FCSTD DOCUMENT  (FreeCAD 1.0R39109 (Git))
Label: internalDesign_base_Rittik
License: All rights reserved
LicenseURL: http://en.wikipedia.org/wiki/All_rights_reserved
objects: Part::Feature×500, App::Part×91, Part::Box×68, Part::Cylinder×66, Part::MultiFuse×50, Part::Cut×48, Sketcher::SketchObject×33, Part::Extrusion×32, Part::Fillet×30, Part::Compound×8, Part::Sphere×4, Part::FeaturePython×2, Part::Torus×1
note: 875 computed .brp shape members not serialized (recipe doc carries the construction recipe); baked Part::Feature solids carry a one-line shape summary decoded from their .brp

FEATURE [Part::Feature] Part__Feature016  label="Z_-16147B_ZH-16147B-01"
  shape: bbox 438.9 x 219.4 x 405.1 mm, 3210 faces (baked)
FEATURE [Part::Feature] Part__Feature017  label="INSERTS-4"
  Placement = pos=(-180.975,-168.256,-155.575) rot=(0,0,1;0rad)
  shape: bbox 7.519 x 8.463 x 7.519 mm, 71 faces (baked)
FEATURE [Part::Feature] Part__Feature018  label="INSERTS-005"
  Placement = pos=(-170.872,-174.835,-145.472) rot=(0,0,1;3.14159rad)
  shape: bbox 7.519 x 8.463 x 7.519 mm, 71 faces (baked)
FEATURE [Part::Feature] Part__Feature019  label="INSERTS-006"
  Placement = pos=(-205.994,-3.7592,-180.594) rot=(0,0,1;3.14159rad)
  shape: bbox 7.519 x 8.463 x 7.519 mm, 71 faces (baked)
FEATURE [Part::Feature] Part__Feature020  label="INSERTS-007"
  Placement = pos=(-180.975,-168.083,155.575) rot=(1,0,0;3.14159rad)
  shape: bbox 7.519 x 8.463 x 7.519 mm, 71 faces (baked)
FEATURE [Part::Feature] Part__Feature021  label="INSERTS-008"
  Placement = pos=(-170.872,-175.008,145.472) rot=(0,1,0;3.14159rad)
  shape: bbox 7.519 x 8.463 x 7.519 mm, 71 faces (baked)
FEATURE [Part::Feature] Part__Feature022  label="INSERTS-009"
  Placement = pos=(-205.994,-3.93217,180.594) rot=(0,1,0;3.14159rad)
  shape: bbox 7.519 x 8.463 x 7.519 mm, 71 faces (baked)
FEATURE [Part::Feature] Part__Feature023  label="INSERTS-010"
  Placement = pos=(180.975,-168.083,-155.575) rot=(0,0,1;3.14159rad)
  shape: bbox 7.519 x 8.463 x 7.519 mm, 71 faces (baked)
FEATURE [Part::Feature] Part__Feature024  label="INSERTS-011"
  Placement = pos=(170.872,-175.008,-145.472) rot=(0,0,1;0rad)
  shape: bbox 7.519 x 8.463 x 7.519 mm, 71 faces (baked)
FEATURE [Part::Feature] Part__Feature025  label="INSERTS-012"
  Placement = pos=(205.994,-3.93217,-180.594) rot=(0,0,1;0rad)
  shape: bbox 7.519 x 8.463 x 7.519 mm, 71 faces (baked)
FEATURE [Part::Feature] Part__Feature026  label="INSERTS-013"
  Placement = pos=(180.975,-168.256,155.575) rot=(0,1,0;3.14159rad)
  shape: bbox 7.519 x 8.463 x 7.519 mm, 71 faces (baked)
FEATURE [Part::Feature] Part__Feature027  label="INSERTS-014"
  Placement = pos=(170.872,-174.835,145.472) rot=(1,0,0;3.14159rad)
  shape: bbox 7.519 x 8.463 x 7.519 mm, 71 faces (baked)
FEATURE [Part::Feature] Part__Feature028  label="INSERTS-015"
  Placement = pos=(205.994,-3.7592,180.594) rot=(1,0,0;3.14159rad)
  shape: bbox 7.519 x 8.463 x 7.519 mm, 71 faces (baked)
FEATURE [Part::Feature] Part__Feature029  label="LABEL-104"
  Placement = pos=(-1.221e-12,-20.3197,-180.67) rot=(1,0,0;1.56207rad)
  shape: bbox 63.5 x 38.1 x 0.3833 mm, 10 faces (baked)
FEATURE [Part::Feature] Part__Feature030  label="Z_-16141C_ZH-16141C-01"
  shape: bbox 448.9 x 49.63 x 409 mm, 1738 faces (baked)
FEATURE [Part::Feature] Part__Feature031  label="ZH-1614G"
  Placement = pos=(0,0.635,6.9e-15) rot=(0,0,1;0rad)
  shape: bbox 434.5 x 6.35 x 383.7 mm, 136 faces (baked)
FEATURE [Part::Feature] Part__Feature032  label="ZH-01F_ZH-01F-01"
  Placement = pos=(-158.172,-191.294,-145.472) rot=(0,0,1;0rad)
  shape: bbox 75.05 x 15.88 x 54.71 mm, 393 faces (baked)
FEATURE [Part::Feature] Part__Feature033  label="pan cross head_ai_SCREWS-046"
  Placement = pos=(-170.872,-191.294,-145.472) rot=(-0.002139,-0.002139,0.999995;1.5708rad)
  shape: bbox 10.25 x 22.43 x 10.25 mm, 92 faces (baked)
FEATURE [Part::Feature] Part__Feature034  label="pan cross head_ai_SCREWS-047"
  Placement = pos=(-170.872,-191.294,145.472) rot=(0.002139,0.002139,0.999995;1.5708rad)
  shape: bbox 10.25 x 22.43 x 10.25 mm, 92 faces (baked)
FEATURE [Part::Feature] Part__Feature035  label="ZH-01F_ZH-01F-002"
  Placement = pos=(-158.172,-191.294,145.472) rot=(0,0,1;0rad)
  shape: bbox 75.05 x 15.88 x 54.71 mm, 393 faces (baked)
FEATURE [Part::Feature] Part__Feature036  label="pan cross head_ai_SCREWS-048"
  Placement = pos=(170.872,-191.294,-145.472) rot=(0.707106,0.707106,-0.001512;3.14462rad)
  shape: bbox 10.25 x 22.43 x 10.25 mm, 92 faces (baked)
FEATURE [Part::Feature] Part__Feature037  label="pan cross head_ai_SCREWS-049"
  Placement = pos=(170.872,-191.294,145.472) rot=(0.707106,0.707106,0.001512;3.13857rad)
  shape: bbox 10.25 x 22.43 x 10.25 mm, 92 faces (baked)
FEATURE [Part::Feature] Part__Feature038  label="ZH-01F_ZH-01F-003"
  Placement = pos=(158.172,-191.294,-145.472) rot=(0,1,0;3.14159rad)
  shape: bbox 75.05 x 15.88 x 54.71 mm, 393 faces (baked)
FEATURE [Part::Feature] Part__Feature039  label="ZH-01F_ZH-01F-004"
  Placement = pos=(158.172,-191.294,145.472) rot=(0,1,0;3.14159rad)
  shape: bbox 75.05 x 15.88 x 54.71 mm, 393 faces (baked)
FEATURE [Part::Feature] Part__Feature040  label="SCREWS-047_default"
  Placement = pos=(-205.994,12.0142,-180.594) rot=(-1,0,0;1.5708rad)
  shape: bbox 9.234 x 22.51 x 9.177 mm, 32 faces (baked)
FEATURE [Part::Feature] Part__Feature041  label="SCREWS-047_default001"
  Placement = pos=(205.994,12.0142,-180.594) rot=(-1,0,0;1.5708rad)
  shape: bbox 9.234 x 22.51 x 9.177 mm, 32 faces (baked)
FEATURE [Part::Feature] Part__Feature042  label="SCREWS-047_default002"
  Placement = pos=(-205.994,12.0142,180.594) rot=(-1,0,0;1.5708rad)
  shape: bbox 9.234 x 22.51 x 9.177 mm, 32 faces (baked)
FEATURE [Part::Feature] Part__Feature043  label="SCREWS-047_default003"
  Placement = pos=(205.994,12.0142,180.594) rot=(-1,0,0;1.5708rad)
  shape: bbox 9.234 x 22.51 x 9.177 mm, 32 faces (baked)
FEATURE [App::Part] Z__16141CG_ZH_16141CG_01  label="Z_-16141CG_ZH-16141CG-01"
  Group = -> [Part__Feature030,Part__Feature031]
  Origin = -> Origin005
FEATURE [App::Part] Z__16147BI_ZH_16147BI_01  label="Z_-16147BI_ZH-16147BI-01"
  Group = -> [Part__Feature016,Part__Feature017,Part__Feature018,Part__Feature019,Part__Feature020,Part__Feature021,Part__Feature022,Part__Feature023,Part__Feature024,Part__Feature025,Part__Feature026,Part__Feature027,Part__Feature028,Part__Feature029]
  Origin = -> Origin004
FEATURE [App::Part] ZH_161407_33  label="ZH-161407-33"
  Group = -> [Z__16147BI_ZH_16147BI_01,Z__16141CG_ZH_16141CG_01,Part__Feature032,Part__Feature033,Part__Feature034,Part__Feature035,Part__Feature036,Part__Feature037,Part__Feature038,Part__Feature039,Part__Feature040,Part__Feature041,Part__Feature042,Part__Feature043]
  Origin = -> Origin006
  Placement = pos=(0,0,0) rot=(0.707107,0,0.707107;3.14159rad)
FEATURE [Sketcher::SketchObject] Sketch
  ArcFitTolerance = 0
  FullyConstrained = true
  MakeInternals = false
  Placement = pos=(0,164,0) rot=(1,0,0;1.5708rad)
  sketch-geometry (76):
    g0: ArcOfCircle CenterX=-140.58 CenterY=-165.98 CenterZ=0 NormalX=0 NormalY=0 NormalZ=1 AngleXU=0 Radius=30 StartAngle=3.14159 EndAngle=4.71239
    g1: ArcOfCircle CenterX=-140.58 CenterY=165.98 CenterZ=0 NormalX=0 NormalY=0 NormalZ=1 AngleXU=0 Radius=30 StartAngle=1.5708 EndAngle=3.14159
    g2: ArcOfCircle CenterX=140.58 CenterY=165.98 CenterZ=0 NormalX=0 NormalY=0 NormalZ=1 AngleXU=0 Radius=30 StartAngle=0 EndAngle=1.5708
    g3: ArcOfCircle CenterX=140.58 CenterY=-165.98 CenterZ=0 NormalX=0 NormalY=0 NormalZ=1 AngleXU=0 Radius=30 StartAngle=4.71239 EndAngle=6.28319
    g4: LineSegment StartX=-140.58 StartY=195.98 StartZ=0 EndX=140.58 EndY=195.98 EndZ=0
    g5: LineSegment StartX=-170.58 StartY=165.98 StartZ=0 EndX=-170.58 EndY=-165.98 EndZ=0
    g6: LineSegment StartX=-140.58 StartY=-195.98 StartZ=0 EndX=140.58 EndY=-195.98 EndZ=0
    g7: LineSegment StartX=170.58 StartY=-165.98 StartZ=0 EndX=170.58 EndY=165.98 EndZ=0
    g8: Circle CenterX=-155.58 CenterY=180.98 CenterZ=0 NormalX=0 NormalY=0 NormalZ=1 AngleXU=0 Radius=2.5
    g9: Circle CenterX=-155.58 CenterY=-180.98 CenterZ=0 NormalX=0 NormalY=0 NormalZ=1 AngleXU=0 Radius=2.5
    g10: Circle CenterX=155.58 CenterY=180.98 CenterZ=0 NormalX=0 NormalY=0 NormalZ=1 AngleXU=0 Radius=2.5
    g11: Circle CenterX=155.58 CenterY=-180.98 CenterZ=0 NormalX=0 NormalY=0 NormalZ=1 AngleXU=0 Radius=2.5
    g12: Circle CenterX=-148.48 CenterY=165.98 CenterZ=0 NormalX=0 NormalY=0 NormalZ=1 AngleXU=0 Radius=1.975
    g13: Circle CenterX=-148.48 CenterY=113.98 CenterZ=0 NormalX=0 NormalY=0 NormalZ=1 AngleXU=0 Radius=1.975
    g14: Circle CenterX=-129.58 CenterY=95.63 CenterZ=0 NormalX=0 NormalY=0 NormalZ=1 AngleXU=0 Radius=1.975
    g15: Circle CenterX=-129.58 CenterY=171.78 CenterZ=0 NormalX=0 NormalY=0 NormalZ=1 AngleXU=0 Radius=1.975
    g16: Circle CenterX=68.03 CenterY=171.78 CenterZ=0 NormalX=0 NormalY=0 NormalZ=1 AngleXU=0 Radius=1.975
    g17: Circle CenterX=68.03 CenterY=95.63 CenterZ=0 NormalX=0 NormalY=0 NormalZ=1 AngleXU=0 Radius=1.975
    g18: Circle CenterX=88.08 CenterY=189.98 CenterZ=0 NormalX=0 NormalY=0 NormalZ=1 AngleXU=0 Radius=1.975
    g19: Circle CenterX=88.08 CenterY=164.98 CenterZ=0 NormalX=0 NormalY=0 NormalZ=1 AngleXU=0 Radius=1.975
    g20: Circle CenterX=126.08 CenterY=189.98 CenterZ=0 NormalX=0 NormalY=0 NormalZ=1 AngleXU=0 Radius=1.975
    g21: Circle CenterX=126.08 CenterY=164.98 CenterZ=0 NormalX=0 NormalY=0 NormalZ=1 AngleXU=0 Radius=1.975
    g22: Circle CenterX=139.33 CenterY=105.98 CenterZ=0 NormalX=0 NormalY=0 NormalZ=1 AngleXU=0 Radius=1.975
    g23: Circle CenterX=139.33 CenterY=68.98 CenterZ=0 NormalX=0 NormalY=0 NormalZ=1 AngleXU=0 Radius=1.975
    g24: Circle CenterX=139.33 CenterY=24.98 CenterZ=0 NormalX=0 NormalY=0 NormalZ=1 AngleXU=0 Radius=1.975
    g25: Circle CenterX=139.33 CenterY=-12.02 CenterZ=0 NormalX=0 NormalY=0 NormalZ=1 AngleXU=0 Radius=1.975
    g26: Circle CenterX=98.53 CenterY=52.98 CenterZ=0 NormalX=0 NormalY=0 NormalZ=1 AngleXU=0 Radius=1.975
    g27: Circle CenterX=98.53 CenterY=-30.02 CenterZ=0 NormalX=0 NormalY=0 NormalZ=1 AngleXU=0 Radius=1.975
    g28: Circle CenterX=43.03 CenterY=-29.98 CenterZ=0 NormalX=0 NormalY=0 NormalZ=1 AngleXU=0 Radius=1.975
    g29: Circle CenterX=28.03 CenterY=-29.98 CenterZ=0 NormalX=0 NormalY=0 NormalZ=1 AngleXU=0 Radius=1.975
    g30: Circle CenterX=13.03 CenterY=-29.98 CenterZ=0 NormalX=0 NormalY=0 NormalZ=1 AngleXU=0 Radius=1.975
    g31: Circle CenterX=-1.97 CenterY=-29.98 CenterZ=0 NormalX=0 NormalY=0 NormalZ=1 AngleXU=0 Radius=1.975
    g32: Circle CenterX=-16.97 CenterY=-29.98 CenterZ=0 NormalX=0 NormalY=0 NormalZ=1 AngleXU=0 Radius=1.975
    g33: Circle CenterX=43.03 CenterY=69.98 CenterZ=0 NormalX=0 NormalY=0 NormalZ=1 AngleXU=0 Radius=1.975
    g34: Circle CenterX=28.03 CenterY=69.98 CenterZ=0 NormalX=0 NormalY=0 NormalZ=1 AngleXU=0 Radius=1.975
    g35: Circle CenterX=13.03 CenterY=69.98 CenterZ=0 NormalX=0 NormalY=0 NormalZ=1 AngleXU=0 Radius=1.975
    g36: Circle CenterX=-1.97 CenterY=69.98 CenterZ=0 NormalX=0 NormalY=0 NormalZ=1 AngleXU=0 Radius=1.975
    g37: Circle CenterX=-16.97 CenterY=69.98 CenterZ=0 NormalX=0 NormalY=0 NormalZ=1 AngleXU=0 Radius=1.975
    g38: Circle CenterX=-61.98 CenterY=69.98 CenterZ=0 NormalX=0 NormalY=0 NormalZ=1 AngleXU=0 Radius=1.975
    g39: Circle CenterX=-76.98 CenterY=69.98 CenterZ=0 NormalX=0 NormalY=0 NormalZ=1 AngleXU=0 Radius=1.975
    g40: Circle CenterX=-91.98 CenterY=69.98 CenterZ=0 NormalX=0 NormalY=0 NormalZ=1 AngleXU=0 Radius=1.975
    g41: Circle CenterX=-106.98 CenterY=69.98 CenterZ=0 NormalX=0 NormalY=0 NormalZ=1 AngleXU=0 Radius=1.975
    g42: Circle CenterX=-121.98 CenterY=69.98 CenterZ=0 NormalX=0 NormalY=0 NormalZ=1 AngleXU=0 Radius=1.975
    g43: Circle CenterX=-61.98 CenterY=-29.98 CenterZ=0 NormalX=0 NormalY=0 NormalZ=1 AngleXU=0 Radius=1.975
    g44: Circle CenterX=-76.98 CenterY=-29.98 CenterZ=0 NormalX=0 NormalY=0 NormalZ=1 AngleXU=0 Radius=1.975
    g45: Circle CenterX=-91.98 CenterY=-29.98 CenterZ=0 NormalX=0 NormalY=0 NormalZ=1 AngleXU=0 Radius=1.975
    g46: Circle CenterX=-106.98 CenterY=-29.98 CenterZ=0 NormalX=0 NormalY=0 NormalZ=1 AngleXU=0 Radius=1.975
    g47: Circle CenterX=-121.98 CenterY=-29.98 CenterZ=0 NormalX=0 NormalY=0 NormalZ=1 AngleXU=0 Radius=1.975
    g48: Circle CenterX=-150.98 CenterY=-46.48 CenterZ=0 NormalX=0 NormalY=0 NormalZ=1 AngleXU=0 Radius=1.975
    g49: Circle CenterX=-164.98 CenterY=-46.48 CenterZ=0 NormalX=0 NormalY=0 NormalZ=1 AngleXU=0 Radius=1.975
    g50: Circle CenterX=-150.98 CenterY=90.48 CenterZ=0 NormalX=0 NormalY=0 NormalZ=1 AngleXU=0 Radius=1.975
    g51: Circle CenterX=-164.98 CenterY=90.48 CenterZ=0 NormalX=0 NormalY=0 NormalZ=1 AngleXU=0 Radius=1.975
    g52: Circle CenterX=147.48 CenterY=-166.23 CenterZ=0 NormalX=0 NormalY=0 NormalZ=1 AngleXU=0 Radius=1.975
    g53: Circle CenterX=160.48 CenterY=-166.23 CenterZ=0 NormalX=0 NormalY=0 NormalZ=1 AngleXU=0 Radius=1.975
    g54: Circle CenterX=145 CenterY=-91.48 CenterZ=0 NormalX=0 NormalY=0 NormalZ=1 AngleXU=0 Radius=1.975
    g55: Circle CenterX=132 CenterY=-91.48 CenterZ=0 NormalX=0 NormalY=0 NormalZ=1 AngleXU=0 Radius=1.975
    g56: Circle CenterX=131.92 CenterY=-104.23 CenterZ=0 NormalX=0 NormalY=0 NormalZ=1 AngleXU=0 Radius=1.975
    g57: Circle CenterX=87.92 CenterY=-104.23 CenterZ=0 NormalX=0 NormalY=0 NormalZ=1 AngleXU=0 Radius=1.975
    g58: Circle CenterX=131.92 CenterY=-119.23 CenterZ=0 NormalX=0 NormalY=0 NormalZ=1 AngleXU=0 Radius=1.975
    g59: Circle CenterX=87.92 CenterY=-119.23 CenterZ=0 NormalX=0 NormalY=0 NormalZ=1 AngleXU=0 Radius=1.975
    g60: Circle CenterX=131.92 CenterY=-134.23 CenterZ=0 NormalX=0 NormalY=0 NormalZ=1 AngleXU=0 Radius=1.975
    g61: Circle CenterX=87.92 CenterY=-134.23 CenterZ=0 NormalX=0 NormalY=0 NormalZ=1 AngleXU=0 Radius=1.975
    g62: Circle CenterX=58.97 CenterY=-164.03 CenterZ=0 NormalX=0 NormalY=0 NormalZ=1 AngleXU=0 Radius=1.975
    g63: Circle CenterX=21.97 CenterY=-164.03 CenterZ=0 NormalX=0 NormalY=0 NormalZ=1 AngleXU=0 Radius=1.975
    g64: Circle CenterX=-22.03 CenterY=-164.03 CenterZ=0 NormalX=0 NormalY=0 NormalZ=1 AngleXU=0 Radius=1.975
    g65: Circle CenterX=-59.03 CenterY=-164.03 CenterZ=0 NormalX=0 NormalY=0 NormalZ=1 AngleXU=0 Radius=1.975
    g66: Circle CenterX=-164.28 CenterY=-151.48 CenterZ=0 NormalX=0 NormalY=0 NormalZ=1 AngleXU=0 Radius=1.975
    g67: Circle CenterX=-79.28 CenterY=-151.48 CenterZ=0 NormalX=0 NormalY=0 NormalZ=1 AngleXU=0 Radius=1.975
    g68: Circle CenterX=5.72 CenterY=-151.48 CenterZ=0 NormalX=0 NormalY=0 NormalZ=1 AngleXU=0 Radius=1.975
    g69: Circle CenterX=75.72 CenterY=-58.98 CenterZ=0 NormalX=0 NormalY=0 NormalZ=1 AngleXU=0 Radius=1.975
    g70: Circle CenterX=-9.28 CenterY=-58.98 CenterZ=0 NormalX=0 NormalY=0 NormalZ=1 AngleXU=0 Radius=1.975
    g71: Circle CenterX=-94.28 CenterY=-58.98 CenterZ=0 NormalX=0 NormalY=0 NormalZ=1 AngleXU=0 Radius=1.975
    g72: Circle CenterX=11.33 CenterY=189.98 CenterZ=0 NormalX=0 NormalY=0 NormalZ=1 AngleXU=0 Radius=1.975
    g73: Circle CenterX=-11.17 CenterY=189.98 CenterZ=0 NormalX=0 NormalY=0 NormalZ=1 AngleXU=0 Radius=1.975
    g74: Circle CenterX=87.92 CenterY=-149.23 CenterZ=0 NormalX=0 NormalY=0 NormalZ=1 AngleXU=0 Radius=1.975
    g75: Circle CenterX=131.92 CenterY=-149.23 CenterZ=0 NormalX=0 NormalY=0 NormalZ=1 AngleXU=0 Radius=1.975
  constraints (172):
    c: Coincident(g4,g1)
    c: Coincident(g4,g2)
    c: Horizontal(g4)
    c: Coincident(g5,g1)
    c: Coincident(g5,g0)
    c: Vertical(g5)
    c: Coincident(g6,g0)
    c: Coincident(g6,g3)
    c: Horizontal(g6)
    c: Coincident(g7,g3)
    c: Coincident(g7,g2)
    c: Vertical(g7)
    c: Horizontal(g2,g2)
    c: Vertical(g2,g2)
    c: Vertical(g1,g1)
    c: Vertical(g0,g0)
    c: Vertical(g3,g3)
    c: Horizontal(g3,g3)
    c: DistanceX(g2,g2) = 30
    c: Horizontal(g3,g0)
    c: Vertical(g0,g1)
    c: DistanceX(g1,g8) = 15
    c: DistanceY(g8,g1) = 15
    c: DistanceX(g8) = -155.58
    c: DistanceX(g9) = -155.58
    c: DistanceY(g9) = -180.98
    c: DistanceY(g8) = 180.98
    c: DistanceY(g0,g9) = 15
    c: Horizontal(g1,g1)
    c: DistanceX(g1,g1) = 30
    c: Horizontal(g10,g8)
    c: DistanceX(g10,g2) = 15
    c: DistanceX(g10) = 155.58
    c: Horizontal(g11,g9)
    c: Vertical(g11,g10)
    c: DistanceY(g9,g0) = 15
    c: Equal(g8,g10)
    c: Equal(g8,g11)
    c: Equal(g8,g9)
    c: Diameter(g8) = 5
    c: Equal(g12, g13-g73) x61
    c: Diameter(g12) = 3.95
    c: Distance(g20,g4) = 6
    c: Distance(g20,g7) = 44.5
    c: Horizontal(g20,g18)
    c: Vertical(g20,g21)
    c: Distance(g21,g4) = 31
    c: Horizontal(g21,g19)
    c: Vertical(g19,g18)
    c: Distance(g18,g7) = 82.5
    c: Distance(g72,g4) = 6
    c: Distance(g72,g7) = 159.25
    c: Horizontal(g72,g73)
    c: Distance(g73,g7) = 181.75
    c: Distance(g12,g5) = 22.1
    c: Distance(g12,g4) = 30
    c: Vertical(g12,g13)
    c: Distance(g13,g4) = 82
    c: Distance(g17,g4) = 100.35
    c: Distance(g17,g7) = 102.55
    c: Vertical(g17,g16)
    c: Distance(g16,g4) = 24.2
    c: Horizontal(g16,g15)
    c: Distance(g15,g5) = 41
    c: Vertical(g15,g14)
    c: Distance(g14,g4) = 100.35
    c: Distance(g22,g7) = 31.25
    c: Distance(g22,g4) = 90
    c: Vertical(g22,g23)
    c: Vertical(g23,g24)
    c: Vertical(g24,g25)
    c: Distance(g23,g4) = 127
    c: Distance(g24,g4) = 171
    c: Distance(g25,g4) = 208
    c: Distance(g26,g7) = 72.05
    c: Distance(g26,g4) = 143
    c: Vertical(g26,g27)
    c: Distance(g27,g4) = 226
    c: Distance(g33,g4) = 126
    c: Distance(g33,g7) = 127.55
    c: Horizontal(g33,g34)
    c: Horizontal(g33,g35)
    c: Horizontal(g33,g36)
    c: Horizontal(g33,g37)
    c: Horizontal(g33,g38)
    c: Horizontal(g33,g39)
    c: Horizontal(g33,g40)
    c: Horizontal(g33,g41)
    c: Horizontal(g33,g42)
    c: Distance(g34,g7) = 142.55
    c: Distance(g35,g7) = 157.55
    c: Distance(g36,g7) = 172.55
    c: Distance(g37,g7) = 187.55
    c: Distance(g47,g6) = 166
    c: Distance(g47,g5) = 48.6
    c: Vertical(g47,g42)
    c: Horizontal(g47,g46)
    c: Vertical(g46,g41)
    c: Distance(g46,g5) = 63.6
    c: Horizontal(g46,g45)
    c: Horizontal(g45,g44)
    c: Horizontal(g44,g43)
    c: Distance(g45,g5) = 78.6
    c: Distance(g44,g5) = 93.6
    c: Distance(g43,g5) = 108.6
    c: Vertical(g45,g40)
    c: Vertical(g44,g39)
    c: Vertical(g43,g38)
    c: Vertical(g37,g32)
    c: Horizontal(g43,g32)
    c: Horizontal(g32,g31)
    c: Horizontal(g31,g30)
    c: Horizontal(g30,g29)
    c: Horizontal(g29,g28)
    c: Vertical(g31,g36)
    c: Vertical(g30,g35)
    c: Vertical(g29,g34)
    c: Vertical(g28,g33)
    c: Distance(g51,g4) = 105.5
    c: Distance(g51,g5) = 5.6
    c: Horizontal(g51,g50)
    c: Distance(g50,g5) = 19.6
    c: Vertical(g51,g49)
    c: Distance(g49,g6) = 149.5
    c: Horizontal(g49,g48)
    c: Vertical(g48,g50)
    c: Distance(g66,g5) = 6.3
    c: Distance(g66,g6) = 44.5
    c: Horizontal(g66,g67)
    c: Horizontal(g67,g68)
    c: Distance(g67,g5) = 91.3
    c: Distance(g68,g5) = 176.3
    c: Distance(g71,g5) = 76.3
    c: Distance(g71,g6) = 137
    c: Horizontal(g71,g70)
    c: Horizontal(g70,g69)
    c: Distance(g70,g5) = 161.3
    c: Distance(g69,g5) = 246.3
    c: Distance(g57,g6) = 91.75
    c: Distance(g57,g5) = 258.5
    c: Horizontal(g57,g56)
    c: Vertical(g57,g59)
    c: Vertical(g59,g61)
    c: Distance(g56,g5) = 302.5
    c: Vertical(g56,g58)
    c: Vertical(g58,g60)
    c: Distance(g59,g6) = 76.75
    c: Horizontal(g59,g58)
    c: Horizontal(g61,g60)
    c: Distance(g61,g6) = 61.75
    c: Equal(g75,g74)
    c: Diameter(g75) = 3.95
    c: Vertical(g61,g74)
    c: Horizontal(g74,g75)
    c: Vertical(g60,g75)
    c: Distance(g74,g6) = 46.75
    c: Distance(g65,g6) = 31.95
    c: Distance(g65,g5) = 111.55
    c: Horizontal(g65,g64)
    c: Horizontal(g64,g63)
    c: Horizontal(g63,g62)
    c: Distance(g64,g5) = 148.55
    c: Distance(g63,g5) = 192.55
    c: Distance(g62,g5) = 229.55
    c: Distance(g52,g7) = 23.1
    c: Distance(g52,g6) = 29.75
    c: Horizontal(g52,g53)
    c: Distance(g53,g7) = 10.1
    c: Distance(g55,g7) = 38.58
    c: Distance(g55,g6) = 104.5
    c: Horizontal(g55,g54)
    c: Distance(g54,g7) = 25.58
FEATURE [Part::Extrusion] Extrude  label="base"
  Base = -> Sketch
  Dir = (0,-1,2e-16)
  DirMode = 2
  FaceMakerClass = Part::FaceMakerBullseye
  FaceMakerMode = 3
  LengthFwd = 6
  LengthRev = 0
  Solid = true
  Symmetric = false
FEATURE [Part::Box] Box  label="Base_Board"
  AttacherType = Attacher::AttachEngine3D
  Height = 2
  Length = 208
  Width = 89.3
FEATURE [Part::Box] Box001  label="Ozone_monitor"
  AttacherType = Attacher::AttachEngine3D
  Height = 70
  Length = 189.5
  Placement = pos=(9.5,62.5,2) rot=(0,0,1;0rad)
  Width = 26.75
FEATURE [Part::Cylinder] Cylinder
  Angle = 360
  AttacherType = Attacher::AttachEngine3D
  FirstAngle = 0
  Height = 10
  Placement = pos=(5.4,6.4,0) rot=(0,0,1;0rad)
  Radius = 1.75
  SecondAngle = 0
FEATURE [Part::Cylinder] Cylinder001
  Angle = 360
  AttacherType = Attacher::AttachEngine3D
  FirstAngle = 0
  Height = 10
  Placement = pos=(5.4,82.6,0) rot=(0,0,1;0rad)
  Radius = 1.75
  SecondAngle = 0
FEATURE [Part::Cylinder] Cylinder002
  Angle = 360
  AttacherType = Attacher::AttachEngine3D
  FirstAngle = 0
  Height = 10
  Placement = pos=(203,82.6,0) rot=(0,0,1;0rad)
  Radius = 1.75
  SecondAngle = 0
FEATURE [Part::Cylinder] Cylinder003
  Angle = 360
  AttacherType = Attacher::AttachEngine3D
  FirstAngle = 0
  Height = 10
  Placement = pos=(203,6.4,0) rot=(0,0,1;0rad)
  Radius = 1.75
  SecondAngle = 0
FEATURE [Part::Fillet] Fillet  label="Base"
  Base = -> Box
  EdgeLinks = -> Box [Edge1,Edge3,Edge5,Edge7]
  Edges = 4 edges r=2.5: [Edge1,Edge3,Edge5,Edge7]
FEATURE [Part::MultiFuse] Fusion  label="Base_hole"
  Placement = pos=(0,0,-4) rot=(0,0,1;0rad)
  Shapes = -> [Cylinder,Cylinder001,Cylinder002,Cylinder003]
FEATURE [Part::MultiFuse] Fusion001  label="Ozone"
  Shapes = -> [Fillet,Box001]
FEATURE [Part::Cut] Cut  label="Ozone Module"
  Base = -> Fusion001
  Placement = pos=(-135,157,89.2) rot=(1,0,0;1.5708rad)
  Tool = -> Fusion
FEATURE [Part::Feature] Part__Feature165  label="CUI_VGS-35C-052"
  shape: bbox 82 x 30 x 99 mm, 244 faces (baked)
FEATURE [Part::Feature] Part__Feature166  label="CUI_VGS-35C-053"
  shape: bbox 49.5 x 17 x 16 mm, 923 faces (baked)
FEATURE [Part::Feature] Part__Feature167  label="CUI_VGS-35C-054"
  shape: bbox 4.624 x 1.433 x 4.618 mm, 8 faces (baked)
FEATURE [Part::Feature] Part__Feature168  label="CUI_VGS-35C-055"
  shape: bbox 5.413 x 8.147 x 5.413 mm, 53 faces (baked)
FEATURE [Part::Feature] Part__Feature169  label="CUI_VGS-35C-056"
  shape: bbox 5.8 x 4.834 x 5.8 mm, 40 faces (baked)
FEATURE [Part::Feature] Part__Feature170  label="CUI_VGS-35C-057"
  shape: bbox 3 x 7.6 x 3.04 mm, 12 faces (baked)
FEATURE [Part::Feature] Part__Feature171  label="CUI_VGS-35C-058"
  shape: bbox 81 x 29 x 76 mm, 406 faces (baked)
FEATURE [Part::Feature] Part__Feature172  label="CUI_VGS-35C-059"
  shape: bbox 7 x 0.55 x 7 mm, 6 faces (baked)
FEATURE [Part::Feature] Part__Feature173  label="CUI_VGS-35C-060"
  shape: bbox 6.811 x 11.02 x 8.111 mm, 138 faces (baked)
FEATURE [Part::Feature] Part__Feature174  label="CUI_VGS-35C-061"
  shape: bbox 78.62 x 1.622 x 92.02 mm, 385 faces (baked)
FEATURE [App::Part] CUI_VGS_35C_016  label="CUI_VGS-35C-022:12V-01"
  Group = -> [Part__Feature165,Part__Feature166,Part__Feature167,Part__Feature168,Part__Feature169,Part__Feature170,Part__Feature171,Part__Feature172,Part__Feature173,Part__Feature174]
  Origin = -> Origin017
  Placement = pos=(-130,141,-106.5) rot=(1,0,0;3.14159rad)
FEATURE [Part::Feature] Part__Feature175  label="CUI_VGS-35C-062"
  shape: bbox 82 x 30 x 99 mm, 244 faces (baked)
FEATURE [Part::Feature] Part__Feature176  label="CUI_VGS-35C-063"
  shape: bbox 49.5 x 17 x 16 mm, 923 faces (baked)
FEATURE [Part::Feature] Part__Feature177  label="CUI_VGS-35C-064"
  shape: bbox 4.624 x 1.433 x 4.618 mm, 8 faces (baked)
FEATURE [Part::Feature] Part__Feature178  label="CUI_VGS-35C-065"
  shape: bbox 5.413 x 8.147 x 5.413 mm, 53 faces (baked)
FEATURE [Part::Feature] Part__Feature179  label="CUI_VGS-35C-066"
  shape: bbox 5.8 x 4.834 x 5.8 mm, 40 faces (baked)
FEATURE [Part::Feature] Part__Feature180  label="CUI_VGS-35C-067"
  shape: bbox 3 x 7.6 x 3.04 mm, 12 faces (baked)
FEATURE [Part::Feature] Part__Feature181  label="CUI_VGS-35C-068"
  shape: bbox 81 x 29 x 76 mm, 406 faces (baked)
FEATURE [Part::Feature] Part__Feature182  label="CUI_VGS-35C-069"
  shape: bbox 7 x 0.55 x 7 mm, 6 faces (baked)
FEATURE [Part::Feature] Part__Feature183  label="CUI_VGS-35C-070"
  shape: bbox 6.811 x 11.02 x 8.111 mm, 138 faces (baked)
FEATURE [Part::Feature] Part__Feature184  label="CUI_VGS-35C-071"
  shape: bbox 78.62 x 1.622 x 92.02 mm, 385 faces (baked)
FEATURE [App::Part] CUI_VGS_35C_017  label="CUI_VGS-35C-022:12V-02"
  Group = -> [Part__Feature175,Part__Feature176,Part__Feature177,Part__Feature178,Part__Feature179,Part__Feature180,Part__Feature181,Part__Feature182,Part__Feature183,Part__Feature184]
  Origin = -> Origin018
  Placement = pos=(-45,141,-106.5) rot=(1,0,0;3.14159rad)
FEATURE [Part::Feature] Part__Feature185  label="CUI_VGS-35C-072"
  shape: bbox 82 x 30 x 99 mm, 244 faces (baked)
FEATURE [Part::Feature] Part__Feature186  label="CUI_VGS-35C-073"
  shape: bbox 49.5 x 17 x 16 mm, 923 faces (baked)
FEATURE [Part::Feature] Part__Feature187  label="CUI_VGS-35C-074"
  shape: bbox 4.624 x 1.433 x 4.618 mm, 8 faces (baked)
FEATURE [Part::Feature] Part__Feature188  label="CUI_VGS-35C-075"
  shape: bbox 5.413 x 8.147 x 5.413 mm, 53 faces (baked)
FEATURE [Part::Feature] Part__Feature189  label="CUI_VGS-35C-076"
  shape: bbox 5.8 x 4.834 x 5.8 mm, 40 faces (baked)
FEATURE [Part::Feature] Part__Feature190  label="CUI_VGS-35C-077"
  shape: bbox 3 x 7.6 x 3.04 mm, 12 faces (baked)
FEATURE [Part::Feature] Part__Feature191  label="CUI_VGS-35C-078"
  shape: bbox 81 x 29 x 76 mm, 406 faces (baked)
FEATURE [Part::Feature] Part__Feature192  label="CUI_VGS-35C-079"
  shape: bbox 7 x 0.55 x 7 mm, 6 faces (baked)
FEATURE [Part::Feature] Part__Feature193  label="CUI_VGS-35C-080"
  shape: bbox 6.811 x 11.02 x 8.111 mm, 138 faces (baked)
FEATURE [Part::Feature] Part__Feature194  label="CUI_VGS-35C-081"
  shape: bbox 78.62 x 1.622 x 92.02 mm, 385 faces (baked)
FEATURE [App::Part] CUI_VGS_35C_018  label="CUI_VGS-35C-022:12V-03"
  Group = -> [Part__Feature185,Part__Feature186,Part__Feature187,Part__Feature188,Part__Feature189,Part__Feature190,Part__Feature191,Part__Feature192,Part__Feature193,Part__Feature194]
  Origin = -> Origin019
  Placement = pos=(40,141,-106.5) rot=(1,0,0;3.14159rad)
FEATURE [Part::Box] Box003  label="Cube003"
  AttacherType = Attacher::AttachEngine3D
  Height = 57
  Length = 14.7
  Placement = pos=(-29,-7,-28) rot=(0,0,1;0rad)
  Width = 38
FEATURE [Part::Box] Box004  label="Cube004"
  AttacherType = Attacher::AttachEngine3D
  Height = 57
  Length = 14.7
  Placement = pos=(14.3,-7,-31) rot=(0,0,1;0rad)
  Width = 38
FEATURE [Part::Box] Box005  label="Cube009"
  AttacherType = Attacher::AttachEngine3D
  Height = 25
  Length = 31
  Placement = pos=(37.5,83.5,6) rot=(0,0,1;0rad)
  Width = 27
FEATURE [Part::Box] Box006  label="lan_cube"
  AttacherType = Attacher::AttachEngine3D
  Height = 13.25
  Length = 16.5
  Placement = pos=(11.25,101,14.8) rot=(0,0,1;0rad)
  Width = 10
FEATURE [Part::Box] Box007  label="Cube010"
  AttacherType = Attacher::AttachEngine3D
  Height = 10
  Length = 21
  Placement = pos=(5.5,15,0) rot=(0,0,1;0rad)
  Width = 13.5
FEATURE [Part::Box] Box013  label="Cube"
  AttacherType = Attacher::AttachEngine3D
  Height = 37
  Length = 78.5
  Width = 108.5
FEATURE [Part::Box] Box014  label="Cube001"
  AttacherType = Attacher::AttachEngine3D
  Height = 27.5
  Length = 27
  Placement = pos=(26.5,0,4.75) rot=(0,0,1;0rad)
  Width = 20
FEATURE [Part::Box] Box015  label="Cube002"
  AttacherType = Attacher::AttachEngine3D
  Height = 57
  Length = 62
  Placement = pos=(-29,-44,-31) rot=(0,0,1;0rad)
  Width = 38
FEATURE [Part::Box] Box016  label="Cube011"
  AttacherType = Attacher::AttachEngine3D
  Height = 10
  Length = 20.8
  Placement = pos=(5.6,15.1,0) rot=(0,0,1;0rad)
  Width = 13.3
FEATURE [Part::Box] Box017  label="Cube012"
  AttacherType = Attacher::AttachEngine3D
  Height = 5
  Length = 21
  Placement = pos=(5.5,13.5,0) rot=(0,0,1;0rad)
  Width = 13.5
FEATURE [Part::Box] Box018  label="Cube013"
  AttacherType = Attacher::AttachEngine3D
  Height = 5
  Length = 20.8
  Placement = pos=(5.5,13.5,0) rot=(0,0,1;0rad)
  Width = 13.3
FEATURE [Part::Box] Box019  label="Cube014"
  AttacherType = Attacher::AttachEngine3D
  Height = 29.5
  Length = 120
  Width = 120
FEATURE [Part::Box] Box020  label="Cube015"
  AttacherType = Attacher::AttachEngine3D
  Height = 3.17
  Length = 9
  Placement = pos=(21.5,-6,5.92) rot=(0,0,1;0rad)
  Width = 10
FEATURE [Part::Box] Box021  label="Cube016"
  AttacherType = Attacher::AttachEngine3D
  Height = 13.25
  Length = 16.5
  Placement = pos=(40.25,0,6) rot=(0,0,1;0rad)
  Width = 10
FEATURE [Part::Box] Box022  label="Cube017"
  AttacherType = Attacher::AttachEngine3D
  Height = 6.5
  Length = 14.5
  Width = 10
FEATURE [Part::Box] Box023  label="Cube018"
  AttacherType = Attacher::AttachEngine3D
  Height = 1.75
  Length = 10
  Placement = pos=(110,76.5,5.5) rot=(0,0,1;0rad)
  Width = 17
FEATURE [Part::Box] Box024  label="Bottom_left"
  AttacherType = Attacher::AttachEngine3D
  Height = 27
  Length = 10
  Placement = pos=(-65,148,-38.5) rot=(0,0,1;0rad)
  Width = 10
FEATURE [Part::Box] Box025  label="Bottom_right"
  AttacherType = Attacher::AttachEngine3D
  Height = 27
  Length = 10
  Placement = pos=(55,148,-38.5) rot=(0,0,1;0rad)
  Width = 10
FEATURE [Part::Box] Box026  label="Top_left"
  AttacherType = Attacher::AttachEngine3D
  Height = 36.5
  Length = 10
  Placement = pos=(-45.68,71,-48) rot=(0,0,1;0rad)
  Width = 7
FEATURE [Part::Box] Box027  label="Top_right"
  AttacherType = Attacher::AttachEngine3D
  Height = 36.5
  Length = 10
  Placement = pos=(35.68,71,-48) rot=(0,0,1;0rad)
  Width = 7
FEATURE [Part::Box] Box028  label="Top_middle"
  AttacherType = Attacher::AttachEngine3D
  Height = 36.5
  Length = 16
  Placement = pos=(-8,71,-48) rot=(0,0,1;0rad)
  Width = 7
FEATURE [Part::Box] Box029  label="Bottom_left001"
  AttacherType = Attacher::AttachEngine3D
  Height = 27
  Length = 10
  Placement = pos=(-70.5,140,-38.5) rot=(0,0,1;0rad)
  Width = 18
FEATURE [Part::Box] Box030  label="Bottom_right001"
  AttacherType = Attacher::AttachEngine3D
  Height = 27
  Length = 10
  Placement = pos=(60.5,140,-38.5) rot=(0,0,1;0rad)
  Width = 18
FEATURE [Part::Box] Box031  label="Top_left001"
  AttacherType = Attacher::AttachEngine3D
  Height = 36.5
  Length = 15
  Placement = pos=(-50,28,-48) rot=(0,0,1;0rad)
  Width = 7
FEATURE [Part::Box] Box032  label="Top_right001"
  AttacherType = Attacher::AttachEngine3D
  Height = 36.5
  Length = 15
  Placement = pos=(35,28,-48) rot=(0,0,1;0rad)
  Width = 7
FEATURE [Part::Box] Box033  label="Top_middle001"
  AttacherType = Attacher::AttachEngine3D
  Height = 36.5
  Length = 16
  Placement = pos=(-8,28,-48) rot=(0,0,1;0rad)
  Width = 7
FEATURE [Part::Cut] Cut001  label="Power_out_cut"
  Base = -> Box013
  Tool = -> Box014
FEATURE [Part::Cylinder] Cylinder004
  Angle = 360
  AttacherType = Attacher::AttachEngine3D
  FirstAngle = 0
  Height = 10
  Placement = pos=(61,31,27) rot=(0,0,1;0rad)
  Radius = 6.5
  SecondAngle = 0
FEATURE [Part::Cut] Cut002  label="Power_button_cut"
  Base = -> Cut001
  Tool = -> Cylinder004
FEATURE [Part::Cut] Cut006  label="Power_in_cut"
  Base = -> Cut002
  Tool = -> Box005
FEATURE [Part::Cut] Cut007  label="LAN_cut"
  Base = -> Cut006
  Tool = -> Box006
FEATURE [Part::Cylinder] Cylinder005  label="power_butt"
  Angle = 360
  AttacherType = Attacher::AttachEngine3D
  FirstAngle = 0
  Height = 10
  Placement = pos=(61,31,27) rot=(0,0,1;0rad)
  Radius = 6.25
  SecondAngle = 0
FEATURE [Part::Cylinder] Cylinder006
  Angle = 360
  AttacherType = Attacher::AttachEngine3D
  FirstAngle = 0
  Height = 3.25
  Placement = pos=(61,31.5,37) rot=(-1,0,0;1.5708rad)
  Radius = 0.25
  SecondAngle = 0
FEATURE [Part::Cylinder] Cylinder007
  Angle = 360
  AttacherType = Attacher::AttachEngine3D
  FirstAngle = 0
  Height = 10
  Placement = pos=(27,112,14.75) rot=(-1,0,0;1.5708rad)
  Radius = 6.35
  SecondAngle = 0
FEATURE [Part::Cylinder] Cylinder008
  Angle = 360
  AttacherType = Attacher::AttachEngine3D
  FirstAngle = 0
  Height = 10
  Placement = pos=(93,112,14.75) rot=(-1,0,0;1.5708rad)
  Radius = 6.35
  SecondAngle = 0
FEATURE [Part::Cylinder] Cylinder009
  Angle = 360
  AttacherType = Attacher::AttachEngine3D
  FirstAngle = 0
  Height = 3
  Placement = pos=(93,119,14.75) rot=(-1,0,0;1.5708rad)
  Radius = 5.85
  SecondAngle = 0
FEATURE [Part::Cut] Cut011  label="4g"
  Base = -> Cylinder008
  Tool = -> Cylinder009
FEATURE [Part::Cylinder] Cylinder010
  Angle = 360
  AttacherType = Attacher::AttachEngine3D
  FirstAngle = 0
  Height = 10
  Placement = pos=(92,10,10) rot=(1,0,0;1.5708rad)
  Radius = 1
  SecondAngle = 0
FEATURE [Part::Cylinder] Cylinder011
  Angle = 360
  AttacherType = Attacher::AttachEngine3D
  FirstAngle = 0
  Height = 10
  Placement = pos=(14.5,14.5,-2) rot=(0,0,1;0rad)
  Radius = 5.5
  SecondAngle = 0
FEATURE [Part::Cylinder] Cylinder012
  Angle = 360
  AttacherType = Attacher::AttachEngine3D
  FirstAngle = 0
  Height = 10
  Placement = pos=(14.5,14.5,-2.5) rot=(0,0,1;0rad)
  Radius = 4.5
  SecondAngle = 0
FEATURE [Part::Cylinder] Cylinder013
  Angle = 360
  AttacherType = Attacher::AttachEngine3D
  FirstAngle = 0
  Height = 10
  Placement = pos=(14.5,14.5,-2) rot=(0,0,1;0rad)
  Radius = 5.5
  SecondAngle = 0
FEATURE [Part::Cylinder] Cylinder014
  Angle = 360
  AttacherType = Attacher::AttachEngine3D
  FirstAngle = 0
  Height = 10
  Placement = pos=(14.5,14.5,-2.5) rot=(0,0,1;0rad)
  Radius = 4.5
  SecondAngle = 0
FEATURE [Part::Cylinder] Cylinder015
  Angle = 360
  AttacherType = Attacher::AttachEngine3D
  FirstAngle = 0
  Height = 10
  Placement = pos=(14.5,14.5,-2) rot=(0,0,1;0rad)
  Radius = 5.5
  SecondAngle = 0
FEATURE [Part::Cylinder] Cylinder016
  Angle = 360
  AttacherType = Attacher::AttachEngine3D
  FirstAngle = 0
  Height = 10
  Placement = pos=(14.5,14.5,-2.5) rot=(0,0,1;0rad)
  Radius = 4.5
  SecondAngle = 0
FEATURE [Part::Cylinder] Cylinder017
  Angle = 360
  AttacherType = Attacher::AttachEngine3D
  FirstAngle = 0
  Height = 10
  Placement = pos=(14.5,14.5,-2) rot=(0,0,1;0rad)
  Radius = 5.5
  SecondAngle = 0
FEATURE [Part::Cylinder] Cylinder018
  Angle = 360
  AttacherType = Attacher::AttachEngine3D
  FirstAngle = 0
  Height = 10
  Placement = pos=(14.5,14.5,-2.5) rot=(0,0,1;0rad)
  Radius = 4.5
  SecondAngle = 0
FEATURE [Part::Cylinder] Cylinder019  label="m3_l"
  Angle = 360
  AttacherType = Attacher::AttachEngine3D
  FirstAngle = 0
  Height = 15
  Placement = pos=(-59,160,-7) rot=(1,0,0;1.5708rad)
  Radius = 1.6
  SecondAngle = 0
FEATURE [Part::Cylinder] Cylinder020  label="m3_r"
  Angle = 360
  AttacherType = Attacher::AttachEngine3D
  FirstAngle = 0
  Height = 15
  Placement = pos=(59,160,-7) rot=(1,0,0;1.5708rad)
  Radius = 1.6
  SecondAngle = 0
FEATURE [Part::Cylinder] Cylinder021  label="m3_lm"
  Angle = 360
  AttacherType = Attacher::AttachEngine3D
  FirstAngle = 0
  Height = 15
  Placement = pos=(-22,160,-7) rot=(1,0,0;1.5708rad)
  Radius = 1.6
  SecondAngle = 0
FEATURE [Part::Cylinder] Cylinder022  label="m3_rm"
  Angle = 360
  AttacherType = Attacher::AttachEngine3D
  FirstAngle = 0
  Height = 15
  Placement = pos=(22,160,-7) rot=(1,0,0;1.5708rad)
  Radius = 1.6
  SecondAngle = 0
FEATURE [Part::Cylinder] Cylinder023  label="m3_l001"
  Angle = 360
  AttacherType = Attacher::AttachEngine3D
  FirstAngle = 0
  Height = 15
  Placement = pos=(-59,160,-7) rot=(1,0,0;1.5708rad)
  Radius = 1.6
  SecondAngle = 0
FEATURE [Part::Cylinder] Cylinder024  label="m3_r001"
  Angle = 360
  AttacherType = Attacher::AttachEngine3D
  FirstAngle = 0
  Height = 15
  Placement = pos=(59,160,-7) rot=(1,0,0;1.5708rad)
  Radius = 1.6
  SecondAngle = 0
FEATURE [Part::Cylinder] Cylinder025  label="m3_lm001"
  Angle = 360
  AttacherType = Attacher::AttachEngine3D
  FirstAngle = 0
  Height = 15
  Placement = pos=(-22,160,-7) rot=(1,0,0;1.5708rad)
  Radius = 1.6
  SecondAngle = 0
FEATURE [Part::Cylinder] Cylinder026  label="m3_rm001"
  Angle = 360
  AttacherType = Attacher::AttachEngine3D
  FirstAngle = 0
  Height = 15
  Placement = pos=(22,160,-7) rot=(1,0,0;1.5708rad)
  Radius = 1.6
  SecondAngle = 0
FEATURE [Part::Fillet] Fillet003  label="main_box"
  Base = -> Cut007
  EdgeLinks = -> Cut007 [Edge1,Edge2,Edge3,Edge4,Edge5,Edge6,Edge7,Edge12,Edge13,Edge15,Edge16,Edge25]
  Edges = 12 edges r=3: [Edge1,Edge2,Edge3,Edge4,Edge5,Edge6,Edge7,Edge12,Edge13,Edge15,Edge16,Edge25]
FEATURE [Part::Fillet] Fillet004  label="Key_hole"
  Base = -> Box007
  EdgeLinks = -> Box007 [Edge1,Edge3,Edge5,Edge7]
  Edges = 4 edges r=1: [Edge1,Edge3,Edge5,Edge7]
FEATURE [Part::Cut] Cut008  label="first_hole"
  Base = -> Fillet003
  Tool = -> Fillet004
FEATURE [Part::Fillet] Fillet005  label="Key_hole_mount"
  Base = -> Box016
  EdgeLinks = -> Box016 [Edge1,Edge3,Edge5,Edge7]
  Edges = 4 edges r=1: [Edge1,Edge3,Edge5,Edge7]
FEATURE [Part::Fillet] Fillet006  label="Key_hole001"
  Base = -> Box017
  EdgeLinks = -> Box017 [Edge1,Edge3,Edge5,Edge7]
  Edges = 4 edges r=1: [Edge1,Edge3,Edge5,Edge7]
  Placement = pos=(45,57.75,0) rot=(0,0,1;0rad)
FEATURE [Part::Cut] Cut009  label="Hole2"
  Base = -> Cut008
  Tool = -> Fillet006
FEATURE [Part::Fillet] Fillet007  label="Key_hole002"
  Base = -> Box018
  EdgeLinks = -> Box018 [Edge1,Edge3,Edge5,Edge7]
  Edges = 4 edges r=1: [Edge1,Edge3,Edge5,Edge7]
  Placement = pos=(45.1,57.85,0) rot=(0,0,1;0rad)
FEATURE [Part::Fillet] Fillet008
  Base = -> Box020
  EdgeLinks = -> Box020 [Edge2,Edge4,Edge6,Edge8]
  Edges = 4 edges r=1.2: [Edge2,Edge4,Edge6,Edge8]
  Placement = pos=(0,6,0) rot=(0,0,1;0rad)
FEATURE [Part::Cut] Cut012  label="USB-C_cut"
  Base = -> Box019
  Tool = -> Fillet008
FEATURE [Part::Cut] Cut013  label="RJ45_Cut"
  Base = -> Cut012
  Tool = -> Box021
FEATURE [Part::Fillet] Fillet009  label="USB_Hole"
  Base = -> Box022
  EdgeLinks = -> Box022 [Edge2,Edge4,Edge6,Edge8]
  Edges = 4 edges r=0.5: [Edge2,Edge4,Edge6,Edge8]
  Placement = pos=(64.5,0,6.5) rot=(0,0,1;0rad)
FEATURE [Part::Cut] Cut014  label="USB_Hole_Cut"
  Base = -> Cut013
  Tool = -> Fillet009
FEATURE [Part::Cut] Cut015  label="LED_Cut"
  Base = -> Cut014
  Tool = -> Cylinder010
FEATURE [Part::Cut] Cut016  label="sim_cut"
  Base = -> Cut015
  Tool = -> Box023
FEATURE [Part::Fillet] Fillet010  label="Box"
  Base = -> Cut016
  EdgeLinks = -> Cut016 [Edge1,Edge3,Edge6,Edge32]
  Edges = 4 edges r=9: [Edge1,Edge3,Edge6,Edge32]
FEATURE [Part::MultiFuse] Fusion002  label="base_pad003"
  Placement = pos=(89.5,0,0) rot=(0,0,1;0rad)
  Shapes = -> [Cylinder015,Cylinder016]
FEATURE [Part::MultiFuse] Fusion007
  Shapes = -> [Fillet005,Cut009,Fillet007]
FEATURE [Part::MultiFuse] Fusion008  label="base_pad001"
  Shapes = -> [Cylinder011,Cylinder012]
FEATURE [Part::MultiFuse] Fusion009  label="base_pad002"
  Placement = pos=(0,89.5,0) rot=(0,0,1;0rad)
  Shapes = -> [Cylinder013,Cylinder014]
FEATURE [Part::MultiFuse] Fusion010  label="base_pad004"
  Placement = pos=(89.5,89.5,0) rot=(0,0,1;0rad)
  Shapes = -> [Cylinder017,Cylinder018]
FEATURE [Part::MultiFuse] Fusion004  label="Gateway_box"
  Shapes = -> [Fillet010,Fusion008,Fusion009,Fusion002,Fusion010]
FEATURE [Part::Fillet] Fillet011  label="GateWay_Box"
  Base = -> Fusion004
  EdgeLinks = -> Fusion004 [Edge1,Edge3,Edge5,Edge6,Edge7,Edge8,Edge9,Edge10,Edge11,Edge12,Edge14,Edge15,Edge16,Edge17,Edge18,Edge19]
  Edges = 16 edges r=1: [Edge1,Edge3,Edge5,Edge6,Edge7,Edge8,Edge9,Edge10,Edge11,Edge12,Edge14,Edge15,Edge16,Edge17,Edge18,Edge19]
FEATURE [Part::MultiFuse] Fusion012  label="m3"
  Shapes = -> [Cylinder019,Cylinder020,Cylinder021,Cylinder022]
FEATURE [Part::MultiFuse] Fusion014  label="m3_screws"
  Shapes = -> [Cylinder023,Cylinder024,Cylinder025,Cylinder026]
FEATURE [Part::Feature] Part__Feature  label="Body"
  shape: bbox 30 x 26.75 x 29.35 mm, 109 faces (baked)
FEATURE [Part::Feature] Part__Feature001  label="Body001"
  Placement = pos=(9e-16,-2.285,-17.7) rot=(0,0,1;0rad)
  shape: bbox 9 x 0.5 x 14.6 mm, 20 faces (baked)
FEATURE [Part::Feature] Part__Feature002  label="Body002"
  Placement = pos=(4.25,5.59,0) rot=(0,0,1;1.5708rad)
  shape: bbox 0.5 x 9 x 14.6 mm, 20 faces (baked)
FEATURE [Part::Feature] Part__Feature003  label="Body003"
  Placement = pos=(-4.25,5.59,0) rot=(0,0,1;1.5708rad)
  shape: bbox 0.5 x 9 x 14.6 mm, 20 faces (baked)
FEATURE [Part::Feature] Part__Feature004  label="Solid1"
  shape: bbox 48.94 x 58.74 x 22.24 mm, 535 faces (baked)
FEATURE [Part::Cut] Cut003
  Base = -> Part__Feature004
  Tool = -> Box015
FEATURE [Part::Cut] Cut004
  Base = -> Cut003
  Tool = -> Box003
FEATURE [Part::Cut] Cut005
  Base = -> Cut004
  Tool = -> Box004
FEATURE [Part::Feature] Part__Feature005  label="Solid3"
  shape: bbox 2 x 4 x 20.28 mm, 13 faces (baked)
FEATURE [Part::Feature] Part__Feature006  label="Solid004"
  shape: bbox 2 x 4 x 17.28 mm, 13 faces (baked)
FEATURE [Part::Feature] Part__Feature007  label="Solid005"
  shape: bbox 2 x 4 x 17.28 mm, 13 faces (baked)
FEATURE [Part::Feature] Part__Feature008  label="Solid4"
  shape: bbox 5.5 x 5.5 x 8.5 mm, 23 faces (baked)
FEATURE [Part::Feature] Part__Feature009  label="Solid007"
  shape: bbox 5.5 x 5.5 x 8.5 mm, 23 faces (baked)
FEATURE [Part::Feature] Part__Feature010  label="Solid008"
  shape: bbox 5.5 x 5.5 x 8.5 mm, 23 faces (baked)
FEATURE [Part::Feature] Part__Feature011  label="Solid009"
  shape: bbox 5.769 x 18 x 0.5 mm, 12 faces (baked)
FEATURE [Part::Feature] Part__Feature012  label="FUSE"
  Placement = pos=(2.76516,20.0677,-12.471) rot=(1,0,0;1.5708rad)
  shape: bbox 5 x 7 x 11.27 mm, 51 faces (baked)
FEATURE [Part::Feature] Part__Feature013  label="FUSE001"
  Placement = pos=(2.76516,20.0677,-12.471) rot=(1,0,0;1.5708rad)
  shape: bbox 2 x 2 x 2.691 mm, 4 faces (baked)
FEATURE [Part::Feature] Part__Feature014  label="FUSE002"
  Placement = pos=(2.76516,20.0677,-12.471) rot=(1,0,0;1.5708rad)
  shape: bbox 5 x 7 x 13.96 mm, 54 faces (baked)
FEATURE [App::Part] FUSE  label="FUSE003"
  Group = -> [Part__Feature012,Part__Feature013,Part__Feature014]
  Origin = -> Origin024
FEATURE [Part::Feature] Part__Feature015  label="COMPOUND011"
  Placement = pos=(0,-0.0056,0.0002) rot=(0,0,1;0rad)
  shape: bbox 0.4 x 11.61 x 3.651 mm, 6 faces (baked)
FEATURE [Part::Feature] Part__Feature247  label="COMPOUND012"
  Placement = pos=(0,-0.0056,0.0002) rot=(0,0,1;0rad)
  shape: bbox 0.4 x 11.61 x 3.651 mm, 6 faces (baked)
FEATURE [Part::Feature] Part__Feature248  label="COMPOUND013"
  Placement = pos=(0,-0.0056,0.0002) rot=(0,0,1;0rad)
  shape: bbox 0.4 x 11.61 x 3.651 mm, 6 faces (baked)
FEATURE [Part::Feature] Part__Feature249  label="COMPOUND014"
  Placement = pos=(0,-0.0056,0.0002) rot=(0,0,1;0rad)
  shape: bbox 0.4 x 11.61 x 3.651 mm, 6 faces (baked)
FEATURE [Part::Feature] Part__Feature250  label="COMPOUND015"
  Placement = pos=(0,-0.0056,0.0002) rot=(0,0,1;0rad)
  shape: bbox 0.4 x 11.61 x 3.651 mm, 6 faces (baked)
FEATURE [Part::Feature] Part__Feature251  label="COMPOUND016"
  Placement = pos=(0,-0.0056,0.0002) rot=(0,0,1;0rad)
  shape: bbox 0.4 x 11.61 x 3.651 mm, 6 faces (baked)
FEATURE [Part::Feature] Part__Feature252  label="COMPOUND017"
  Placement = pos=(0,-0.0056,0.0002) rot=(0,0,1;0rad)
  shape: bbox 0.4 x 11.61 x 3.651 mm, 6 faces (baked)
FEATURE [Part::Feature] Part__Feature253  label="Solid2"
  shape: bbox 23.81 x 12.73 x 19.05 mm, 337 faces (baked)
FEATURE [Part::Feature] Part__Feature254  label="FUSE (1)"
  Placement = pos=(2.90467,-3.14305,-31.7578) rot=(0,0,1;0rad)
  shape: bbox 5 x 5.737 x 5.737 mm, 4 faces (baked)
FEATURE [Part::Feature] Part__Feature255  label="FUSE (1)001"
  Placement = pos=(2.90467,-3.14305,-31.7578) rot=(0,0,1;0rad)
  shape: bbox 5 x 5.737 x 5.737 mm, 4 faces (baked)
FEATURE [Part::Feature] Part__Feature256  label="FUSE (1)002"
  Placement = pos=(2.90467,-3.14305,-31.7578) rot=(0,0,1;0rad)
  shape: bbox 10 x 4.6 x 4.6 mm, 3 faces (baked)
FEATURE [Part::Feature] Part__Feature257  label="FUSE (1)003"
  Placement = pos=(2.90467,-3.14305,-31.7578) rot=(0,0,1;0rad)
  shape: bbox 10 x 0.5 x 0.5 mm, 3 faces (baked)
FEATURE [App::Part] FUSE__1_  label="FUSE (1)004"
  Group = -> [Part__Feature254,Part__Feature255,Part__Feature256,Part__Feature257]
  Origin = -> Origin025
FEATURE [Part::Feature] Part__Feature258  label="COMPOUND003"
  Placement = pos=(0,-0.0056,0.0002) rot=(0,0,1;0rad)
  shape: bbox 0.4 x 3.65 x 1.05 mm, 24 faces (baked)
FEATURE [Part::Feature] Part__Feature259  label="COMPOUND"
  Placement = pos=(0,-0.0056,0.0002) rot=(0,0,1;0rad)
  shape: bbox 18.9 x 15.9 x 13.25 mm, 232 faces (baked)
FEATURE [Part::Feature] Part__Feature260  label="COMPOUND001"
  Placement = pos=(0,-0.0056,0.0002) rot=(0,0,1;0rad)
  shape: bbox 0.4 x 3.65 x 1.05 mm, 24 faces (baked)
FEATURE [Part::Feature] Part__Feature261  label="COMPOUND002"
  Placement = pos=(0,-0.0056,0.0002) rot=(0,0,1;0rad)
  shape: bbox 0.4 x 3.65 x 1.05 mm, 24 faces (baked)
FEATURE [Part::Feature] Part__Feature262  label="COMPOUND004"
  Placement = pos=(0,-0.0056,0.0002) rot=(0,0,1;0rad)
  shape: bbox 0.4 x 3.65 x 1.05 mm, 24 faces (baked)
FEATURE [Part::Feature] Part__Feature263  label="COMPOUND005"
  Placement = pos=(0,-0.0056,0.0002) rot=(0,0,1;0rad)
  shape: bbox 0.4 x 3.65 x 1.05 mm, 24 faces (baked)
FEATURE [Part::Feature] Part__Feature264  label="COMPOUND006"
  Placement = pos=(0,-0.0056,0.0002) rot=(0,0,1;0rad)
  shape: bbox 0.4 x 3.65 x 1.05 mm, 24 faces (baked)
FEATURE [Part::Feature] Part__Feature265  label="COMPOUND007"
  Placement = pos=(0,-0.0056,0.0002) rot=(0,0,1;0rad)
  shape: bbox 0.4 x 3.65 x 1.05 mm, 24 faces (baked)
FEATURE [Part::Feature] Part__Feature266  label="COMPOUND008"
  Placement = pos=(0,-0.0056,0.0002) rot=(0,0,1;0rad)
  shape: bbox 0.4 x 3.65 x 1.05 mm, 24 faces (baked)
FEATURE [Part::Feature] Part__Feature267  label="COMPOUND009"
  Placement = pos=(0,-0.0056,0.0002) rot=(0,0,1;0rad)
  shape: bbox 15.81 x 15.25 x 13.95 mm, 39 faces (baked)
FEATURE [Part::Feature] Part__Feature268  label="COMPOUND010"
  Placement = pos=(0,-0.0056,0.0002) rot=(0,0,1;0rad)
  shape: bbox 0.4 x 11.61 x 3.651 mm, 6 faces (baked)
FEATURE [App::Part] COMPOUND  label="LAN"
  Group = -> [Part__Feature259,Part__Feature260,Part__Feature261,Part__Feature258,Part__Feature262,Part__Feature263,Part__Feature264,Part__Feature265,Part__Feature266,Part__Feature267,Part__Feature268,Part__Feature015,Part__Feature247,Part__Feature248,Part__Feature249,Part__Feature250,Part__Feature251,Part__Feature252]
  Origin = -> Origin008
  Placement = pos=(19.5,104.5,14.75) rot=(0,0,1;3.14159rad)
FEATURE [Part::Feature] Part__Feature269  label="USB3.1 TYPE-C 24PF-009 v6"
  shape: bbox 9.146 x 4.6 x 10.65 mm, 537 faces (baked)
FEATURE [Part::Feature] Part__Feature270  label="USB3.1 TYPE-C 24PF-009 v007"
  shape: bbox 8.34 x 3.8 x 10 mm, 300 faces (baked)
FEATURE [Part::Feature] Part__Feature271  label="USB3.1 TYPE-C 24PF-009 v008"
  shape: bbox 5.75 x 2.5 x 8.484 mm, 354 faces (baked)
FEATURE [Part::Feature] Part__Feature272  label="COMPOUND019"
  Placement = pos=(0,-0.0056,0.0002) rot=(0,0,1;0rad)
  shape: bbox 0.4 x 3.65 x 1.05 mm, 24 faces (baked)
FEATURE [Part::Feature] Part__Feature273  label="Antenna Mount"
  Placement = pos=(15,63,10.75) rot=(0,0,1;0rad)
  shape: bbox 9.247 x 12.26 x 8.009 mm, 76 faces (baked)
FEATURE [Part::Feature] Part__Feature274  label="COMPOUND020"
  Placement = pos=(0,-0.0056,0.0002) rot=(0,0,1;0rad)
  shape: bbox 18.9 x 15.9 x 13.25 mm, 232 faces (baked)
FEATURE [Part::Feature] Part__Feature275  label="COMPOUND021"
  Placement = pos=(0,-0.0056,0.0002) rot=(0,0,1;0rad)
  shape: bbox 0.4 x 3.65 x 1.05 mm, 24 faces (baked)
FEATURE [Part::Feature] Part__Feature276  label="COMPOUND022"
  Placement = pos=(0,-0.0056,0.0002) rot=(0,0,1;0rad)
  shape: bbox 0.4 x 3.65 x 1.05 mm, 24 faces (baked)
FEATURE [Part::Feature] Part__Feature277  label="COMPOUND023"
  Placement = pos=(0,-0.0056,0.0002) rot=(0,0,1;0rad)
  shape: bbox 0.4 x 3.65 x 1.05 mm, 24 faces (baked)
FEATURE [Part::Feature] Part__Feature278  label="COMPOUND024"
  Placement = pos=(0,-0.0056,0.0002) rot=(0,0,1;0rad)
  shape: bbox 0.4 x 3.65 x 1.05 mm, 24 faces (baked)
FEATURE [Part::Feature] Part__Feature279  label="COMPOUND025"
  Placement = pos=(0,-0.0056,0.0002) rot=(0,0,1;0rad)
  shape: bbox 0.4 x 3.65 x 1.05 mm, 24 faces (baked)
FEATURE [Part::Feature] Part__Feature280  label="COMPOUND026"
  Placement = pos=(0,-0.0056,0.0002) rot=(0,0,1;0rad)
  shape: bbox 0.4 x 3.65 x 1.05 mm, 24 faces (baked)
FEATURE [Part::Feature] Part__Feature281  label="COMPOUND027"
  Placement = pos=(0,-0.0056,0.0002) rot=(0,0,1;0rad)
  shape: bbox 0.4 x 3.65 x 1.05 mm, 24 faces (baked)
FEATURE [Part::Feature] Part__Feature282  label="COMPOUND028"
  Placement = pos=(0,-0.0056,0.0002) rot=(0,0,1;0rad)
  shape: bbox 15.81 x 15.25 x 13.95 mm, 39 faces (baked)
FEATURE [Part::Feature] Part__Feature283  label="COMPOUND029"
  Placement = pos=(0,-0.0056,0.0002) rot=(0,0,1;0rad)
  shape: bbox 0.4 x 11.61 x 3.651 mm, 6 faces (baked)
FEATURE [Part::Feature] Part__Feature284  label="COMPOUND030"
  Placement = pos=(0,-0.0056,0.0002) rot=(0,0,1;0rad)
  shape: bbox 0.4 x 11.61 x 3.651 mm, 6 faces (baked)
FEATURE [Part::Feature] Part__Feature285  label="COMPOUND031"
  Placement = pos=(0,-0.0056,0.0002) rot=(0,0,1;0rad)
  shape: bbox 0.4 x 11.61 x 3.651 mm, 6 faces (baked)
FEATURE [Part::Feature] Part__Feature286  label="COMPOUND032"
  Placement = pos=(0,-0.0056,0.0002) rot=(0,0,1;0rad)
  shape: bbox 0.4 x 11.61 x 3.651 mm, 6 faces (baked)
FEATURE [Part::Feature] Part__Feature287  label="COMPOUND033"
  Placement = pos=(0,-0.0056,0.0002) rot=(0,0,1;0rad)
  shape: bbox 0.4 x 11.61 x 3.651 mm, 6 faces (baked)
FEATURE [Part::Feature] Part__Feature288  label="COMPOUND034"
  Placement = pos=(0,-0.0056,0.0002) rot=(0,0,1;0rad)
  shape: bbox 0.4 x 11.61 x 3.651 mm, 6 faces (baked)
FEATURE [Part::Feature] Part__Feature289  label="COMPOUND035"
  Placement = pos=(0,-0.0056,0.0002) rot=(0,0,1;0rad)
  shape: bbox 0.4 x 11.61 x 3.651 mm, 6 faces (baked)
FEATURE [Part::Feature] Part__Feature290  label="COMPOUND036"
  Placement = pos=(0,-0.0056,0.0002) rot=(0,0,1;0rad)
  shape: bbox 0.4 x 11.61 x 3.651 mm, 6 faces (baked)
FEATURE [App::Part] COMPOUND001  label="COMPOUND018"
  Group = -> [Part__Feature274,Part__Feature275,Part__Feature276,Part__Feature272,Part__Feature277,Part__Feature278,Part__Feature279,Part__Feature280,Part__Feature281,Part__Feature282,Part__Feature283,Part__Feature284,Part__Feature285,Part__Feature286,Part__Feature287,Part__Feature288,Part__Feature289,Part__Feature290]
  Origin = -> Origin029
  Placement = pos=(48.5,5.5,19.25) rot=(0,1,0;3.14159rad)
FEATURE [Part::Feature] Part__Feature291  label="USB-type-A(USBR-A-S-F-O-VU)"
  Placement = pos=(71.75,7.25,6.75) rot=(1,0,0;1.5708rad)
  shape: bbox 18.32 x 19.2 x 7.2 mm, 244 faces (baked)
FEATURE [Sketcher::SketchObject] Sketch001
  ArcFitTolerance = 0
  FullyConstrained = true
  MakeInternals = false
  Placement = pos=(0,0,0) rot=(1,0,0;3.14159rad)
  sketch-geometry (18):
    g0: ArcOfCircle CenterX=10.5 CenterY=-21.5 CenterZ=0 NormalX=0 NormalY=0 NormalZ=1 AngleXU=0 Radius=1.875 StartAngle=1.5708 EndAngle=4.71239
    g1: LineSegment StartX=10.5 StartY=-23.375 StartZ=0 EndX=13.04 EndY=-23.375 EndZ=0
    g2: LineSegment StartX=13.0446 StartY=-19.625 StartZ=0 EndX=10.5 EndY=-19.625 EndZ=0
    g3: ArcOfCircle CenterX=21.5 CenterY=-21.5 CenterZ=0 NormalX=0 NormalY=0 NormalZ=1 AngleXU=0 Radius=1.875 StartAngle=4.71239 EndAngle=7.85398
    g4: LineSegment StartX=18.9564 StartY=-23.375 StartZ=0 EndX=21.5 EndY=-23.375 EndZ=0
    g5: LineSegment StartX=21.5 StartY=-19.625 StartZ=0 EndX=18.9554 EndY=-19.625 EndZ=0
    g6: ArcOfCircle CenterX=55.25 CenterY=-77.5 CenterZ=0 NormalX=0 NormalY=0 NormalZ=1 AngleXU=0 Radius=1.875 StartAngle=1.5708 EndAngle=4.71239
    g7: LineSegment StartX=55.25 StartY=-79.375 StartZ=0 EndX=57.7946 EndY=-79.375 EndZ=0
    g8: LineSegment StartX=57.7946 StartY=-75.625 StartZ=0 EndX=55.25 EndY=-75.625 EndZ=0
    g9: ArcOfCircle CenterX=66.25 CenterY=-77.5 CenterZ=0 NormalX=0 NormalY=0 NormalZ=1 AngleXU=0 Radius=1.875 StartAngle=4.71239 EndAngle=7.85398
    g10: LineSegment StartX=63.71 StartY=-79.375 StartZ=0 EndX=66.25 EndY=-79.375 EndZ=0
    g11: LineSegment StartX=66.25 StartY=-75.625 StartZ=0 EndX=63.7054 EndY=-75.625 EndZ=0
    g12: ArcOfCircle CenterX=60.75 CenterY=-77.5 CenterZ=0 NormalX=0 NormalY=0 NormalZ=1 AngleXU=0 Radius=3.5 StartAngle=0.565353 EndAngle=2.57624
    g13: ArcOfCircle CenterX=60.7523 CenterY=-77.5036 CenterZ=0 NormalX=0 NormalY=0 NormalZ=1 AngleXU=0 Radius=3.5 StartAngle=3.70572 EndAngle=5.71906
    g14: ArcOfCircle CenterX=16 CenterY=-21.5 CenterZ=0 NormalX=0 NormalY=0 NormalZ=1 AngleXU=0 Radius=3.5 StartAngle=0.565353 EndAngle=2.57624
    g15: ArcOfCircle CenterX=15.9982 CenterY=-21.5044 CenterZ=0 NormalX=0 NormalY=0 NormalZ=1 AngleXU=0 Radius=3.5 StartAngle=3.70545 EndAngle=5.71932
    g16: Circle CenterX=16 CenterY=-21.5 CenterZ=0 NormalX=0 NormalY=0 NormalZ=1 AngleXU=0 Radius=0.05
    g17: Circle CenterX=60.75 CenterY=-77.5 CenterZ=0 NormalX=0 NormalY=0 NormalZ=1 AngleXU=0 Radius=0.05
  constraints (52):
    c: Tangent(g0,g1) = -1.5708
    c: Tangent(g2,g0) = -1.5708
    c: Horizontal(g1)
    c: DistanceY(g0,g0) = 3.75
    c: Distance(g0,g-1) = 21.5
    c: Horizontal(g2)
    c: Tangent(g4,g3) = -1.5708
    c: Tangent(g3,g5) = -1.5708
    c: Horizontal(g4)
    c: Distance(g3,g3) = 3.75
    c: Distance(g3,g-1) = 21.5
    c: Horizontal(g5)
    c: Tangent(g6,g7) = -1.5708
    c: Tangent(g8,g6) = -1.5708
    c: Horizontal(g7)
    c: Tangent(g10,g9) = -1.5708
    c: Tangent(g9,g11) = -1.5708
    c: Horizontal(g10)
    c: Distance(g6,g-1) = 77.5
    c: Distance(g9,g-1) = 77.5
    c: Horizontal(g11)
    c: Distance(g9,g9) = 3.75
    c: Distance(g6,g6) = 3.75
    c: Horizontal(g8)
    c: Coincident(g12,g8)
    c: Coincident(g12,g11)
    c: Diameter(g12) = 7
    c: Coincident(g13,g7)
    c: Coincident(g13,g10)
    c: Diameter(g13) = 7
    c: Distance(g12,g-1) = 77.5
    c: Distance(g12,g-2) = 60.75
    c: Distance(g7,g8) = 3.75
    c: Distance(g9,g-2) = 66.25
    c: Distance(g6,g-2) = 55.25
    c: Distance(g10,g-2) = 63.71
    c: Coincident(g14,g2)
    c: Coincident(g14,g5)
    c: Coincident(g15,g1)
    c: Coincident(g15,g4)
    c: Diameter(g14) = 7
    c: Diameter(g15) = 7
    c: Distance(g14,g-1) = 21.5
    c: Distance(g14,g-2) = 16
    c: Distance(g1,g-2) = 13.04
    c: Distance(g0,g-2) = 10.5
    c: Distance(g3,g-2) = 21.5
    c: Distance(g4,g3) = 3.16
    c: Coincident(g16,g14)
    c: Diameter(g16) = 0.1
    c: Coincident(g17,g12)
    c: Diameter(g17) = 0.1
FEATURE [Part::Extrusion] Extrude001
  Base = -> Sketch001
  Dir = (0,0,-1)
  DirMode = 2
  FaceMakerClass = Part::FaceMakerBullseye
  FaceMakerMode = 3
  LengthFwd = 2
  LengthRev = 0
  Placement = pos=(0,0,2) rot=(0,0,1;0rad)
  Solid = true
  Symmetric = false
FEATURE [Part::Cut] Cut010
  Base = -> Fusion007
  Tool = -> Extrude001
FEATURE [Sketcher::SketchObject] Sketch002
  ArcFitTolerance = 0
  FullyConstrained = true
  MakeInternals = false
  sketch-geometry (16):
    g0: LineSegment StartX=-65 StartY=157.37 StartZ=0 EndX=65 EndY=157.37 EndZ=0
    g1: LineSegment StartX=-65 StartY=157.37 StartZ=0 EndX=-65 EndY=147.37 EndZ=0
    g2: LineSegment StartX=-65 StartY=147.37 StartZ=0 EndX=-45.68 EndY=147.37 EndZ=0
    g3: LineSegment StartX=-45.68 StartY=147.37 StartZ=0 EndX=-45.68 EndY=70.37 EndZ=0
    g4: LineSegment StartX=-45.68 StartY=70.37 StartZ=0 EndX=-35.68 EndY=70.37 EndZ=0
    g5: LineSegment StartX=-35.68 StartY=70.37 StartZ=0 EndX=-35.68 EndY=147.37 EndZ=0
    g6: LineSegment StartX=-35.68 StartY=147.37 StartZ=0 EndX=-8 EndY=147.37 EndZ=0
    g7: LineSegment StartX=-8 StartY=147.37 StartZ=0 EndX=-8 EndY=70.37 EndZ=0
    g8: LineSegment StartX=-8 StartY=70.37 StartZ=0 EndX=8 EndY=70.37 EndZ=0
    g9: LineSegment StartX=8 StartY=70.37 StartZ=0 EndX=8 EndY=147.37 EndZ=0
    g10: LineSegment StartX=8 StartY=147.37 StartZ=0 EndX=35.68 EndY=147.37 EndZ=0
    g11: LineSegment StartX=35.68 StartY=147.37 StartZ=0 EndX=35.68 EndY=70.37 EndZ=0
    g12: LineSegment StartX=35.68 StartY=70.37 StartZ=0 EndX=45.68 EndY=70.37 EndZ=0
    g13: LineSegment StartX=45.68 StartY=70.37 StartZ=0 EndX=45.68 EndY=147.37 EndZ=0
    g14: LineSegment StartX=45.68 StartY=147.37 StartZ=0 EndX=65 EndY=147.37 EndZ=0
    g15: LineSegment StartX=65 StartY=147.37 StartZ=0 EndX=65 EndY=157.37 EndZ=0
  constraints (44):
    c: Symmetric(g0,g0,g-2)
    c: Distance(g0) = 130
    c: Coincident(g1,g0)
    c: Vertical(g1)
    c: Coincident(g2,g1)
    c: Horizontal(g2)
    c: Vertical(g3)
    c: Coincident(g4,g3)
    c: Horizontal(g4)
    c: Coincident(g5,g4)
    c: Vertical(g5)
    c: Coincident(g6,g5)
    c: Horizontal(g6)
    c: Coincident(g7,g6)
    c: Vertical(g7)
    c: Coincident(g8,g7)
    c: Horizontal(g8)
    c: Coincident(g9,g8)
    c: Vertical(g9)
    c: Coincident(g10,g9)
    c: Coincident(g11,g10)
    c: Vertical(g11)
    c: Coincident(g12,g11)
    c: Horizontal(g12)
    c: Coincident(g13,g12)
    c: Vertical(g13)
    c: Coincident(g14,g13)
    c: Horizontal(g14)
    c: Coincident(g15,g14)
    c: Coincident(g15,g0)
    c: Vertical(g15)
    c: Symmetric(g6,g9,g-2)
    c: Symmetric(g5,g10,g-2)
    c: Symmetric(g2,g13,g-2)
    c: Coincident(g2,g3)
    c: Distance(g2,g0) = 10
    c: Distance(g5,g0) = 10
    c: Distance(g3) = 77
    c: Distance(g4) = 10
    c: Distance(g8) = 16
    c: Distance(g9) = 77
    c: Distance(g13) = 77
    c: Distance(g1,g-1) = 147.37
    c: Distance(g3,g-2) = 45.68
FEATURE [Part::Extrusion] Extrude002  label="Side__hold"
  Base = -> Sketch002
  Dir = (0,0,1)
  DirMode = 2
  FaceMakerClass = Part::FaceMakerBullseye
  FaceMakerMode = 3
  LengthFwd = 10
  LengthRev = 0
  Placement = pos=(0,0.63,-1.5) rot=(0,0,1;0rad)
  Reversed = true
  Solid = true
  Symmetric = false
FEATURE [Part::MultiFuse] Fusion011  label="Holder"
  Shapes = -> [Extrude002,Box024,Box025,Box026,Box027,Box028]
FEATURE [Part::Fillet] Fillet012  label="Holder_fillet"
  Base = -> Fusion011
  EdgeLinks = -> Fusion011 [Edge1,Edge2,Edge3,Edge7,Edge8,Edge10,Edge11,Edge13,Edge14,Edge15,Edge16,Edge17,Edge18,Edge19,Edge20,Edge21,Edge22,Edge23,Edge24,Edge25,Edge26,Edge28,Edge29,Edge32,Edge36,Edge40,Edge43,Edge44,Edge45,Edge47,Edge49,Edge50,Edge51,Edge53,Edge54,Edge59,Edge61,Edge66,Edge68,Edge74,+15 more]
  Edges = 55 edges: [Edge1 r=1,Edge2 r=1,Edge3 r=1,Edge7 r=1,Edge8 r=4,Edge10 r=1,Edge11 r=4,Edge13 r=1,Edge14 r=1,Edge15 r=4,Edge16 r=1,Edge17 r=1,Edge18 r=1,Edge19 r=4,Edge20 r=1,Edge21 r=1,Edge22 r=1,Edge23 r=4,Edge24 r=1,Edge25 r=1,Edge26 r=1,Edge28 r=1,Edge29 r=4,Edge32 r=3,Edge36 r=3,Edge40 r=3,Edge43 r=4,Edge44 r=1,Edge45 r=1,Edge47 r=4,Edge49 r=1,Edge50 r=1,Edge51 r=4,Edge53 r=1,Edge54 r=1,Edge59 r=4,Edge61 r=4,Edge66 r=4,Edge68 r=4,Edge74 r=1,Edge75 r=1,Edge78 r=1,Edge79 r=1,Edge82 r=1,Edge85 r=1,Edge88 r=1,Edge90 r=1,Edge91 r=1,Edge93 r=1,Edge95 r=1,Edge96 r=1,Edge98 r=1,Edge100 r=1,Edge101 r=1,+1 more]
FEATURE [Part::Cut] Cut017  label="eZ_Holder"
  Base = -> Fillet012
  Tool = -> Fusion012
FEATURE [App::Part] Part006  label="ezOutlet_holder"
  Group = -> [Box026,Fillet012,Fusion011,Cylinder020,Cylinder019,Cylinder021,Cylinder022,Extrude002,Box028,Fusion012,Box024,Box027,Box025,Sketch002,Cut017]
  Origin = -> Origin030
  Placement = pos=(0,0,-157) rot=(0,0,1;0rad)
FEATURE [Sketcher::SketchObject] Sketch003
  ArcFitTolerance = 0
  FullyConstrained = true
  MakeInternals = false
  sketch-geometry (16):
    g0: LineSegment StartX=-70.5 StartY=157.37 StartZ=0 EndX=70.5 EndY=157.37 EndZ=0
    g1: LineSegment StartX=-70.5 StartY=157.37 StartZ=0 EndX=-70.5 EndY=147.37 EndZ=0
    g2: LineSegment StartX=-70.5 StartY=147.37 StartZ=0 EndX=-50 EndY=147.37 EndZ=0
    g3: LineSegment StartX=-50 StartY=147.37 StartZ=0 EndX=-50 EndY=27.37 EndZ=0
    g4: LineSegment StartX=-50 StartY=27.37 StartZ=0 EndX=-35 EndY=27.37 EndZ=0
    g5: LineSegment StartX=-35 StartY=27.37 StartZ=0 EndX=-35 EndY=147.37 EndZ=0
    g6: LineSegment StartX=-35 StartY=147.37 StartZ=0 EndX=-8 EndY=147.37 EndZ=0
    g7: LineSegment StartX=-8 StartY=147.37 StartZ=0 EndX=-8 EndY=27.37 EndZ=0
    g8: LineSegment StartX=-8 StartY=27.37 StartZ=0 EndX=8 EndY=27.37 EndZ=0
    g9: LineSegment StartX=8 StartY=27.37 StartZ=0 EndX=8 EndY=147.37 EndZ=0
    g10: LineSegment StartX=8 StartY=147.37 StartZ=0 EndX=35 EndY=147.37 EndZ=0
    g11: LineSegment StartX=35 StartY=147.37 StartZ=0 EndX=35 EndY=27.37 EndZ=0
    g12: LineSegment StartX=35 StartY=27.37 StartZ=0 EndX=50 EndY=27.37 EndZ=0
    g13: LineSegment StartX=50 StartY=27.37 StartZ=0 EndX=50 EndY=147.37 EndZ=0
    g14: LineSegment StartX=50 StartY=147.37 StartZ=0 EndX=70.5 EndY=147.37 EndZ=0
    g15: LineSegment StartX=70.5 StartY=147.37 StartZ=0 EndX=70.5 EndY=157.37 EndZ=0
  constraints (44):
    c: Symmetric(g0,g0,g-2)
    c: Distance(g0) = 141
    c: Coincident(g1,g0)
    c: Vertical(g1)
    c: Coincident(g2,g1)
    c: Horizontal(g2)
    c: Vertical(g3)
    c: Coincident(g4,g3)
    c: Horizontal(g4)
    c: Coincident(g5,g4)
    c: Vertical(g5)
    c: Coincident(g6,g5)
    c: Horizontal(g6)
    c: Coincident(g7,g6)
    c: Vertical(g7)
    c: Coincident(g8,g7)
    c: Horizontal(g8)
    c: Coincident(g9,g8)
    c: Vertical(g9)
    c: Coincident(g10,g9)
    c: Coincident(g11,g10)
    c: Vertical(g11)
    c: Coincident(g12,g11)
    c: Horizontal(g12)
    c: Coincident(g13,g12)
    c: Vertical(g13)
    c: Coincident(g14,g13)
    c: Horizontal(g14)
    c: Coincident(g15,g14)
    c: Coincident(g15,g0)
    c: Vertical(g15)
    c: Symmetric(g6,g9,g-2)
    c: Symmetric(g5,g10,g-2)
    c: Symmetric(g2,g13,g-2)
    c: Coincident(g2,g3)
    c: Distance(g2,g0) = 10
    c: Distance(g5,g0) = 10
    c: Distance(g3) = 120
    c: Distance(g4) = 15
    c: Distance(g8) = 16
    c: Distance(g9) = 120
    c: Distance(g13) = 120
    c: Distance(g1,g-1) = 147.37
    c: Distance(g3,g-2) = 50
FEATURE [Part::Extrusion] Extrude003  label="Side__hold001"
  Base = -> Sketch003
  Dir = (0,0,1)
  DirMode = 2
  FaceMakerClass = Part::FaceMakerBullseye
  FaceMakerMode = 3
  LengthFwd = 10
  LengthRev = 0
  Placement = pos=(0,0.63,-1.5) rot=(0,0,1;0rad)
  Reversed = true
  Solid = true
  Symmetric = false
FEATURE [Part::MultiFuse] Fusion013  label="Holder_gateway"
  Shapes = -> [Extrude003,Box029,Box030,Box031,Box032,Box033]
FEATURE [Part::Cut] Cut018  label="Holder_m3_cut"
  Base = -> Fusion013
  Tool = -> Fusion014
FEATURE [Part::Fillet] Fillet013  label="GateWay_Holder"
  Base = -> Cut018
  EdgeLinks = -> Cut018 [Edge1,Edge2,Edge4,Edge12,Edge14,Edge15,Edge16,Edge17,Edge18,Edge19,Edge20,Edge21,Edge22,Edge23,Edge24,Edge25,Edge26,Edge27,Edge28,Edge30,Edge48,Edge49,Edge60,Edge61,Edge63,Edge64,Edge70,Edge72,Edge77,Edge79,Edge85,Edge86,Edge89,Edge91,Edge94,Edge95,Edge98,Edge101,Edge104,Edge105,+10 more]
  Edges = 50 edges: [Edge1 r=1,Edge2 r=1,Edge4 r=1,Edge12 r=4,Edge14 r=4,Edge15 r=1,Edge16 r=1,Edge17 r=4,Edge18 r=1,Edge19 r=1,Edge20 r=1,Edge21 r=4,Edge22 r=1,Edge23 r=1,Edge24 r=1,Edge25 r=4,Edge26 r=1,Edge27 r=1,Edge28 r=1,Edge30 r=1,Edge48 r=1,Edge49 r=1,Edge60 r=4,Edge61 r=1,Edge63 r=1,Edge64 r=4,Edge70 r=4,Edge72 r=4,Edge77 r=4,Edge79 r=4,Edge85 r=1,Edge86 r=1,Edge89 r=1,Edge91 r=1,Edge94 r=1,Edge95 r=1,Edge98 r=1,Edge101 r=1,Edge104 r=1,Edge105 r=4,Edge106 r=4,Edge108 r=1,Edge109 r=1,Edge111 r=1,Edge113 r=1,Edge114 r=1,Edge116 r=1,Edge118 r=1,Edge119 r=1,Edge121 r=1]
FEATURE [App::Part] Part007  label="LoRa_Gateway_holder"
  Group = -> [Cylinder024,Cylinder026,Cylinder023,Cylinder025,Extrude003,Fusion013,Fusion014,Sketch003,Box030,Box029,Box031,Box033,Box032,Cut018,Fillet013]
  Origin = -> Origin031
  Placement = pos=(132.3,0,-10) rot=(0,1,0;4.71239rad)
FEATURE [App::Part] Solid3  label="Solid006"
  Group = -> [Part__Feature005,Part__Feature006,Part__Feature007]
  Origin = -> Origin002
FEATURE [App::Part] Solid4  label="Solid010"
  Group = -> [Part__Feature008,Part__Feature009,Part__Feature010,Part__Feature011]
  Origin = -> Origin023
FEATURE [Part::Torus] Torus
  Angle1 = -180
  Angle2 = 180
  Angle3 = 290
  AttacherType = Attacher::AttachEngine3D
  Placement = pos=(61,31,37) rot=(0,0,1;2.18166rad)
  Radius1 = 3
  Radius2 = 0.25
FEATURE [Part::MultiFuse] Fusion006  label="Power_button"
  Shapes = -> [Torus,Cylinder005]
FEATURE [App::Part] USB3_1_TYPE_C_24PF_009_v6  label="USB3.1 TYPE-C 24PF-009 v009"
  Group = -> [Part__Feature269,Part__Feature270,Part__Feature271]
  Origin = -> Origin028
  Placement = pos=(26,9.3,7.5) rot=(1,0,0;1.5708rad)
FEATURE [App::Part] Part005  label="LoRa_Gateway"
  Group = -> [Cylinder007,Part__Feature273,Cylinder009,Cylinder008,Cut011,USB3_1_TYPE_C_24PF_009_v6,COMPOUND001,Part__Feature291,Box021,Box019,Cut015,Cut012,Cut016,Box020,Cylinder010,Cylinder012,Cylinder011,Cylinder017,Cylinder013,Cylinder014,Cylinder015,Cylinder016,Cylinder018,Box023,Fusion010,Box022,Fillet010,Fillet009,Cut013,Fusion002,Cut014,Fusion008,Fusion009,Fillet008,Fusion004,Fillet011]
  Origin = -> Origin027
  Placement = pos=(174,156,-70) rot=(0.57735,-0.57735,-0.57735;2.0944rad)
FEATURE [App::Part] Unnamed1  label="Power_out"
  Group = -> [Part__Feature,Part__Feature001,Part__Feature002,Part__Feature003]
  Origin = -> Origin022
  Placement = pos=(39.25,1.75,18.5) rot=(-0.57735,-0.57735,0.57735;4.18879rad)
FEATURE [App::Part] power_input_swuitch  label="power input swuitch"
  Group = -> [Solid3,Solid4,FUSE,Part__Feature253,FUSE__1_,Cut004,Cut003,Box015,Part__Feature004,Box004,Box003,Cut005]
  Origin = -> Origin026
  Placement = pos=(39.25,109,18.5) rot=(-0.57735,-0.57735,-0.57735;2.0944rad)
FEATURE [App::Part] Part004  label="eZOutlet5"
  Group = -> [Unnamed1,Cylinder006,Torus,Cylinder005,Fusion006,power_input_swuitch,COMPOUND,Cut006,Fillet003,Fillet005,Fillet006,Fillet007,Sketch001,Box006,Box007,Box018,Box016,Box017,Extrude001,Fillet004,Cut008,Cut009,Cut007,Box014,Box005,Box013,Cut001,Cut002,Fusion007,Cylinder004,Cut010]
  Origin = -> Origin
  Placement = pos=(54.5,79,-206) rot=(0,0,1;1.5708rad)
FEATURE [Part::Feature] Part__Feature195  label="CUI_VGS-25W-060"
  shape: bbox 6 x 13.55 x 11.3 mm, 86 faces (baked)
FEATURE [Part::Feature] Part__Feature196  label="CUI_VGS-25W-061"
  shape: bbox 55.03 x 25.15 x 80 mm, 254 faces (baked)
FEATURE [Part::Feature] Part__Feature197  label="CUI_VGS-25W-062"
  shape: bbox 7.911 x 7.911 x 1.162 mm, 68 faces (baked)
FEATURE [Part::Feature] Part__Feature198  label="CUI_VGS-25W-063"
  shape: bbox 5.629 x 5.629 x 8.001 mm, 43 faces (baked)
FEATURE [Part::Feature] Part__Feature199  label="CUI_VGS-25W-064"
  shape: bbox 4.944 x 5.8 x 5.8 mm, 37 faces (baked)
FEATURE [Part::Feature] Part__Feature200  label="CUI_VGS-25W-065"
  shape: bbox 6 x 13.55 x 11.3 mm, 86 faces (baked)
FEATURE [Part::Feature] Part__Feature201  label="CUI_VGS-25W-066"
  shape: bbox 5.629 x 5.629 x 8.001 mm, 43 faces (baked)
FEATURE [Part::Feature] Part__Feature202  label="CUI_VGS-25W-067"
  shape: bbox 39.6 x 12 x 16 mm, 290 faces (baked)
FEATURE [Part::Feature] Part__Feature203  label="CUI_VGS-25W-068"
  shape: bbox 5.443 x 12.7 x 3.793 mm, 44 faces (baked)
FEATURE [Part::Feature] Part__Feature204  label="CUI_VGS-25W-069"
  shape: bbox 54.37 x 24.2 x 80.19 mm, 487 faces (baked)
FEATURE [Part::Feature] Part__Feature205  label="CUI_VGS-25W-070"
  shape: bbox 6 x 13.55 x 11.3 mm, 86 faces (baked)
FEATURE [Part::Feature] Part__Feature206  label="CUI_VGS-25W-071"
  shape: bbox 5.413 x 8.147 x 5.557 mm, 54 faces (baked)
FEATURE [Part::Feature] Part__Feature207  label="CUI_VGS-25W-072"
  shape: bbox 6 x 13.55 x 11.3 mm, 86 faces (baked)
FEATURE [Part::Feature] Part__Feature208  label="CUI_VGS-25W-073"
  shape: bbox 9.096 x 12.71 x 7.718 mm, 112 faces (baked)
FEATURE [Part::Feature] Part__Feature209  label="CUI_VGS-25W-074"
  shape: bbox 6 x 13.55 x 11.3 mm, 86 faces (baked)
FEATURE [Part::Feature] Part__Feature210  label="CUI_VGS-25W-075"
  shape: bbox 5.629 x 5.629 x 8.001 mm, 43 faces (baked)
FEATURE [Part::Feature] Part__Feature211  label="CUI_VGS-25W-076"
  shape: bbox 5.629 x 5.629 x 8.001 mm, 43 faces (baked)
FEATURE [Part::Feature] Part__Feature212  label="CUI_VGS-25W-077"
  shape: bbox 7.911 x 7.911 x 1.162 mm, 68 faces (baked)
FEATURE [Part::Feature] Part__Feature213  label="CUI_VGS-25W-078"
  shape: bbox 7.911 x 7.911 x 1.162 mm, 68 faces (baked)
FEATURE [Part::Feature] Part__Feature214  label="CUI_VGS-25W-079"
  shape: bbox 7 x 0.55 x 7 mm, 6 faces (baked)
FEATURE [Part::Feature] Part__Feature215  label="CUI_VGS-25W-080"
  shape: bbox 53.1 x 22.4 x 79.2 mm, 72 faces (baked)
FEATURE [Part::Feature] Part__Feature216  label="CUI_VGS-25W-081"
  shape: bbox 4.624 x 1.433 x 4.618 mm, 8 faces (baked)
FEATURE [Part::Feature] Part__Feature217  label="CUI_VGS-25W-082"
  shape: bbox 7.911 x 7.911 x 1.162 mm, 68 faces (baked)
FEATURE [Part::Feature] Part__Feature218  label="CUI_VGS-25W-083"
  shape: bbox 5.629 x 5.629 x 8.001 mm, 43 faces (baked)
FEATURE [Part::Feature] Part__Feature219  label="CUI_VGS-25W-084"
  shape: bbox 52.65 x 1.621 x 78.18 mm, 385 faces (baked)
FEATURE [Part::Feature] Part__Feature220  label="CUI_VGS-25W-085"
  shape: bbox 7.911 x 7.911 x 1.162 mm, 68 faces (baked)
FEATURE [App::Part] CUI_VGS_25W_007  label="CUI_VGS-25W-01"
  Group = -> [Part__Feature201,Part__Feature202,Part__Feature203,Part__Feature204,Part__Feature205,Part__Feature206,Part__Feature207,Part__Feature208,Part__Feature209,Part__Feature210,Part__Feature195,Part__Feature196,Part__Feature197,Part__Feature198,Part__Feature199,Part__Feature200,Part__Feature211,Part__Feature212,Part__Feature213,Part__Feature214,Part__Feature217,Part__Feature215,Part__Feature216,+3 more]
  Origin = -> Origin020
  Placement = pos=(22.5,-50.5,0.25) rot=(1,0,0;1.5708rad)
FEATURE [Sketcher::SketchObject] Sketch004
  ArcFitTolerance = 1e-06
  FullyConstrained = true
  MakeInternals = false
  Placement = pos=(0,0,0) rot=(1,0,0;1.5708rad)
  sketch-geometry (6):
    g0: LineSegment StartX=25 StartY=0 StartZ=0 EndX=25 EndY=-4 EndZ=0
    g1: LineSegment StartX=25 StartY=-4 StartZ=0 EndX=59.5 EndY=-4 EndZ=0
    g2: LineSegment StartX=59.5 StartY=-4 StartZ=0 EndX=59.5 EndY=21 EndZ=0
    g3: LineSegment StartX=59.5 StartY=21 StartZ=0 EndX=55.5 EndY=21 EndZ=0
    g4: LineSegment StartX=55.5 StartY=21 StartZ=0 EndX=55.5 EndY=0 EndZ=0
    g5: LineSegment StartX=55.5 StartY=0 StartZ=0 EndX=25 EndY=0 EndZ=0
  constraints (18):
    c: Coincident(g1,g0)
    c: Horizontal(g1)
    c: Vertical(g2)
    c: Coincident(g3,g2)
    c: Horizontal(g3)
    c: PointOnObject(g4,g-1)
    c: Vertical(g4)
    c: Coincident(g5,g4)
    c: Coincident(g5,g0)
    c: Horizontal(g5)
    c: Vertical(g0)
    c: Coincident(g1,g2)
    c: DistanceX(g0) = 25
    c: DistanceX(g5,g5) = 30.5
    c: DistanceX(g3,g3) = 4
    c: Coincident(g3,g4)
    c: DistanceY(g0,g0) = 4
    c: DistanceY(g2,g2) = 25
FEATURE [Part::Extrusion] Extrude004
  Base = -> Sketch004
  Dir = (0,-1,2e-16)
  DirMode = 2
  FaceMakerClass = Part::FaceMakerBullseye
  FaceMakerMode = 3
  LengthFwd = 20
  LengthRev = 0
  Solid = true
  Symmetric = false
FEATURE [Sketcher::SketchObject] Sketch005
  ArcFitTolerance = 1e-06
  FullyConstrained = true
  MakeInternals = false
  Placement = pos=(0,0,0) rot=(1,0,0;1.5708rad)
  sketch-geometry (6):
    g0: LineSegment StartX=73 StartY=21 StartZ=0 EndX=25 EndY=21 EndZ=0
    g1: LineSegment StartX=25 StartY=21 StartZ=0 EndX=25 EndY=-4 EndZ=0
    g2: LineSegment StartX=25 StartY=-4 StartZ=0 EndX=73 EndY=-4 EndZ=0
    g3: LineSegment StartX=73 StartY=-4 StartZ=0 EndX=73 EndY=21 EndZ=0
    g4: Circle CenterX=67 CenterY=15 CenterZ=0 NormalX=0 NormalY=0 NormalZ=1 AngleXU=0 Radius=1.625
    g5: Circle CenterX=67 CenterY=2 CenterZ=0 NormalX=0 NormalY=0 NormalZ=1 AngleXU=0 Radius=1.625
  constraints (18):
    c: Horizontal(g0)
    c: Vertical(g1)
    c: DistanceX(g0,g0) = 48
    c: DistanceX(g1) = 25
    c: Coincident(g2,g1)
    c: Coincident(g3,g2)
    c: Coincident(g3,g0)
    c: Vertical(g3)
    c: DistanceY(g1,g1) = 25
    c: Horizontal(g2)
    c: DistanceY(g1) = -4
    c: Coincident(g0,g1)
    c: Equal(g4,g5)
    c: Diameter(g4) = 3.25
    c: Vertical(g5,g4)
    c: DistanceY(g1,g5) = 6
    c: DistanceY(g5,g4) = 13
    c: DistanceX(g1,g5) = 42
FEATURE [Part::Extrusion] Extrude005
  Base = -> Sketch005
  Dir = (0,-1,2e-16)
  DirMode = 2
  FaceMakerClass = Part::FaceMakerBullseye
  FaceMakerMode = 3
  LengthFwd = 5
  LengthRev = 0
  Solid = true
  Symmetric = false
FEATURE [Part::MultiFuse] Fusion015
  Shapes = -> [Extrude005,Extrude004]
FEATURE [Sketcher::SketchObject] Sketch006
  ArcFitTolerance = 1e-06
  FullyConstrained = true
  MakeInternals = false
  sketch-geometry (1):
    g0: Circle CenterX=29.75 CenterY=-15.85 CenterZ=0 NormalX=0 NormalY=0 NormalZ=1 AngleXU=0 Radius=1.625
  constraints (3):
    c: DistanceX(g0) = 29.75
    c: DistanceY(g0) = -15.85
    c: Diameter(g0) = 3.25
FEATURE [Part::Extrusion] Extrude006
  Base = -> Sketch006
  Dir = (0,0,1)
  DirMode = 2
  FaceMakerClass = Part::FaceMakerBullseye
  FaceMakerMode = 3
  LengthFwd = 10
  LengthRev = 0
  Reversed = true
  Solid = true
  Symmetric = false
FEATURE [Sketcher::SketchObject] Sketch007
  ArcFitTolerance = 1e-06
  FullyConstrained = true
  MakeInternals = false
  Placement = pos=(0,0,0) rot=(0.57735,0.57735,0.57735;2.0944rad)
  sketch-geometry (1):
    g0: Circle CenterX=-8.1 CenterY=14.25 CenterZ=0 NormalX=0 NormalY=0 NormalZ=1 AngleXU=0 Radius=1.625
  constraints (3):
    c: DistanceX(g0) = -8.1
    c: DistanceY(g0) = 14.25
    c: Diameter(g0) = 3.25
FEATURE [Part::Extrusion] Extrude007
  Base = -> Sketch007
  Dir = (1,0,0)
  DirMode = 2
  FaceMakerClass = Part::FaceMakerBullseye
  FaceMakerMode = 3
  LengthFwd = 75
  LengthRev = 0
  Solid = true
  Symmetric = false
FEATURE [Part::MultiFuse] Fusion016  label="cuts"
  Shapes = -> [Extrude006,Extrude007]
FEATURE [Part::Cut] Cut019
  Base = -> Fusion015
  Tool = -> Fusion016
FEATURE [Part::Fillet] Fillet014
  Base = -> Cut019
  EdgeLinks = -> Cut019 [Edge30,Edge33,Edge44,Edge46,Edge47,Edge48]
  Edges = 6 edges r=1: [Edge30,Edge33,Edge44,Edge46,Edge47,Edge48]
FEATURE [Part::Fillet] Fillet001
  Base = -> Fillet014
  EdgeLinks = -> Fillet014 [Edge41,Edge47,Edge48]
  Edges = 3 edges r=1: [Edge41,Edge47,Edge48]
FEATURE [Part::Fillet] Fillet002
  Base = -> Fillet001
  EdgeLinks = -> Fillet001 [Edge15,Edge38,Edge46,Edge47]
  Edges = 4 edges r=0.25: [Edge15,Edge38,Edge46,Edge47]
FEATURE [Part::Compound] Compound  label="5vHolder"
  Links = -> [CUI_VGS_25W_007,Fillet002]
  Placement = pos=(130,158,-24.5) rot=(0,1,0;1.5708rad)
FEATURE [Part::Feature] Part__Feature292  label="CUI_VGS-25W-087"
  shape: bbox 6 x 13.55 x 11.3 mm, 86 faces (baked)
FEATURE [Part::Feature] Part__Feature293  label="CUI_VGS-25W-088"
  shape: bbox 55.03 x 25.15 x 80 mm, 254 faces (baked)
FEATURE [Part::Feature] Part__Feature294  label="CUI_VGS-25W-089"
  shape: bbox 7.911 x 7.911 x 1.162 mm, 68 faces (baked)
FEATURE [Part::Feature] Part__Feature295  label="CUI_VGS-25W-090"
  shape: bbox 5.629 x 5.629 x 8.001 mm, 43 faces (baked)
FEATURE [Part::Feature] Part__Feature296  label="CUI_VGS-25W-091"
  shape: bbox 4.944 x 5.8 x 5.8 mm, 37 faces (baked)
FEATURE [Part::Feature] Part__Feature297  label="CUI_VGS-25W-092"
  shape: bbox 6 x 13.55 x 11.3 mm, 86 faces (baked)
FEATURE [Part::Feature] Part__Feature298  label="CUI_VGS-25W-093"
  shape: bbox 5.629 x 5.629 x 8.001 mm, 43 faces (baked)
FEATURE [Part::Feature] Part__Feature299  label="CUI_VGS-25W-094"
  shape: bbox 39.6 x 12 x 16 mm, 290 faces (baked)
FEATURE [Part::Feature] Part__Feature300  label="CUI_VGS-25W-095"
  shape: bbox 5.443 x 12.7 x 3.793 mm, 44 faces (baked)
FEATURE [Part::Feature] Part__Feature301  label="CUI_VGS-25W-096"
  shape: bbox 54.37 x 24.2 x 80.19 mm, 487 faces (baked)
FEATURE [Part::Feature] Part__Feature302  label="CUI_VGS-25W-097"
  shape: bbox 6 x 13.55 x 11.3 mm, 86 faces (baked)
FEATURE [Part::Feature] Part__Feature303  label="CUI_VGS-25W-098"
  shape: bbox 5.413 x 8.147 x 5.557 mm, 54 faces (baked)
FEATURE [Part::Feature] Part__Feature304  label="CUI_VGS-25W-099"
  shape: bbox 6 x 13.55 x 11.3 mm, 86 faces (baked)
FEATURE [Part::Feature] Part__Feature305  label="CUI_VGS-25W-100"
  shape: bbox 9.096 x 12.71 x 7.718 mm, 112 faces (baked)
FEATURE [Part::Feature] Part__Feature306  label="CUI_VGS-25W-101"
  shape: bbox 6 x 13.55 x 11.3 mm, 86 faces (baked)
FEATURE [Part::Feature] Part__Feature307  label="CUI_VGS-25W-102"
  shape: bbox 5.629 x 5.629 x 8.001 mm, 43 faces (baked)
FEATURE [Part::Feature] Part__Feature308  label="CUI_VGS-25W-103"
  shape: bbox 5.629 x 5.629 x 8.001 mm, 43 faces (baked)
FEATURE [Part::Feature] Part__Feature309  label="CUI_VGS-25W-104"
  shape: bbox 7.911 x 7.911 x 1.162 mm, 68 faces (baked)
FEATURE [Part::Feature] Part__Feature310  label="CUI_VGS-25W-105"
  shape: bbox 7.911 x 7.911 x 1.162 mm, 68 faces (baked)
FEATURE [Part::Feature] Part__Feature311  label="CUI_VGS-25W-106"
  shape: bbox 7 x 0.55 x 7 mm, 6 faces (baked)
FEATURE [Part::Feature] Part__Feature312  label="CUI_VGS-25W-107"
  shape: bbox 53.1 x 22.4 x 79.2 mm, 72 faces (baked)
FEATURE [Part::Feature] Part__Feature313  label="CUI_VGS-25W-108"
  shape: bbox 4.624 x 1.433 x 4.618 mm, 8 faces (baked)
FEATURE [Part::Feature] Part__Feature314  label="CUI_VGS-25W-109"
  shape: bbox 7.911 x 7.911 x 1.162 mm, 68 faces (baked)
FEATURE [Part::Feature] Part__Feature315  label="CUI_VGS-25W-110"
  shape: bbox 5.629 x 5.629 x 8.001 mm, 43 faces (baked)
FEATURE [Part::Feature] Part__Feature316  label="CUI_VGS-25W-111"
  shape: bbox 52.65 x 1.621 x 78.18 mm, 385 faces (baked)
FEATURE [Part::Feature] Part__Feature317  label="CUI_VGS-25W-112"
  shape: bbox 7.911 x 7.911 x 1.162 mm, 68 faces (baked)
FEATURE [App::Part] CUI_VGS_25W_008  label="CUI_VGS-25W-086"
  Group = -> [Part__Feature298,Part__Feature299,Part__Feature300,Part__Feature301,Part__Feature302,Part__Feature303,Part__Feature304,Part__Feature305,Part__Feature306,Part__Feature307,Part__Feature292,Part__Feature293,Part__Feature294,Part__Feature295,Part__Feature296,Part__Feature297,Part__Feature308,Part__Feature309,Part__Feature310,Part__Feature311,Part__Feature314,Part__Feature312,Part__Feature313,+3 more]
  Origin = -> Origin032
  Placement = pos=(22.5,-50.5,0.25) rot=(1,0,0;1.5708rad)
FEATURE [Sketcher::SketchObject] Sketch008
  ArcFitTolerance = 1e-06
  FullyConstrained = true
  MakeInternals = false
  Placement = pos=(0,0,0) rot=(1,0,0;1.5708rad)
  sketch-geometry (6):
    g0: LineSegment StartX=25 StartY=0 StartZ=0 EndX=25 EndY=-4 EndZ=0
    g1: LineSegment StartX=25 StartY=-4 StartZ=0 EndX=59.5 EndY=-4 EndZ=0
    g2: LineSegment StartX=59.5 StartY=-4 StartZ=0 EndX=59.5 EndY=21 EndZ=0
    g3: LineSegment StartX=59.5 StartY=21 StartZ=0 EndX=55.5 EndY=21 EndZ=0
    g4: LineSegment StartX=55.5 StartY=21 StartZ=0 EndX=55.5 EndY=0 EndZ=0
    g5: LineSegment StartX=55.5 StartY=0 StartZ=0 EndX=25 EndY=0 EndZ=0
  constraints (18):
    c: Coincident(g1,g0)
    c: Horizontal(g1)
    c: Vertical(g2)
    c: Coincident(g3,g2)
    c: Horizontal(g3)
    c: PointOnObject(g4,g-1)
    c: Vertical(g4)
    c: Coincident(g5,g4)
    c: Coincident(g5,g0)
    c: Horizontal(g5)
    c: Vertical(g0)
    c: Coincident(g1,g2)
    c: DistanceX(g0) = 25
    c: DistanceX(g5,g5) = 30.5
    c: DistanceX(g3,g3) = 4
    c: Coincident(g3,g4)
    c: DistanceY(g0,g0) = 4
    c: DistanceY(g2,g2) = 25
FEATURE [Part::Extrusion] Extrude008
  Base = -> Sketch008
  Dir = (0,-1,2e-16)
  DirMode = 2
  FaceMakerClass = Part::FaceMakerBullseye
  FaceMakerMode = 3
  LengthFwd = 20
  LengthRev = 0
  Solid = true
  Symmetric = false
FEATURE [Sketcher::SketchObject] Sketch009
  ArcFitTolerance = 1e-06
  FullyConstrained = true
  MakeInternals = false
  Placement = pos=(0,0,0) rot=(1,0,0;1.5708rad)
  sketch-geometry (6):
    g0: LineSegment StartX=73 StartY=21 StartZ=0 EndX=25 EndY=21 EndZ=0
    g1: LineSegment StartX=25 StartY=21 StartZ=0 EndX=25 EndY=-4 EndZ=0
    g2: LineSegment StartX=25 StartY=-4 StartZ=0 EndX=73 EndY=-4 EndZ=0
    g3: LineSegment StartX=73 StartY=-4 StartZ=0 EndX=73 EndY=21 EndZ=0
    g4: Circle CenterX=67 CenterY=15 CenterZ=0 NormalX=0 NormalY=0 NormalZ=1 AngleXU=0 Radius=1.625
    g5: Circle CenterX=67 CenterY=2 CenterZ=0 NormalX=0 NormalY=0 NormalZ=1 AngleXU=0 Radius=1.625
  constraints (18):
    c: Horizontal(g0)
    c: Vertical(g1)
    c: DistanceX(g0,g0) = 48
    c: DistanceX(g1) = 25
    c: Coincident(g2,g1)
    c: Coincident(g3,g2)
    c: Coincident(g3,g0)
    c: Vertical(g3)
    c: DistanceY(g1,g1) = 25
    c: Horizontal(g2)
    c: DistanceY(g1) = -4
    c: Coincident(g0,g1)
    c: Equal(g4,g5)
    c: Diameter(g4) = 3.25
    c: Vertical(g5,g4)
    c: DistanceY(g1,g5) = 6
    c: DistanceY(g5,g4) = 13
    c: DistanceX(g1,g5) = 42
FEATURE [Part::Extrusion] Extrude009
  Base = -> Sketch009
  Dir = (0,-1,2e-16)
  DirMode = 2
  FaceMakerClass = Part::FaceMakerBullseye
  FaceMakerMode = 3
  LengthFwd = 5
  LengthRev = 0
  Solid = true
  Symmetric = false
FEATURE [Part::MultiFuse] Fusion017
  Shapes = -> [Extrude009,Extrude008]
FEATURE [Sketcher::SketchObject] Sketch010
  ArcFitTolerance = 1e-06
  FullyConstrained = true
  MakeInternals = false
  sketch-geometry (1):
    g0: Circle CenterX=29.75 CenterY=-15.85 CenterZ=0 NormalX=0 NormalY=0 NormalZ=1 AngleXU=0 Radius=1.625
  constraints (3):
    c: DistanceX(g0) = 29.75
    c: DistanceY(g0) = -15.85
    c: Diameter(g0) = 3.25
FEATURE [Part::Extrusion] Extrude010
  Base = -> Sketch010
  Dir = (0,0,1)
  DirMode = 2
  FaceMakerClass = Part::FaceMakerBullseye
  FaceMakerMode = 3
  LengthFwd = 10
  LengthRev = 0
  Reversed = true
  Solid = true
  Symmetric = false
FEATURE [Sketcher::SketchObject] Sketch011
  ArcFitTolerance = 1e-06
  FullyConstrained = true
  MakeInternals = false
  Placement = pos=(0,0,0) rot=(0.57735,0.57735,0.57735;2.0944rad)
  sketch-geometry (1):
    g0: Circle CenterX=-8.1 CenterY=14.25 CenterZ=0 NormalX=0 NormalY=0 NormalZ=1 AngleXU=0 Radius=1.625
  constraints (3):
    c: DistanceX(g0) = -8.1
    c: DistanceY(g0) = 14.25
    c: Diameter(g0) = 3.25
FEATURE [Part::Extrusion] Extrude011
  Base = -> Sketch011
  Dir = (1,0,0)
  DirMode = 2
  FaceMakerClass = Part::FaceMakerBullseye
  FaceMakerMode = 3
  LengthFwd = 75
  LengthRev = 0
  Solid = true
  Symmetric = false
FEATURE [Part::MultiFuse] Fusion018  label="cuts001"
  Shapes = -> [Extrude010,Extrude011]
FEATURE [Part::Cut] Cut020
  Base = -> Fusion017
  Tool = -> Fusion018
FEATURE [Part::Fillet] Fillet017
  Base = -> Cut020
  EdgeLinks = -> Cut020 [Edge30,Edge33,Edge44,Edge46,Edge47,Edge48]
  Edges = 6 edges r=1: [Edge30,Edge33,Edge44,Edge46,Edge47,Edge48]
FEATURE [Part::Fillet] Fillet015
  Base = -> Fillet017
  EdgeLinks = -> Fillet017 [Edge41,Edge47,Edge48]
  Edges = 3 edges r=1: [Edge41,Edge47,Edge48]
FEATURE [Part::Fillet] Fillet016
  Base = -> Fillet015
  EdgeLinks = -> Fillet015 [Edge15,Edge38,Edge46,Edge47]
  Edges = 4 edges r=0.25: [Edge15,Edge38,Edge46,Edge47]
FEATURE [Part::Compound] Compound001  label="5vHolder001"
  Links = -> [CUI_VGS_25W_008,Fillet016]
  Placement = pos=(145.5,158,-99.25) rot=(0,1,0;1.5708rad)
FEATURE [Part::Feature] Part__Feature318  label="Heat Sink002"
  shape: bbox 100 x 91 x 19 mm, 161 faces (baked)
FEATURE [Part::Feature] Part__Feature319  label="Component011"
  Placement = pos=(-40,-40,21) rot=(0,1,0;3.14159rad)
  shape: bbox 83.92 x 84.69 x 8.441 mm, 27 faces (baked)
FEATURE [Part::Feature] Part__Feature320  label="80mmFanSlim003"
  shape: bbox 82.8 x 82.8 x 10.8 mm, 179 faces (baked)
FEATURE [App::Part] Part008  label="80mm_Fan002"
  Group = -> [Part__Feature319,Part__Feature320]
  Origin = -> Origin033
  Placement = pos=(0,0,0) rot=(1,0,0;3.14159rad)
FEATURE [Part::Feature] Part__Feature321  label="Battery Holder002"
  shape: bbox 28.5 x 16 x 6 mm, 91 faces (baked)
FEATURE [Part::Feature] Part__Feature322  label="DC Jack002"
  shape: bbox 7.6 x 11.5 x 9.75 mm, 10 faces (baked)
FEATURE [Part::Feature] Part__Feature323  label="PCB002"
  shape: bbox 90 x 90 x 3.3 mm, 59 faces (baked)
FEATURE [Part::Feature] Part__Feature324  label="HDMI002"
  shape: bbox 14.51 x 11.61 x 5.506 mm, 31 faces (baked)
FEATURE [Part::Feature] Part__Feature325  label="Ethernet002"
  shape: bbox 15.9 x 21.4 x 13.5 mm, 25 faces (baked)
FEATURE [Part::Feature] Part__Feature326  label="USB 3.0 B002"
  shape: bbox 14.55 x 17.5 x 16.15 mm, 36 faces (baked)
FEATURE [Part::Feature] Part__Feature327  label="USB 3.0 A002"
  shape: bbox 14.55 x 17.5 x 16.15 mm, 36 faces (baked)
FEATURE [Part::Feature] Part__Feature328  label="Audio Jack002"
  shape: bbox 6.5 x 14 x 4 mm, 10 faces (baked)
FEATURE [Part::Feature] Part__Feature329  label="Fan Plug002"
  shape: bbox 3.75 x 7.5 x 4.75 mm, 32 faces (baked)
FEATURE [Part::Feature] Part__Feature330  label="REMOCON002"
  shape: bbox 7.006 x 5.006 x 12.01 mm, 30 faces (baked)
FEATURE [Part::Feature] Part__Feature331  label="eMMC002"
  shape: bbox 13.5 x 18.5 x 2.8 mm, 33 faces (baked)
FEATURE [Part::Feature] Part__Feature332  label="MicroUSB002"
  shape: bbox 7.012 x 4.616 x 3.511 mm, 31 faces (baked)
FEATURE [Part::Feature] Part__Feature333  label="Switch002"
  shape: bbox 9 x 5.74 x 3.5 mm, 11 faces (baked)
FEATURE [Part::Feature] Part__Feature334  label="MicroSD Card Socket002"
  shape: bbox 11.5 x 5.5 x 3.5 mm, 11 faces (baked)
FEATURE [Part::Feature] Part__Feature335  label="7 Pin Header002"
  shape: bbox 17.5 x 2.5 x 8 mm, 41 faces (baked)
FEATURE [Part::Feature] Part__Feature336  label="UART002"
  shape: bbox 5 x 12.5 x 6 mm, 43 faces (baked)
FEATURE [Part::Feature] Part__Feature337  label="40 Pin Header002"
  shape: bbox 5 x 50 x 8 mm, 206 faces (baked)
FEATURE [App::Part] Odroid_N2__v006  label="Odroid-N2+ v006"
  Group = -> [Part__Feature318,Part__Feature321,Part__Feature322,Part__Feature323,Part__Feature324,Part__Feature325,Part__Feature326,Part__Feature327,Part__Feature328,Part__Feature329,Part__Feature330,Part__Feature331,Part__Feature332,Part__Feature333,Part__Feature334,Part__Feature335,Part__Feature336,Part__Feature337]
  Origin = -> Origin034
  Placement = pos=(-59,-819.5,-41.5) rot=(0,0,1;0rad)
FEATURE [App::Part] Part009  label="N2+002"
  Group = -> [Part008,Odroid_N2__v006]
  Origin = -> Origin035
  Placement = pos=(100,20,25) rot=(-1,0,0;0rad)
FEATURE [Sketcher::SketchObject] Sketch012
  ArcFitTolerance = 1e-06
  FullyConstrained = true
  MakeInternals = false
  sketch-geometry (22):
    g0: LineSegment StartX=18 StartY=115 StartZ=0 EndX=18 EndY=5 EndZ=0
    g1: LineSegment StartX=18 StartY=5 StartZ=0 EndX=102 EndY=5 EndZ=0
    g2: LineSegment StartX=102 StartY=5 StartZ=0 EndX=102 EndY=115 EndZ=0
    g3: LineSegment StartX=102 StartY=115 StartZ=0 EndX=18 EndY=115 EndZ=0
    g4: LineSegment StartX=30 StartY=105 StartZ=0 EndX=30 EndY=15 EndZ=0
    g5: LineSegment StartX=30 StartY=15 StartZ=0 EndX=90 EndY=15 EndZ=0
    g6: LineSegment StartX=90 StartY=15 StartZ=0 EndX=90 EndY=105 EndZ=0
    g7: LineSegment StartX=90 StartY=105 StartZ=0 EndX=30 EndY=105 EndZ=0
    g8: Circle CenterX=24.3 CenterY=95.75 CenterZ=0 NormalX=0 NormalY=0 NormalZ=1 AngleXU=0 Radius=1.625
    g9: Circle CenterX=95.8 CenterY=95.75 CenterZ=0 NormalX=0 NormalY=0 NormalZ=1 AngleXU=0 Radius=1.625
    g10: Circle CenterX=95.8 CenterY=24.25 CenterZ=0 NormalX=0 NormalY=0 NormalZ=1 AngleXU=0 Radius=1.625
    g11: Circle CenterX=24.3 CenterY=24.25 CenterZ=0 NormalX=0 NormalY=0 NormalZ=1 AngleXU=0 Radius=1.625
    g12: Circle CenterX=28 CenterY=10 CenterZ=0 NormalX=0 NormalY=0 NormalZ=1 AngleXU=0 Radius=1.625
    g13: Circle CenterX=43 CenterY=10 CenterZ=0 NormalX=0 NormalY=0 NormalZ=1 AngleXU=0 Radius=1.625
    g14: Circle CenterX=58 CenterY=10 CenterZ=0 NormalX=0 NormalY=0 NormalZ=1 AngleXU=0 Radius=1.625
    g15: Circle CenterX=73 CenterY=10 CenterZ=0 NormalX=0 NormalY=0 NormalZ=1 AngleXU=0 Radius=1.625
    g16: Circle CenterX=88 CenterY=10 CenterZ=0 NormalX=0 NormalY=0 NormalZ=1 AngleXU=0 Radius=1.625
    g17: Circle CenterX=28 CenterY=110 CenterZ=0 NormalX=0 NormalY=0 NormalZ=1 AngleXU=0 Radius=1.625
    g18: Circle CenterX=43 CenterY=110 CenterZ=0 NormalX=0 NormalY=0 NormalZ=1 AngleXU=0 Radius=1.625
    g19: Circle CenterX=58 CenterY=110 CenterZ=0 NormalX=0 NormalY=0 NormalZ=1 AngleXU=0 Radius=1.625
    g20: Circle CenterX=73 CenterY=110 CenterZ=0 NormalX=0 NormalY=0 NormalZ=1 AngleXU=0 Radius=1.625
    g21: Circle CenterX=88 CenterY=110 CenterZ=0 NormalX=0 NormalY=0 NormalZ=1 AngleXU=0 Radius=1.625
  constraints (59):
    c: Vertical(g0)
    c: Coincident(g1,g0)
    c: Horizontal(g1)
    c: Vertical(g2)
    c: Coincident(g3,g2)
    c: Coincident(g3,g0)
    c: Horizontal(g3)
    c: Coincident(g4,g5)
    c: Coincident(g5,g6)
    c: Coincident(g6,g7)
    c: Coincident(g7,g4)
    c: Vertical(g4)
    c: Vertical(g6)
    c: Horizontal(g5)
    c: Horizontal(g7)
    c: DistanceY(g0) = 5
    c: DistanceX(g0) = 18
    c: DistanceX(g0,g4) = 12
    c: DistanceX(g5,g5) = 60
    c: Coincident(g1,g2)
    c: DistanceX(g5,g1) = 12
    c: DistanceY(g0,g4) = 10
    c: DistanceY(g4,g4) = 90
    c: DistanceY(g4,g0) = 10
    c: Equal(g12, g13-g16) x4
    c: Equal(g12,g10)
    c: Equal(g12,g9)
    c: Equal(g12,g8)
    c: Equal(g12,g11)
    c: Equal(g12, g17-g21) x5
    c: Diameter(g12) = 3.25
    c: Horizontal(g12,g13)
    c: Horizontal(g13,g14)
    c: Horizontal(g14,g15)
    c: Horizontal(g15,g16)
    c: Horizontal(g17,g18)
    c: Horizontal(g18,g19)
    c: Horizontal(g19,g20)
    c: Horizontal(g20,g21)
    c: Horizontal(g8,g9)
    c: Horizontal(g11,g10)
    c: Vertical(g11,g8)
    c: DistanceX(g12,g13) = 15
    c: DistanceX(g13,g14) = 15
    c: Distance(g14,g15) = 15
    c: Distance(g15,g16) = 15
    c: DistanceX(g0,g12) = 10
    c: DistanceY(g0,g12) = 5
    c: DistanceY(g17,g0) = 5
    c: Vertical(g17,g12)
    c: Vertical(g18,g13)
    c: Vertical(g19,g14)
    c: Vertical(g15,g20)
    c: Vertical(g16,g21)
    c: Vertical(g10,g9)
    c: DistanceX(g11) = 24.3
    c: DistanceY(g11) = 24.25
    c: DistanceX(g11,g10) = 71.5
    c: DistanceY(g11,g8) = 71.5
FEATURE [Part::Extrusion] Extrude012
  Base = -> Sketch012
  Dir = (0,0,1)
  DirMode = 2
  FaceMakerClass = Part::FaceMakerBullseye
  FaceMakerMode = 3
  LengthFwd = 8
  LengthRev = 0
  Solid = true
  Symmetric = false
FEATURE [Part::Fillet] Fillet018
  Base = -> Extrude012
  EdgeLinks = -> Extrude012 [Edge1,Edge2,Edge4,Edge5,Edge7,Edge8,Edge10,Edge12,Edge16,Edge19,Edge22,Edge24]
  Edges = 12 edges r=3: [Edge1,Edge2,Edge4,Edge5,Edge7,Edge8,Edge10,Edge12,Edge16,Edge19,Edge22,Edge24]
FEATURE [Part::Fillet] Fillet019
  Base = -> Fillet018
  EdgeLinks = -> Fillet018 [Edge55,Edge57,Edge59,Edge61,Edge63,Edge65,Edge67,Edge69,Edge71,Edge73,Edge75,Edge77,Edge81]
  Edges = 13 edges r=0.25: [Edge55,Edge57,Edge59,Edge61,Edge63,Edge65,Edge67,Edge69,Edge71,Edge73,Edge75,Edge77,Edge81]
FEATURE [Sketcher::SketchObject] Sketch013
  ArcFitTolerance = 1e-06
  FullyConstrained = true
  MakeInternals = false
  sketch-geometry (4):
    g0: Circle CenterX=24.3 CenterY=95.75 CenterZ=0 NormalX=0 NormalY=0 NormalZ=1 AngleXU=0 Radius=3
    g1: Circle CenterX=95.8 CenterY=95.75 CenterZ=0 NormalX=0 NormalY=0 NormalZ=1 AngleXU=0 Radius=3
    g2: Circle CenterX=95.8 CenterY=24.25 CenterZ=0 NormalX=0 NormalY=0 NormalZ=1 AngleXU=0 Radius=3
    g3: Circle CenterX=24.3 CenterY=24.25 CenterZ=0 NormalX=0 NormalY=0 NormalZ=1 AngleXU=0 Radius=3
  constraints (12):
    c: Horizontal(g0,g1)
    c: Horizontal(g3,g2)
    c: Vertical(g3,g0)
    c: Vertical(g2,g1)
    c: DistanceX(g3) = 24.3
    c: DistanceY(g3) = 24.25
    c: DistanceX(g3,g2) = 71.5
    c: DistanceY(g3,g0) = 71.5
    c: Equal(g3,g2)
    c: Equal(g3,g1)
    c: Equal(g3,g0)
    c: Diameter(g3) = 6
FEATURE [Part::Extrusion] Extrude013
  Base = -> Sketch013
  Dir = (0,0,1)
  DirMode = 2
  FaceMakerClass = Part::FaceMakerBullseye
  FaceMakerMode = 3
  LengthFwd = 3.5
  LengthRev = 0
  Solid = true
  Symmetric = false
FEATURE [Part::Cut] Cut021  label="n2Holder"
  Base = -> Fillet019
  Tool = -> Extrude013
FEATURE [Part::Compound] Compound002  label="n2WithTheHolder"
  Links = -> [Part009,Cut021]
  Placement = pos=(-150,158,-40) rot=(1,0,0;1.5708rad)
FEATURE [Part::Feature] Part__Feature338  label="Heat Sink003"
  shape: bbox 100 x 91 x 19 mm, 161 faces (baked)
FEATURE [Part::Feature] Part__Feature339  label="Component012"
  Placement = pos=(-40,-40,21) rot=(0,1,0;3.14159rad)
  shape: bbox 83.92 x 84.69 x 8.441 mm, 27 faces (baked)
FEATURE [Part::Feature] Part__Feature340  label="80mmFanSlim004"
  shape: bbox 82.8 x 82.8 x 10.8 mm, 179 faces (baked)
FEATURE [App::Part] Part010  label="80mm_Fan003"
  Group = -> [Part__Feature339,Part__Feature340]
  Origin = -> Origin036
  Placement = pos=(0,0,0) rot=(1,0,0;3.14159rad)
FEATURE [Part::Feature] Part__Feature341  label="Battery Holder003"
  shape: bbox 28.5 x 16 x 6 mm, 91 faces (baked)
FEATURE [Part::Feature] Part__Feature342  label="DC Jack003"
  shape: bbox 7.6 x 11.5 x 9.75 mm, 10 faces (baked)
FEATURE [Part::Feature] Part__Feature343  label="PCB003"
  shape: bbox 90 x 90 x 3.3 mm, 59 faces (baked)
FEATURE [Part::Feature] Part__Feature344  label="HDMI003"
  shape: bbox 14.51 x 11.61 x 5.506 mm, 31 faces (baked)
FEATURE [Part::Feature] Part__Feature345  label="Ethernet003"
  shape: bbox 15.9 x 21.4 x 13.5 mm, 25 faces (baked)
FEATURE [Part::Feature] Part__Feature346  label="USB 3.0 B003"
  shape: bbox 14.55 x 17.5 x 16.15 mm, 36 faces (baked)
FEATURE [Part::Feature] Part__Feature347  label="USB 3.0 A003"
  shape: bbox 14.55 x 17.5 x 16.15 mm, 36 faces (baked)
FEATURE [Part::Feature] Part__Feature348  label="Audio Jack003"
  shape: bbox 6.5 x 14 x 4 mm, 10 faces (baked)
FEATURE [Part::Feature] Part__Feature349  label="Fan Plug003"
  shape: bbox 3.75 x 7.5 x 4.75 mm, 32 faces (baked)
FEATURE [Part::Feature] Part__Feature350  label="REMOCON003"
  shape: bbox 7.006 x 5.006 x 12.01 mm, 30 faces (baked)
FEATURE [Part::Feature] Part__Feature351  label="eMMC003"
  shape: bbox 13.5 x 18.5 x 2.8 mm, 33 faces (baked)
FEATURE [Part::Feature] Part__Feature352  label="MicroUSB003"
  shape: bbox 7.012 x 4.616 x 3.511 mm, 31 faces (baked)
FEATURE [Part::Feature] Part__Feature353  label="Switch003"
  shape: bbox 9 x 5.74 x 3.5 mm, 11 faces (baked)
FEATURE [Part::Feature] Part__Feature354  label="MicroSD Card Socket003"
  shape: bbox 11.5 x 5.5 x 3.5 mm, 11 faces (baked)
FEATURE [Part::Feature] Part__Feature355  label="7 Pin Header003"
  shape: bbox 17.5 x 2.5 x 8 mm, 41 faces (baked)
FEATURE [Part::Feature] Part__Feature356  label="UART003"
  shape: bbox 5 x 12.5 x 6 mm, 43 faces (baked)
FEATURE [Part::Feature] Part__Feature357  label="40 Pin Header003"
  shape: bbox 5 x 50 x 8 mm, 206 faces (baked)
FEATURE [App::Part] Odroid_N2__v007  label="Odroid-N2+ v007"
  Group = -> [Part__Feature338,Part__Feature341,Part__Feature342,Part__Feature343,Part__Feature344,Part__Feature345,Part__Feature346,Part__Feature347,Part__Feature348,Part__Feature349,Part__Feature350,Part__Feature351,Part__Feature352,Part__Feature353,Part__Feature354,Part__Feature355,Part__Feature356,Part__Feature357]
  Origin = -> Origin037
  Placement = pos=(-59,-819.5,-41.5) rot=(0,0,1;0rad)
FEATURE [App::Part] Part011  label="N2+003"
  Group = -> [Part010,Odroid_N2__v007]
  Origin = -> Origin038
  Placement = pos=(100,20,25) rot=(-1,0,0;0rad)
FEATURE [Sketcher::SketchObject] Sketch014
  ArcFitTolerance = 1e-06
  FullyConstrained = true
  MakeInternals = false
  sketch-geometry (22):
    g0: LineSegment StartX=18 StartY=115 StartZ=0 EndX=18 EndY=5 EndZ=0
    g1: LineSegment StartX=18 StartY=5 StartZ=0 EndX=102 EndY=5 EndZ=0
    g2: LineSegment StartX=102 StartY=5 StartZ=0 EndX=102 EndY=115 EndZ=0
    g3: LineSegment StartX=102 StartY=115 StartZ=0 EndX=18 EndY=115 EndZ=0
    g4: LineSegment StartX=30 StartY=105 StartZ=0 EndX=30 EndY=15 EndZ=0
    g5: LineSegment StartX=30 StartY=15 StartZ=0 EndX=90 EndY=15 EndZ=0
    g6: LineSegment StartX=90 StartY=15 StartZ=0 EndX=90 EndY=105 EndZ=0
    g7: LineSegment StartX=90 StartY=105 StartZ=0 EndX=30 EndY=105 EndZ=0
    g8: Circle CenterX=24.3 CenterY=95.75 CenterZ=0 NormalX=0 NormalY=0 NormalZ=1 AngleXU=0 Radius=1.625
    g9: Circle CenterX=95.8 CenterY=95.75 CenterZ=0 NormalX=0 NormalY=0 NormalZ=1 AngleXU=0 Radius=1.625
    g10: Circle CenterX=95.8 CenterY=24.25 CenterZ=0 NormalX=0 NormalY=0 NormalZ=1 AngleXU=0 Radius=1.625
    g11: Circle CenterX=24.3 CenterY=24.25 CenterZ=0 NormalX=0 NormalY=0 NormalZ=1 AngleXU=0 Radius=1.625
    g12: Circle CenterX=28 CenterY=10 CenterZ=0 NormalX=0 NormalY=0 NormalZ=1 AngleXU=0 Radius=1.625
    g13: Circle CenterX=43 CenterY=10 CenterZ=0 NormalX=0 NormalY=0 NormalZ=1 AngleXU=0 Radius=1.625
    g14: Circle CenterX=58 CenterY=10 CenterZ=0 NormalX=0 NormalY=0 NormalZ=1 AngleXU=0 Radius=1.625
    g15: Circle CenterX=73 CenterY=10 CenterZ=0 NormalX=0 NormalY=0 NormalZ=1 AngleXU=0 Radius=1.625
    g16: Circle CenterX=88 CenterY=10 CenterZ=0 NormalX=0 NormalY=0 NormalZ=1 AngleXU=0 Radius=1.625
    g17: Circle CenterX=28 CenterY=110 CenterZ=0 NormalX=0 NormalY=0 NormalZ=1 AngleXU=0 Radius=1.625
    g18: Circle CenterX=43 CenterY=110 CenterZ=0 NormalX=0 NormalY=0 NormalZ=1 AngleXU=0 Radius=1.625
    g19: Circle CenterX=58 CenterY=110 CenterZ=0 NormalX=0 NormalY=0 NormalZ=1 AngleXU=0 Radius=1.625
    g20: Circle CenterX=73 CenterY=110 CenterZ=0 NormalX=0 NormalY=0 NormalZ=1 AngleXU=0 Radius=1.625
    g21: Circle CenterX=88 CenterY=110 CenterZ=0 NormalX=0 NormalY=0 NormalZ=1 AngleXU=0 Radius=1.625
  constraints (59):
    c: Vertical(g0)
    c: Coincident(g1,g0)
    c: Horizontal(g1)
    c: Vertical(g2)
    c: Coincident(g3,g2)
    c: Coincident(g3,g0)
    c: Horizontal(g3)
    c: Coincident(g4,g5)
    c: Coincident(g5,g6)
    c: Coincident(g6,g7)
    c: Coincident(g7,g4)
    c: Vertical(g4)
    c: Vertical(g6)
    c: Horizontal(g5)
    c: Horizontal(g7)
    c: DistanceY(g0) = 5
    c: DistanceX(g0) = 18
    c: DistanceX(g0,g4) = 12
    c: DistanceX(g5,g5) = 60
    c: Coincident(g1,g2)
    c: DistanceX(g5,g1) = 12
    c: DistanceY(g0,g4) = 10
    c: DistanceY(g4,g4) = 90
    c: DistanceY(g4,g0) = 10
    c: Equal(g12, g13-g16) x4
    c: Equal(g12,g10)
    c: Equal(g12,g9)
    c: Equal(g12,g8)
    c: Equal(g12,g11)
    c: Equal(g12, g17-g21) x5
    c: Diameter(g12) = 3.25
    c: Horizontal(g12,g13)
    c: Horizontal(g13,g14)
    c: Horizontal(g14,g15)
    c: Horizontal(g15,g16)
    c: Horizontal(g17,g18)
    c: Horizontal(g18,g19)
    c: Horizontal(g19,g20)
    c: Horizontal(g20,g21)
    c: Horizontal(g8,g9)
    c: Horizontal(g11,g10)
    c: Vertical(g11,g8)
    c: DistanceX(g12,g13) = 15
    c: DistanceX(g13,g14) = 15
    c: Distance(g14,g15) = 15
    c: Distance(g15,g16) = 15
    c: DistanceX(g0,g12) = 10
    c: DistanceY(g0,g12) = 5
    c: DistanceY(g17,g0) = 5
    c: Vertical(g17,g12)
    c: Vertical(g18,g13)
    c: Vertical(g19,g14)
    c: Vertical(g15,g20)
    c: Vertical(g16,g21)
    c: Vertical(g10,g9)
    c: DistanceX(g11) = 24.3
    c: DistanceY(g11) = 24.25
    c: DistanceX(g11,g10) = 71.5
    c: DistanceY(g11,g8) = 71.5
FEATURE [Part::Extrusion] Extrude014
  Base = -> Sketch014
  Dir = (0,0,1)
  DirMode = 2
  FaceMakerClass = Part::FaceMakerBullseye
  FaceMakerMode = 3
  LengthFwd = 8
  LengthRev = 0
  Solid = true
  Symmetric = false
FEATURE [Part::Fillet] Fillet020
  Base = -> Extrude014
  EdgeLinks = -> Extrude014 [Edge1,Edge2,Edge4,Edge5,Edge7,Edge8,Edge10,Edge12,Edge16,Edge19,Edge22,Edge24]
  Edges = 12 edges r=3: [Edge1,Edge2,Edge4,Edge5,Edge7,Edge8,Edge10,Edge12,Edge16,Edge19,Edge22,Edge24]
FEATURE [Part::Fillet] Fillet021
  Base = -> Fillet020
  EdgeLinks = -> Fillet020 [Edge55,Edge57,Edge59,Edge61,Edge63,Edge65,Edge67,Edge69,Edge71,Edge73,Edge75,Edge77,Edge81]
  Edges = 13 edges r=0.25: [Edge55,Edge57,Edge59,Edge61,Edge63,Edge65,Edge67,Edge69,Edge71,Edge73,Edge75,Edge77,Edge81]
FEATURE [Sketcher::SketchObject] Sketch015
  ArcFitTolerance = 1e-06
  FullyConstrained = true
  MakeInternals = false
  sketch-geometry (4):
    g0: Circle CenterX=24.3 CenterY=95.75 CenterZ=0 NormalX=0 NormalY=0 NormalZ=1 AngleXU=0 Radius=3
    g1: Circle CenterX=95.8 CenterY=95.75 CenterZ=0 NormalX=0 NormalY=0 NormalZ=1 AngleXU=0 Radius=3
    g2: Circle CenterX=95.8 CenterY=24.25 CenterZ=0 NormalX=0 NormalY=0 NormalZ=1 AngleXU=0 Radius=3
    g3: Circle CenterX=24.3 CenterY=24.25 CenterZ=0 NormalX=0 NormalY=0 NormalZ=1 AngleXU=0 Radius=3
  constraints (12):
    c: Horizontal(g0,g1)
    c: Horizontal(g3,g2)
    c: Vertical(g3,g0)
    c: Vertical(g2,g1)
    c: DistanceX(g3) = 24.3
    c: DistanceY(g3) = 24.25
    c: DistanceX(g3,g2) = 71.5
    c: DistanceY(g3,g0) = 71.5
    c: Equal(g3,g2)
    c: Equal(g3,g1)
    c: Equal(g3,g0)
    c: Diameter(g3) = 6
FEATURE [Part::Extrusion] Extrude015
  Base = -> Sketch015
  Dir = (0,0,1)
  DirMode = 2
  FaceMakerClass = Part::FaceMakerBullseye
  FaceMakerMode = 3
  LengthFwd = 3.5
  LengthRev = 0
  Solid = true
  Symmetric = false
FEATURE [Part::Cut] Cut022  label="n2Holder001"
  Base = -> Fillet021
  Tool = -> Extrude015
FEATURE [Part::Compound] Compound003  label="n2WithTheHolder001"
  Links = -> [Part011,Cut022]
  Placement = pos=(-45,158,-40) rot=(1,0,0;1.5708rad)
FEATURE [Part::Box] Box034  label="Main_box"
  AttacherType = Attacher::AttachEngine3D
  Height = 28
  Length = 89
  Width = 118
FEATURE [Part::Box] Box035  label="Cube019"
  AttacherType = Attacher::AttachEngine3D
  Height = 13.25
  Length = 17
  Placement = pos=(72,14.25,7) rot=(0,0,1;0rad)
  Width = 65
FEATURE [Part::Box] Box002  label="Cube020"
  AttacherType = Attacher::AttachEngine3D
  Height = 13.25
  Length = 17
  Placement = pos=(72,88.5,7) rot=(0,0,1;0rad)
  Width = 16.5
FEATURE [Part::Box] Box036  label="Power"
  AttacherType = Attacher::AttachEngine3D
  Height = 11
  Length = 30
  Placement = pos=(32,-9,11.75) rot=(0,0,1;0rad)
  Width = 9
FEATURE [Part::Box] Box037  label="mount1"
  AttacherType = Attacher::AttachEngine3D
  Height = 23.2
  Length = 1
  Placement = pos=(89,-15.5,2.25) rot=(0,0,1;0rad)
  Width = 25.5
FEATURE [Part::Box] Box038  label="mount2"
  AttacherType = Attacher::AttachEngine3D
  Height = 23.2
  Length = 1
  Placement = pos=(89,108,2.25) rot=(0,0,1;0rad)
  Width = 25.5
FEATURE [Part::Cut] Cut023  label="LAN_4_Cut"
  Base = -> Box034
  Tool = -> Box035
FEATURE [Part::Cut] Cut024  label="LAN_5_cut"
  Base = -> Cut023
  Tool = -> Box002
FEATURE [Part::Cylinder] Cylinder027
  Angle = 360
  AttacherType = Attacher::AttachEngine3D
  FirstAngle = 0
  Height = 10
  Placement = pos=(93,-3,4.5) rot=(0,1,0;4.71239rad)
  Radius = 3
  SecondAngle = 0
FEATURE [Part::Cylinder] Cylinder028
  Angle = 360
  AttacherType = Attacher::AttachEngine3D
  FirstAngle = 0
  Height = 10
  Placement = pos=(93,121,4.5) rot=(0,-1,0;1.5708rad)
  Radius = 3
  SecondAngle = 0
FEATURE [Part::Cylinder] Cylinder029
  Angle = 360
  AttacherType = Attacher::AttachEngine3D
  FirstAngle = 0
  Height = 10
  Placement = pos=(85,-9.5,6.25) rot=(0,1,0;1.5708rad)
  Radius = 1.5
  SecondAngle = 0
FEATURE [Part::Cylinder] Cylinder030
  Angle = 360
  AttacherType = Attacher::AttachEngine3D
  FirstAngle = 0
  Height = 10
  Placement = pos=(85,-9.5,20.25) rot=(0,1,0;1.5708rad)
  Radius = 1.5
  SecondAngle = 0
FEATURE [Part::Cylinder] Cylinder031
  Angle = 360
  AttacherType = Attacher::AttachEngine3D
  FirstAngle = 0
  Height = 10
  Placement = pos=(85,127.5,6.25) rot=(0,1,0;1.5708rad)
  Radius = 1.5
  SecondAngle = 0
FEATURE [Part::Cylinder] Cylinder032
  Angle = 360
  AttacherType = Attacher::AttachEngine3D
  FirstAngle = 0
  Height = 10
  Placement = pos=(85,127.5,20.25) rot=(0,1,0;1.5708rad)
  Radius = 1.5
  SecondAngle = 0
FEATURE [Part::MultiFuse] Fusion019  label="LAN_Power_Fused"
  Shapes = -> [Cut024,Box036,Box037,Box038]
FEATURE [Part::MultiFuse] Fusion020  label="mount_cyl"
  Placement = pos=(0,0,9.25) rot=(0,0,1;0rad)
  Shapes = -> [Cylinder027,Cylinder028]
FEATURE [Part::Cut] Cut025  label="Main_box001"
  Base = -> Fusion019
  Tool = -> Fusion020
FEATURE [Part::MultiFuse] Fusion021  label="mount_small_cyl"
  Refine = true
  Shapes = -> [Cylinder029,Cylinder030,Cylinder031,Cylinder032]
FEATURE [Part::Cut] Cut026  label="main_box001"
  Base = -> Cut025
  Refine = true
  Tool = -> Fusion021
FEATURE [Part::Fillet] Fillet022  label="Switch"
  Base = -> Cut026
  EdgeLinks = -> Cut026 [Edge10,Edge14,Edge21,Edge22,Edge23,Edge27,Edge41]
  Edges = 7 edges r=2: [Edge10,Edge14,Edge21,Edge22,Edge23,Edge27,Edge41]
  Placement = pos=(-144.75,67.25,81) rot=(0.57735,0.57735,-0.57735;4.18879rad)
FEATURE [Part::Box] Box039  label="Cube021"
  AttacherType = Attacher::AttachEngine3D
  Height = 2
  Length = 3
  Placement = pos=(-1.5,29,19.5) rot=(0,0,1;0rad)
  Width = 2
FEATURE [Part::Box] Box040  label="Cube022"
  AttacherType = Attacher::AttachEngine3D
  Height = 2
  Length = 3
  Placement = pos=(-1.5,29,19.5) rot=(0,0,1;0rad)
  Width = 2
FEATURE [Part::Box] Box041  label="Cube023"
  AttacherType = Attacher::AttachEngine3D
  Height = 5
  Length = 12
  Placement = pos=(15,12,-20) rot=(0,0,1;0rad)
  Width = 10
FEATURE [Part::Box] Box042  label="Cube024"
  AttacherType = Attacher::AttachEngine3D
  Height = 5
  Length = 12
  Placement = pos=(15,12,-20) rot=(0,0,1;0rad)
  Width = 10
FEATURE [Part::Box] Box043  label="Cube025"
  AttacherType = Attacher::AttachEngine3D
  Height = 13
  Length = 24
  Placement = pos=(-12,-2,12) rot=(0,0,1;0rad)
  Width = 42
FEATURE [Part::Box] Box044  label="Cube005"
  AttacherType = Attacher::AttachEngine3D
  Height = 13
  Length = 24
  Placement = pos=(-12,-2,12) rot=(0,0,1;0rad)
  Width = 42
FEATURE [Part::Cylinder] Cylinder033
  Angle = 360
  AttacherType = Attacher::AttachEngine3D
  FirstAngle = 0
  Height = 27
  Placement = pos=(0,-2,0) rot=(-1,0,0;1.5708rad)
  Radius = 5.9
  SecondAngle = 0
FEATURE [Part::Cylinder] Cylinder034
  Angle = 360
  AttacherType = Attacher::AttachEngine3D
  FirstAngle = 0
  Height = 5
  Placement = pos=(0,13,-15) rot=(0,0,1;0rad)
  Radius = 6.5
  SecondAngle = 0
FEATURE [Part::Cylinder] Cylinder035
  Angle = 360
  AttacherType = Attacher::AttachEngine3D
  FirstAngle = 0
  Height = 10
  Placement = pos=(10.87,21,-16.5) rot=(1,0,0;4.71239rad)
  Radius = 1.25
  SecondAngle = 0
FEATURE [Part::Cylinder] Cylinder036
  Angle = 360
  AttacherType = Attacher::AttachEngine3D
  FirstAngle = 0
  Height = 10
  Placement = pos=(-10.87,21,-16.5) rot=(-1,0,0;1.5708rad)
  Radius = 1.25
  SecondAngle = 0
FEATURE [Part::Cylinder] Cylinder037
  Angle = 360
  AttacherType = Attacher::AttachEngine3D
  FirstAngle = 0
  Height = 10
  Placement = pos=(22,17,-22) rot=(0,0,1;0rad)
  Radius = 1.6
  SecondAngle = 0
FEATURE [Part::Cut] Cut029
  Base = -> Box041
  Refine = true
  Tool = -> Cylinder037
FEATURE [Part::Cylinder] Cylinder038
  Angle = 360
  AttacherType = Attacher::AttachEngine3D
  FirstAngle = 0
  Height = 10
  Placement = pos=(22,17,-22) rot=(0,0,1;0rad)
  Radius = 1.6
  SecondAngle = 0
FEATURE [Part::Cut] Cut030
  Base = -> Box042
  Placement = pos=(0,34,0) rot=(0,0,1;3.14159rad)
  Refine = true
  Tool = -> Cylinder038
FEATURE [Part::MultiFuse] Fusion024  label="m2_cyl"
  Shapes = -> [Cylinder035,Cylinder036]
FEATURE [Part::Feature] Part__Feature358  label="SMA_f"
  Placement = pos=(0,33.5,0) rot=(1,0,0;4.71239rad)
  shape: bbox 7.333 x 19.05 x 7.333 mm, 216 faces (baked)
FEATURE [Part::Feature] Part__Feature359  label="SMA_m"
  Placement = pos=(0,-9,-2.2e-15) rot=(1,0,0;1.5708rad)
  shape: bbox 8.901 x 11.09 x 8.901 mm, 66 faces (baked)
FEATURE [Part::Feature] Part__Feature360  label="M3.5"
  Placement = pos=(0,7,9) rot=(0,0,1;0rad)
  shape: bbox 7.514 x 7.514 x 8.144 mm, 85 faces (baked)
FEATURE [Sketcher::SketchObject] Sketch019
  ArcFitTolerance = 0
  FullyConstrained = true
  MakeInternals = false
  Placement = pos=(0,0,0) rot=(1,0,0;1.5708rad)
  sketch-geometry (4):
    g0: LineSegment StartX=-5.75 StartY=-10 StartZ=0 EndX=5.75 EndY=-10 EndZ=0
    g1: LineSegment StartX=-5.75 StartY=10 StartZ=0 EndX=5.75 EndY=10 EndZ=0
    g2: ArcOfCircle CenterX=0 CenterY=-1e-16 CenterZ=0 NormalX=0 NormalY=0 NormalZ=1 AngleXU=0 Radius=11.5353 StartAngle=2.09263 EndAngle=4.19055
    g3: ArcOfCircle CenterX=0 CenterY=-1.2e-15 CenterZ=0 NormalX=0 NormalY=0 NormalZ=1 AngleXU=0 Radius=11.5353 StartAngle=5.23422 EndAngle=7.33215
  constraints (12):
    c: Symmetric(g1,g1,g-2)
    c: Symmetric(g0,g0,g-2)
    c: Distance(g1) = 11.5
    c: Distance(g0) = 11.5
    c: Distance(g1,g0) = 20
    c: Distance(g1,g-1) = 10
    c: Coincident(g2,g1)
    c: Coincident(g2,g0)
    c: Coincident(g3,g1)
    c: Coincident(g3,g0)
    c: PointOnObject(g2,g-2)
    c: PointOnObject(g3,g-2)
FEATURE [Part::Extrusion] Extrude019
  Base = -> Sketch019
  Dir = (0,-1,2e-16)
  DirMode = 2
  FaceMakerClass = Part::FaceMakerBullseye
  FaceMakerMode = 3
  LengthFwd = 23
  LengthRev = 0
  Reversed = true
  Solid = true
  Symmetric = false
FEATURE [Sketcher::SketchObject] Sketch020
  ArcFitTolerance = 0
  FullyConstrained = true
  MakeInternals = false
  Placement = pos=(0,0,0) rot=(1,0,0;1.5708rad)
  sketch-geometry (16):
    g0: LineSegment StartX=-7.5 StartY=-10 StartZ=0 EndX=-7.5 EndY=-16 EndZ=0
    g1: LineSegment StartX=-7.5 StartY=-16 StartZ=0 EndX=7.5 EndY=-16 EndZ=0
    g2: LineSegment StartX=7.5 StartY=-16 StartZ=0 EndX=7.5 EndY=-10 EndZ=0
    g3: ArcOfCircle CenterX=-2e-16 CenterY=11.88 CenterZ=0 NormalX=0 NormalY=0 NormalZ=1 AngleXU=0 Radius=6.64493 StartAngle=6.14733 EndAngle=9.56064
    g4: ArcOfCircle CenterX=0.265981 CenterY=0.194065 CenterZ=0 NormalX=0 NormalY=0 NormalZ=1 AngleXU=0 Radius=12.5 StartAngle=5.32955 EndAngle=7.32412
    g5: ArcOfCircle CenterX=-0.265981 CenterY=0.194065 CenterZ=0 NormalX=0 NormalY=0 NormalZ=1 AngleXU=0 Radius=12.5 StartAngle=2.10066 EndAngle=4.09523
    g6: ArcOfCircle CenterX=-1e-16 CenterY=12.4177 CenterZ=0 NormalX=0 NormalY=0 NormalZ=1 AngleXU=0 Radius=10.1 StartAngle=6.14235 EndAngle=9.56561
    g7: ArcOfCircle CenterX=-2.59139 CenterY=0.317652 CenterZ=0 NormalX=0 NormalY=0 NormalZ=1 AngleXU=0 Radius=13 StartAngle=2.17717 EndAngle=4.0584
    g8: ArcOfCircle CenterX=2.59139 CenterY=0.317652 CenterZ=0 NormalX=0 NormalY=0 NormalZ=1 AngleXU=0 Radius=13 StartAngle=5.36637 EndAngle=7.24761
    g9: LineSegment StartX=10.5 StartY=-10 StartZ=0 EndX=10.5 EndY=-13 EndZ=0
    g10: LineSegment StartX=10.5 StartY=-13 StartZ=0 EndX=15 EndY=-13 EndZ=0
    g11: LineSegment StartX=15 StartY=-13 StartZ=0 EndX=15 EndY=-20 EndZ=0
    g12: LineSegment StartX=-10.5 StartY=-10 StartZ=0 EndX=-10.5 EndY=-13 EndZ=0
    g13: LineSegment StartX=-10.5 StartY=-13 StartZ=0 EndX=-15 EndY=-13 EndZ=0
    g14: LineSegment StartX=-15 StartY=-13 StartZ=0 EndX=-15 EndY=-20 EndZ=0
    g15: LineSegment StartX=-15 StartY=-20 StartZ=0 EndX=15 EndY=-20 EndZ=0
  constraints (51):
    c: Vertical(g0)
    c: Coincident(g1,g0)
    c: Coincident(g2,g1)
    c: Vertical(g2)
    c: Coincident(g4,g3)
    c: Coincident(g4,g2)
    c: Coincident(g5,g3)
    c: Coincident(g5,g0)
    c: Distance(g0,g-1) = 16
    c: Distance(g0,g-2) = 7.5
    c: Symmetric(g0,g1,g-2)
    c: Distance(g0) = 6
    c: Distance(g2) = 6
    c: Diameter(g4) = 25
    c: Diameter(g5) = 25
    c: Symmetric(g3,g3,g-2)
    c: Distance(g3,g0) = 21
    c: Distance(g3,g-1) = 10.98
    c: Distance(g3,g-1) = 11.88
    c: Coincident(g7,g6)
    c: Coincident(g8,g6)
    c: Coincident(g9,g8)
    c: Vertical(g9)
    c: Coincident(g10,g9)
    c: Horizontal(g10)
    c: Coincident(g11,g10)
    c: Vertical(g11)
    c: Coincident(g12,g7)
    c: Vertical(g12)
    c: Coincident(g13,g12)
    c: Horizontal(g13)
    c: Coincident(g14,g13)
    c: Vertical(g14)
    c: Coincident(g15,g14)
    c: Coincident(g15,g11)
    c: Symmetric(g14,g11,g-2)
    c: Distance(g14,g-1) = 20
    c: Distance(g14) = 7
    c: Distance(g11) = 7
    c: Distance(g15) = 30
    c: Distance(g12,g0) = 3
    c: Distance(g9,g2) = 3
    c: Distance(g6,g-1) = 11
    c: Distance(g6,g-2) = 10
    c: Distance(g6,g-1) = 11
    c: Distance(g6,g-2) = 10
    c: Distance(g12) = 3
    c: Distance(g9) = 3
    c: Diameter(g8) = 26
    c: Diameter(g7) = 26
    c: Diameter(g6) = 20.2
FEATURE [Part::Extrusion] Extrude020  label="outer_case"
  Base = -> Sketch020
  Dir = (0,-1,2e-16)
  DirMode = 2
  FaceMakerClass = Part::FaceMakerBullseye
  FaceMakerMode = 3
  LengthFwd = 28
  LengthRev = 0
  Placement = pos=(0,3,0) rot=(0,0,1;0rad)
  Reversed = true
  Solid = true
  Symmetric = false
FEATURE [Part::Cut] Cut027  label="Outer_Case"
  Base = -> Extrude020
  Tool = -> Fusion024
FEATURE [Part::Cut] Cut028  label="Outer"
  Base = -> Cut027
  Tool = -> Box040
FEATURE [Sketcher::SketchObject] Sketch021
  ArcFitTolerance = 0
  FullyConstrained = true
  MakeInternals = false
  Placement = pos=(0,0,0) rot=(1,0,0;1.5708rad)
  sketch-geometry (11):
    g0: ArcOfCircle CenterX=-1e-16 CenterY=12.4177 CenterZ=0 NormalX=0 NormalY=0 NormalZ=1 AngleXU=0 Radius=10.1 StartAngle=6.14235 EndAngle=9.56561
    g1: ArcOfCircle CenterX=-2.59139 CenterY=0.317652 CenterZ=0 NormalX=0 NormalY=0 NormalZ=1 AngleXU=0 Radius=13 StartAngle=2.17717 EndAngle=4.0584
    g2: ArcOfCircle CenterX=2.59139 CenterY=0.317652 CenterZ=0 NormalX=0 NormalY=0 NormalZ=1 AngleXU=0 Radius=13 StartAngle=5.36637 EndAngle=7.24761
    g3: LineSegment StartX=10.5 StartY=-10 StartZ=0 EndX=10.5 EndY=-13 EndZ=0
    g4: LineSegment StartX=10.5 StartY=-13 StartZ=0 EndX=15 EndY=-13 EndZ=0
    g5: LineSegment StartX=15 StartY=-13 StartZ=0 EndX=15 EndY=-20 EndZ=0
    g6: LineSegment StartX=-10.5 StartY=-10 StartZ=0 EndX=-10.5 EndY=-13 EndZ=0
    g7: LineSegment StartX=-10.5 StartY=-13 StartZ=0 EndX=-15 EndY=-13 EndZ=0
    g8: LineSegment StartX=-15 StartY=-13 StartZ=0 EndX=-15 EndY=-20 EndZ=0
    g9: LineSegment StartX=-15 StartY=-20 StartZ=0 EndX=15 EndY=-20 EndZ=0
    g10: Circle CenterX=0 CenterY=0 CenterZ=0 NormalX=0 NormalY=0 NormalZ=1 AngleXU=0 Radius=5
  constraints (34):
    c: Coincident(g1,g0)
    c: Coincident(g2,g0)
    c: Coincident(g3,g2)
    c: Vertical(g3)
    c: Coincident(g4,g3)
    c: Horizontal(g4)
    c: Coincident(g5,g4)
    c: Vertical(g5)
    c: Coincident(g6,g1)
    c: Vertical(g6)
    c: Coincident(g7,g6)
    c: Horizontal(g7)
    c: Coincident(g8,g7)
    c: Vertical(g8)
    c: Coincident(g9,g8)
    c: Coincident(g9,g5)
    c: Symmetric(g8,g5,g-2)
    c: Distance(g8,g-1) = 20
    c: Distance(g8) = 7
    c: Distance(g5) = 7
    c: Distance(g9) = 30
    c: Distance(g0,g-1) = 11
    c: Distance(g0,g-2) = 10
    c: Distance(g0,g-1) = 11
    c: Distance(g0,g-2) = 10
    c: Distance(g6) = 3
    c: Distance(g3) = 3
    c: Diameter(g2) = 26
    c: Diameter(g1) = 26
    c: Diameter(g0) = 20.2
    c: Distance(g4) = 4.5
    c: Distance(g7) = 4.5
    c: Coincident(g-1,g10)
    c: Diameter(g10) = 10
FEATURE [Part::Extrusion] Extrude021  label="Front_cover"
  Base = -> Sketch021
  Dir = (0,-1,2e-16)
  DirMode = 2
  FaceMakerClass = Part::FaceMakerBullseye
  FaceMakerMode = 3
  LengthFwd = 3
  LengthRev = 0
  Reversed = true
  Solid = true
  Symmetric = false
FEATURE [Part::MultiFuse] Fusion026
  Refine = true
  Shapes = -> [Cut028,Extrude021,Cut030,Cut029]
FEATURE [Part::Cut] Cut031  label="OuterBox"
  Base = -> Fusion026
  Refine = true
  Tool = -> Box043
FEATURE [Sketcher::SketchObject] Sketch022
  ArcFitTolerance = 0
  FullyConstrained = true
  MakeInternals = false
  Placement = pos=(0,0,0) rot=(1,0,0;1.5708rad)
  sketch-geometry (14):
    g0: ArcOfCircle CenterX=0 CenterY=12.4177 CenterZ=0 NormalX=0 NormalY=0 NormalZ=1 AngleXU=0 Radius=10.1 StartAngle=6.14235 EndAngle=9.56561
    g1: ArcOfCircle CenterX=-2.59139 CenterY=0.317652 CenterZ=0 NormalX=0 NormalY=0 NormalZ=1 AngleXU=0 Radius=13 StartAngle=2.17717 EndAngle=4.0584
    g2: ArcOfCircle CenterX=2.59139 CenterY=0.317652 CenterZ=0 NormalX=0 NormalY=0 NormalZ=1 AngleXU=0 Radius=13 StartAngle=5.36637 EndAngle=7.24761
    g3: LineSegment StartX=10.5 StartY=-10 StartZ=0 EndX=10.5 EndY=-13 EndZ=0
    g4: LineSegment StartX=10.5 StartY=-13 StartZ=0 EndX=15 EndY=-13 EndZ=0
    g5: LineSegment StartX=15 StartY=-13 StartZ=0 EndX=15 EndY=-20 EndZ=0
    g6: LineSegment StartX=-10.5 StartY=-10 StartZ=0 EndX=-10.5 EndY=-13 EndZ=0
    g7: LineSegment StartX=-10.5 StartY=-13 StartZ=0 EndX=-15 EndY=-13 EndZ=0
    g8: LineSegment StartX=-15 StartY=-13 StartZ=0 EndX=-15 EndY=-20 EndZ=0
    g9: LineSegment StartX=-15 StartY=-20 StartZ=0 EndX=15 EndY=-20 EndZ=0
    g10: Circle CenterX=0 CenterY=0 CenterZ=0 NormalX=0 NormalY=0 NormalZ=1 AngleXU=0 Radius=5
    g11: Circle CenterX=0 CenterY=12.4177 CenterZ=0 NormalX=0 NormalY=0 NormalZ=1 AngleXU=0 Radius=4.5
    g12: Circle CenterX=-10.8747 CenterY=-16.5 CenterZ=0 NormalX=0 NormalY=0 NormalZ=1 AngleXU=0 Radius=1.25
    g13: Circle CenterX=10.8747 CenterY=-16.5 CenterZ=0 NormalX=0 NormalY=0 NormalZ=1 AngleXU=0 Radius=1.25
  constraints (41):
    c: Coincident(g1,g0)
    c: Coincident(g2,g0)
    c: Coincident(g3,g2)
    c: Vertical(g3)
    c: Coincident(g4,g3)
    c: Horizontal(g4)
    c: Coincident(g5,g4)
    c: Vertical(g5)
    c: Coincident(g6,g1)
    c: Vertical(g6)
    c: Coincident(g7,g6)
    c: Horizontal(g7)
    c: Coincident(g8,g7)
    c: Vertical(g8)
    c: Coincident(g9,g8)
    c: Coincident(g9,g5)
    c: Symmetric(g8,g5,g-2)
    c: Distance(g8,g-1) = 20
    c: Distance(g8) = 7
    c: Distance(g5) = 7
    c: Distance(g9) = 30
    c: Distance(g0,g-1) = 11
    c: Distance(g0,g-2) = 10
    c: Distance(g0,g-1) = 11
    c: Distance(g0,g-2) = 10
    c: Distance(g6) = 3
    c: Distance(g3) = 3
    c: Diameter(g2) = 26
    c: Diameter(g1) = 26
    c: Diameter(g0) = 20.2
    c: Distance(g4) = 4.5
    c: Distance(g7) = 4.5
    c: Coincident(g-1,g10)
    c: Diameter(g10) = 10
    c: Coincident(g11,g0)
    c: Diameter(g11) = 9
    c: Distance(g12,g-1) = 16.5
    c: Diameter(g13) = 2.5
    c: Diameter(g12) = 2.5
    c: Symmetric(g12,g13,g-2)
    c: Distance(g13,g3) = 3.52
FEATURE [Part::Extrusion] Extrude022  label="Back_cover"
  Base = -> Sketch022
  Dir = (0,-1,2e-16)
  DirMode = 2
  FaceMakerClass = Part::FaceMakerBullseye
  FaceMakerMode = 3
  LengthFwd = 3
  LengthRev = 0
  Placement = pos=(0,31,0) rot=(0,0,1;0rad)
  Reversed = true
  Solid = true
  Symmetric = false
FEATURE [Part::MultiFuse] Fusion025  label="bck"
  Shapes = -> [Box039,Extrude022]
FEATURE [Part::Cut] Cut032  label="cover"
  Base = -> Fusion025
  Refine = true
  Tool = -> Box044
FEATURE [App::Part] Part013  label="Case"
  Group = -> [Cylinder035,Cylinder036,Cylinder037,Sketch020,Sketch021,Extrude020,Extrude021,Cylinder038,Cut030,Cut029,Fusion024,Cut027,Cut028,Fusion026,Box040,Box042,Box043,Box041,Cut031,Box039,Sketch022,Extrude022,Fusion025,Box044,Cut032]
  Origin = -> Origin041
FEATURE [Part::FeaturePython] Tube  # WARN: FeaturePython — macro-defined, semantics opaque (R4)
  AttacherType = Attacher::AttachEngine3D
  Height = 16
  InnerRadius = 3.4
  OuterRadius = 3.5
  Placement = pos=(0,27,13.5) rot=(1,0,0;1.5708rad)
FEATURE [Part::MultiFuse] Fusion003
  Shapes = -> [Tube,Extrude019,Cylinder033,Part__Feature358,Part__Feature359,Cylinder034,Part__Feature360]
FEATURE [App::Part] Part012  label="Lightning_Arrestor"
  Group = -> [Cylinder033,Cylinder034,Sketch019,Part__Feature358,Part__Feature359,Tube,Part__Feature360,Extrude019,Fusion003]
  Origin = -> Origin040
  Placement = pos=(0,5.5,0) rot=(0,0,1;0rad)
FEATURE [Part::Compound] Compound004  label="lightningArrester"
  Links = -> [Part012,Part013]
  Placement = pos=(110,140,-87.25) rot=(0,-0.707107,0.707107;3.14159rad)
FEATURE [Part::Compound] Compound005  label="loraWan"
  Links = -> [Part005,Part007]
  Placement = pos=(0,0,57) rot=(0,0,1;0rad)
FEATURE [Part::Box] Box051  label="PCB"
  AttacherType = Attacher::AttachEngine3D
  Height = 107
  Length = 1.5
  Width = 42
FEATURE [Part::Box] Box052  label="Cube028"
  AttacherType = Attacher::AttachEngine3D
  Height = 7
  Length = 10
  Placement = pos=(-10,3.75,8) rot=(0,0,1;0rad)
  Width = 0.5
FEATURE [Part::Box] Box053  label="Cube029"
  AttacherType = Attacher::AttachEngine3D
  Height = 7
  Length = 10
  Placement = pos=(-10,10.75,8) rot=(0,0,1;0rad)
  Width = 0.5
FEATURE [Part::Box] Box054  label="Cube030"
  AttacherType = Attacher::AttachEngine3D
  Height = 7
  Length = 10
  Placement = pos=(-10,3.75,92) rot=(0,0,1;0rad)
  Width = 0.5
FEATURE [Part::Box] Box055  label="Cube031"
  AttacherType = Attacher::AttachEngine3D
  Height = 7
  Length = 10
  Placement = pos=(-10,10.75,92) rot=(0,0,1;0rad)
  Width = 0.5
FEATURE [Part::Box] Box056  label="baseMOunt"
  AttacherType = Attacher::AttachEngine3D
  Height = 64
  Length = 6
  Placement = pos=(106.75,-4,-12) rot=(0,0,1;0rad)
  Width = 21
FEATURE [Part::Box] Box057  label="Cube032"
  AttacherType = Attacher::AttachEngine3D
  Height = 8.9
  Length = 8.2
  Placement = pos=(3.8,15,53.1) rot=(0,0,1;0rad)
  Width = 7
FEATURE [Part::Box] Box058  label="baseMOunt001"
  AttacherType = Attacher::AttachEngine3D
  Height = 23
  Length = 6
  Placement = pos=(106.75,0,9.5) rot=(0,0,1;0rad)
  Width = 17
FEATURE [Part::Box] Box010  label="Cube033"
  AttacherType = Attacher::AttachEngine3D
  Height = 21
  Length = 2
  Placement = pos=(12,15,53.1) rot=(0,0,1;0rad)
  Width = 7
FEATURE [Part::Box] Box059  label="Cube034"
  AttacherType = Attacher::AttachEngine3D
  Height = 4
  Length = 15
  Placement = pos=(66.5,-0.9,22.75) rot=(0,0,1;0rad)
  Width = 6
FEATURE [Part::Cut] Cut038  label="BaseMount"
  Base = -> Box056
  Refine = true
  Tool = -> Box058
FEATURE [Part::Cylinder] Cylinder043  label="Tube001"
  Angle = 360
  AttacherType = Attacher::AttachEngine3D
  FirstAngle = 0
  Height = 67
  Placement = pos=(-7.5,7.5,20) rot=(0,0,1;0rad)
  Radius = 5
  SecondAngle = 0
FEATURE [Part::Cylinder] Cylinder044  label="cap1"
  Angle = 360
  AttacherType = Attacher::AttachEngine3D
  FirstAngle = 0
  Height = 9.82
  Placement = pos=(-1.15e-14,27,45) rot=(0,1,0;4.71239rad)
  Radius = 5.93
  SecondAngle = 0
FEATURE [Part::Cylinder] Cylinder045  label="cap2"
  Angle = 360
  AttacherType = Attacher::AttachEngine3D
  FirstAngle = 0
  Height = 11.56
  Placement = pos=(-1.15e-14,35.52,75) rot=(0,1,0;4.71239rad)
  Radius = 4.175
  SecondAngle = 0
FEATURE [Part::Cylinder] Cylinder046  label="Tube002"
  Angle = 360
  AttacherType = Attacher::AttachEngine3D
  FirstAngle = 0
  Height = 6.35
  Placement = pos=(-7.5,7.5,9.65) rot=(0,0,1;0rad)
  Radius = 3
  SecondAngle = 0
FEATURE [Part::Cylinder] Cylinder047  label="Tube003"
  Angle = 360
  AttacherType = Attacher::AttachEngine3D
  FirstAngle = 0
  Height = 6.35
  Placement = pos=(-7.5,7.5,9.65) rot=(0,0,1;0rad)
  Radius = 3
  SecondAngle = 0
FEATURE [Part::Cylinder] Cylinder048
  Angle = 360
  AttacherType = Attacher::AttachEngine3D
  FirstAngle = 0
  Height = 10
  Placement = pos=(5,3,3) rot=(0,1,0;4.71239rad)
  Radius = 1.6
  SecondAngle = 0
FEATURE [Part::Cylinder] Cylinder049
  Angle = 360
  AttacherType = Attacher::AttachEngine3D
  FirstAngle = 0
  Height = 10
  Placement = pos=(5,39,3) rot=(0,1,0;4.71239rad)
  Radius = 1.6
  SecondAngle = 0
FEATURE [Part::Cylinder] Cylinder050
  Angle = 360
  AttacherType = Attacher::AttachEngine3D
  FirstAngle = 0
  Height = 10
  Placement = pos=(5,3,104) rot=(0,1,0;4.71239rad)
  Radius = 1.6
  SecondAngle = 0
FEATURE [Part::Cylinder] Cylinder051
  Angle = 360
  AttacherType = Attacher::AttachEngine3D
  FirstAngle = 0
  Height = 10
  Placement = pos=(5,39,104) rot=(0,1,0;4.71239rad)
  Radius = 1.6
  SecondAngle = 0
FEATURE [Part::Cylinder] Cylinder052
  Angle = 360
  AttacherType = Attacher::AttachEngine3D
  FirstAngle = 0
  Height = 10
  Placement = pos=(114,6.5,-6) rot=(0,1,0;4.71239rad)
  Radius = 1.6
  SecondAngle = 0
FEATURE [Part::Cylinder] Cylinder053
  Angle = 360
  AttacherType = Attacher::AttachEngine3D
  FirstAngle = 0
  Height = 10
  Placement = pos=(114,6.5,46) rot=(0,1,0;4.71239rad)
  Radius = 1.6
  SecondAngle = 0
FEATURE [Part::Cylinder] Cylinder054
  Angle = 360
  AttacherType = Attacher::AttachEngine3D
  FirstAngle = 0
  Height = 21
  Placement = pos=(7,18.5,71) rot=(0,1,0;1.5708rad)
  Radius = 1.1
  SecondAngle = 0
FEATURE [Part::Cut] Cut042
  Base = -> Box010
  Refine = true
  Tool = -> Cylinder054
FEATURE [Part::MultiFuse] Fusion032  label="bottom_tubehold"
  Refine = true
  Shapes = -> [Box052,Box053]
FEATURE [Part::MultiFuse] Fusion033  label="top_tubehold"
  Refine = true
  Shapes = -> [Box054,Box055]
FEATURE [Part::MultiFuse] Fusion034  label="m3_cyl001"
  Refine = true
  Shapes = -> [Cylinder048,Cylinder049,Cylinder050,Cylinder051]
FEATURE [Part::Cut] Cut037  label="PCB_m3cut"
  Base = -> Box051
  Refine = true
  Tool = -> Fusion034
FEATURE [Part::Fillet] Fillet030  label="pcb"
  Base = -> Cut037
  EdgeLinks = -> Cut037 [Edge9,Edge12,Edge14]
  Edges = 3 edges r=3: [Edge9,Edge12,Edge14]
FEATURE [Part::MultiFuse] Fusion038  label="m3Cyl"
  Refine = true
  Shapes = -> [Cylinder052,Cylinder053]
FEATURE [Part::MultiFuse] Fusion040  label="Cap"
  Refine = true
  Shapes = -> [Box057,Cut042]
FEATURE [Part::Feature] Part__Feature361  label="pins"
  Placement = pos=(7.37732,-14.6706,0.356181) rot=(-1,0,0;1.5708rad)
  shape: bbox 0.64 x 0.64 x 8.5 mm, 12 faces (baked)
FEATURE [Part::Feature] Part__Feature362  label="pins001"
  Placement = pos=(7.37732,-14.6706,0.356181) rot=(-1,0,0;1.5708rad)
  shape: bbox 0.64 x 0.64 x 8.5 mm, 12 faces (baked)
FEATURE [Part::Feature] Part__Feature363  label="pins002"
  Placement = pos=(7.37732,-14.6706,0.356181) rot=(-1,0,0;1.5708rad)
  shape: bbox 0.64 x 0.64 x 8.5 mm, 12 faces (baked)
FEATURE [Part::Feature] Part__Feature364  label="SOLID"
  shape: bbox 9.98 x 5.7 x 7 mm, 38 faces (baked)
FEATURE [Part::Feature] Part__Feature365  label="BOSS-EXTRUDE14_2_"
  Placement = pos=(-3.0192,1.09628,5.395) rot=(0,0,1;0rad)
  shape: bbox 0.6 x 1 x 0.3 mm, 6 faces (baked)
FEATURE [Part::Feature] Part__Feature366  label="BOSS-EXTRUDE14_11_"
  Placement = pos=(-3.0192,1.09628,5.395) rot=(0,0,1;0rad)
  shape: bbox 0.3 x 1 x 0.3 mm, 6 faces (baked)
FEATURE [Part::Feature] Part__Feature367  label="BOSS-EXTRUDE7_7_"
  Placement = pos=(-3.0192,1.09628,5.395) rot=(0,0,1;0rad)
  shape: bbox 0.3 x 3.784 x 0.75 mm, 6 faces (baked)
FEATURE [Part::Feature] Part__Feature368  label="BOSS-EXTRUDE14_9_"
  Placement = pos=(-3.0192,1.09628,5.395) rot=(0,0,1;0rad)
  shape: bbox 0.3 x 1 x 0.3 mm, 6 faces (baked)
FEATURE [Part::Feature] Part__Feature369  label="switch"
  Placement = pos=(-2,36,30) rot=(-0.57735,0.57735,0.57735;2.0944rad)
  shape: bbox 3.5 x 9.656 x 8.5 mm, 169 faces (baked)
FEATURE [Part::Feature] Part__Feature370  label="BOSS-EXTRUDE14_8_"
  Placement = pos=(-3.0192,1.09628,5.395) rot=(0,0,1;0rad)
  shape: bbox 0.6 x 1 x 0.3 mm, 6 faces (baked)
FEATURE [Part::Feature] Part__Feature371  label="BOSS-EXTRUDE7_4_"
  Placement = pos=(-3.0192,1.09628,5.395) rot=(0,0,1;0rad)
  shape: bbox 0.3 x 3.784 x 0.75 mm, 6 faces (baked)
FEATURE [Part::Feature] Part__Feature372  label="BOSS-EXTRUDE7_3_"
  Placement = pos=(-3.0192,1.09628,5.395) rot=(0,0,1;0rad)
  shape: bbox 0.3 x 3.784 x 0.75 mm, 6 faces (baked)
FEATURE [Part::Feature] Part__Feature373  label="BOSS-EXTRUDE14_4_"
  Placement = pos=(-3.0192,1.09628,5.395) rot=(0,0,1;0rad)
  shape: bbox 0.3 x 1 x 0.3 mm, 6 faces (baked)
FEATURE [Part::Feature] Part__Feature374  label="BOSS-EXTRUDE14_3_"
  Placement = pos=(-3.0192,1.09628,5.395) rot=(0,0,1;0rad)
  shape: bbox 0.3 x 1 x 0.3 mm, 6 faces (baked)
FEATURE [Part::Feature] Part__Feature375  label="BOSS-EXTRUDE14_7_"
  Placement = pos=(-3.0192,1.09628,5.395) rot=(0,0,1;0rad)
  shape: bbox 0.6 x 1 x 0.3 mm, 6 faces (baked)
FEATURE [Part::Feature] Part__Feature376  label="MIRROR2"
  Placement = pos=(-3.0192,1.09628,5.395) rot=(0,0,1;0rad)
  shape: bbox 6.7 x 4.6 x 0.7 mm, 26 faces (baked)
FEATURE [Part::Feature] Part__Feature377  label="BOSS-EXTRUDE14_5_"
  Placement = pos=(-3.0192,1.09628,5.395) rot=(0,0,1;0rad)
  shape: bbox 0.3 x 1 x 0.3 mm, 6 faces (baked)
FEATURE [Part::Feature] Part__Feature378  label="BOSS-EXTRUDE14_12_"
  Placement = pos=(-3.0192,1.09628,5.395) rot=(0,0,1;0rad)
  shape: bbox 0.3 x 1 x 0.3 mm, 6 faces (baked)
FEATURE [Part::Feature] Part__Feature379  label="BOSS-EXTRUDE7_8_"
  Placement = pos=(-3.0192,1.09628,5.395) rot=(0,0,1;0rad)
  shape: bbox 0.3 x 3.784 x 0.75 mm, 6 faces (baked)
FEATURE [Part::Feature] Part__Feature380  label="BOSS-EXTRUDE7_1_"
  Placement = pos=(-3.0192,1.09628,5.395) rot=(0,0,1;0rad)
  shape: bbox 0.3 x 3.784 x 0.75 mm, 6 faces (baked)
FEATURE [Part::Feature] Part__Feature381  label="BOSS-EXTRUDE14_10_"
  Placement = pos=(-3.0192,1.09628,5.395) rot=(0,0,1;0rad)
  shape: bbox 0.3 x 1 x 0.3 mm, 6 faces (baked)
FEATURE [Part::Feature] Part__Feature382  label="BOSS-EXTRUDE7_9_"
  Placement = pos=(-3.0192,1.09628,5.395) rot=(0,0,1;0rad)
  shape: bbox 0.3 x 3.784 x 0.75 mm, 6 faces (baked)
FEATURE [Part::Feature] Part__Feature383  label="BOSS-EXTRUDE14_6_"
  Placement = pos=(-3.0192,1.09628,5.395) rot=(0,0,1;0rad)
  shape: bbox 0.6 x 1 x 0.3 mm, 6 faces (baked)
FEATURE [Part::Feature] Part__Feature384  label="CHAMFER9"
  Placement = pos=(-3.0192,1.09628,5.395) rot=(0,0,1;0rad)
  shape: bbox 8.94 x 7.3 x 4.2 mm, 103 faces (baked)
FEATURE [Part::Feature] Part__Feature385  label="BOSS-EXTRUDE14_1_"
  Placement = pos=(-3.0192,1.09628,5.395) rot=(0,0,1;0rad)
  shape: bbox 0.3 x 1 x 0.3 mm, 6 faces (baked)
FEATURE [Part::Feature] Part__Feature386  label="BOSS-EXTRUDE7_6_"
  Placement = pos=(-3.0192,1.09628,5.395) rot=(0,0,1;0rad)
  shape: bbox 0.3 x 3.784 x 0.75 mm, 6 faces (baked)
FEATURE [Part::Feature] Part__Feature387  label="BOSS-EXTRUDE7_2_"
  Placement = pos=(-3.0192,1.09628,5.395) rot=(0,0,1;0rad)
  shape: bbox 0.3 x 3.784 x 0.75 mm, 6 faces (baked)
FEATURE [Part::Feature] Part__Feature388  label="CUT-EXTRUDE5"
  Placement = pos=(-3.0192,1.09628,5.395) rot=(0,0,1;0rad)
  shape: bbox 8.867 x 2 x 3.668 mm, 129 faces (baked)
FEATURE [Part::Feature] Part__Feature389  label="BOSS-EXTRUDE7_5_"
  Placement = pos=(-3.0192,1.09628,5.395) rot=(0,0,1;0rad)
  shape: bbox 0.3 x 3.784 x 0.75 mm, 6 faces (baked)
FEATURE [Part::Feature] Part__Feature390  label="Shield"
  shape: bbox 10.6 x 2.7 x 12.6 mm, 38 faces (baked)
FEATURE [Part::Feature] Part__Feature391  label="Body004"
  Placement = pos=(0,0,0.1) rot=(0,0,1;0rad)
  shape: bbox 2.6 x 1.6 x 0.6302 mm, 6 faces (baked)
FEATURE [Part::Feature] Part__Feature392  label="Pins"
  shape: bbox 0.4402 x 0.4402 x 0.1002 mm, 6 faces (baked)
FEATURE [Part::Feature] Part__Feature393  label="Pins001"
  shape: bbox 0.44 x 0.44 x 0.1 mm, 6 faces (baked)
FEATURE [Part::Feature] Part__Feature394  label="Pins002"
  shape: bbox 0.44 x 0.44 x 0.1 mm, 6 faces (baked)
FEATURE [Part::Feature] Part__Feature395  label="Pins003"
  shape: bbox 0.44 x 0.44 x 0.1 mm, 6 faces (baked)
FEATURE [Part::Feature] Part__Feature396  label="Body005"
  Placement = pos=(0,0,0.1) rot=(0,0,1;0rad)
  shape: bbox 2.6 x 1.6 x 0.6302 mm, 6 faces (baked)
FEATURE [Part::Feature] Part__Feature397  label="Pins005"
  shape: bbox 0.44 x 0.44 x 0.1 mm, 6 faces (baked)
FEATURE [Part::Feature] Part__Feature398  label="Pins006"
  shape: bbox 0.44 x 0.44 x 0.1 mm, 6 faces (baked)
FEATURE [Part::Feature] Part__Feature399  label="Pins007"
  shape: bbox 0.4402 x 0.4402 x 0.1002 mm, 6 faces (baked)
FEATURE [Part::Feature] Part__Feature400  label="Pins008"
  shape: bbox 0.44 x 0.44 x 0.1 mm, 6 faces (baked)
FEATURE [Part::Feature] Part__Feature401  label="U.FL-R-SMT-1_10_ v1"
  Placement = pos=(-6.95174,1,-10.8381) rot=(-1,0,0;1.5708rad)
  shape: bbox 3.002 x 1.252 x 3.102 mm, 67 faces (baked)
FEATURE [Part::Feature] Part__Feature402  label="SOLID001"
  shape: bbox 20.96 x 1.25 x 17.78 mm, 345 faces (baked)
FEATURE [Part::Feature] Part__Feature403  label="1_Male_Pin_2.54_mm"
  Placement = pos=(3.87631,2.25619,11.0637) rot=(0,0,1;0rad)
  shape: bbox 2.54 x 11.1 x 2.4 mm, 32 faces (baked)
FEATURE [Part::Feature] Part__Feature404  label="1_Male_Pin_2.54_mm001"
  Placement = pos=(1.33631,2.25619,11.0637) rot=(0,0,1;0rad)
  shape: bbox 2.54 x 11.1 x 2.4 mm, 32 faces (baked)
FEATURE [Part::Feature] Part__Feature405  label="1_Male_Pin_2.54_mm002"
  Placement = pos=(-1.20369,2.25619,11.0637) rot=(0,0,1;0rad)
  shape: bbox 2.54 x 11.1 x 2.4 mm, 32 faces (baked)
FEATURE [Part::Feature] Part__Feature406  label="1_Male_Pin_2.54_mm003"
  Placement = pos=(-3.74369,2.25619,11.0637) rot=(0,0,1;0rad)
  shape: bbox 2.54 x 11.1 x 2.4 mm, 32 faces (baked)
FEATURE [Part::Feature] Part__Feature407  label="1_Male_Pin_2.54_mm004"
  Placement = pos=(-6.28369,2.25619,11.0637) rot=(0,0,1;0rad)
  shape: bbox 2.54 x 11.1 x 2.4 mm, 32 faces (baked)
FEATURE [Part::Feature] Part__Feature408  label="1_Male_Pin_2.54_mm005"
  Placement = pos=(-8.82369,2.25619,11.0637) rot=(0,0,1;0rad)
  shape: bbox 2.54 x 11.1 x 2.4 mm, 32 faces (baked)
FEATURE [Part::Feature] Part__Feature409  label="1_Male_Pin_2.54_mm006"
  Placement = pos=(-11.3637,2.25619,11.0637) rot=(0,0,1;0rad)
  shape: bbox 2.54 x 11.1 x 2.4 mm, 32 faces (baked)
FEATURE [Part::Feature] Part__Feature049  label="1_Male_Pin_2.54_mm007"
  Placement = pos=(3.87631,2.25619,11.0637) rot=(0,0,1;0rad)
  shape: bbox 2.54 x 11.1 x 2.4 mm, 32 faces (baked)
FEATURE [Part::Feature] Part__Feature050  label="1_Male_Pin_2.54_mm008"
  Placement = pos=(1.33631,2.25619,11.0637) rot=(0,0,1;0rad)
  shape: bbox 2.54 x 11.1 x 2.4 mm, 32 faces (baked)
FEATURE [Part::Feature] Part__Feature051  label="1_Male_Pin_2.54_mm009"
  Placement = pos=(-1.20369,2.25619,11.0637) rot=(0,0,1;0rad)
  shape: bbox 2.54 x 11.1 x 2.4 mm, 32 faces (baked)
FEATURE [Part::Feature] Part__Feature052  label="1_Male_Pin_2.54_mm010"
  Placement = pos=(-3.74369,2.25619,11.0637) rot=(0,0,1;0rad)
  shape: bbox 2.54 x 11.1 x 2.4 mm, 32 faces (baked)
FEATURE [Part::Feature] Part__Feature053  label="1_Male_Pin_2.54_mm011"
  Placement = pos=(-6.28369,2.25619,11.0637) rot=(0,0,1;0rad)
  shape: bbox 2.54 x 11.1 x 2.4 mm, 32 faces (baked)
FEATURE [Part::Feature] Part__Feature054  label="1_Male_Pin_2.54_mm012"
  Placement = pos=(-8.82369,2.25619,11.0637) rot=(0,0,1;0rad)
  shape: bbox 2.54 x 11.1 x 2.4 mm, 32 faces (baked)
FEATURE [Part::Feature] Part__Feature055  label="1_Male_Pin_2.54_mm013"
  Placement = pos=(-11.3637,2.25619,11.0637) rot=(0,0,1;0rad)
  shape: bbox 2.54 x 11.1 x 2.4 mm, 32 faces (baked)
FEATURE [Part::Feature] Part__Feature058  label="USB C -C0046"
  Placement = pos=(6.7,20.1,32) rot=(-0.57735,0.57735,0.57735;2.0944rad)
  shape: bbox 6.63 x 11.9 x 40.53 mm, 28 faces (baked)
FEATURE [App::Part] Pins  label="Pins004"
  Group = -> [Part__Feature392,Part__Feature393,Part__Feature394,Part__Feature395]
  Origin = -> Origin048
FEATURE [App::Part] Pins001  label="Pins009"
  Group = -> [Part__Feature397,Part__Feature398,Part__Feature399,Part__Feature400]
  Origin = -> Origin009
FEATURE [App::Part] SKTAAAE010_v002  label="SKTAAAE010 v002"
  Group = -> [Part__Feature396,Pins001]
  Origin = -> Origin010
  Placement = pos=(10.6911,1,-0.186818) rot=(-1,0,0;1.5708rad)
FEATURE [App::Part] SKTAAAE010_v1  label="SKTAAAE010 v1"
  Group = -> [Part__Feature391,Pins]
  Origin = -> Origin049
  Placement = pos=(10.7092,1,-12.0449) rot=(-1,0,0;1.5708rad)
FEATURE [Sketcher::SketchObject] Sketch024
  ArcFitTolerance = 1e-06
  FullyConstrained = true
  MakeInternals = false
  Placement = pos=(0,0,0) rot=(0.57735,0.57735,0.57735;2.0944rad)
  sketch-geometry (8):
    g0: LineSegment StartX=0 StartY=0 StartZ=0 EndX=106.75 EndY=0 EndZ=0
    g1: LineSegment StartX=106.75 StartY=0 StartZ=0 EndX=106.75 EndY=41.75 EndZ=0
    g2: LineSegment StartX=106.75 StartY=41.75 StartZ=0 EndX=0 EndY=41.75 EndZ=0
    g3: LineSegment StartX=0 StartY=41.75 StartZ=0 EndX=0 EndY=0 EndZ=0
    g4: Circle CenterX=3 CenterY=3 CenterZ=0 NormalX=0 NormalY=0 NormalZ=1 AngleXU=0 Radius=1.55
    g5: Circle CenterX=3 CenterY=38.75 CenterZ=0 NormalX=0 NormalY=0 NormalZ=1 AngleXU=0 Radius=1.55
    g6: Circle CenterX=103.75 CenterY=38.75 CenterZ=0 NormalX=0 NormalY=0 NormalZ=1 AngleXU=0 Radius=1.55
    g7: Circle CenterX=103.75 CenterY=3 CenterZ=0 NormalX=0 NormalY=0 NormalZ=1 AngleXU=0 Radius=1.55
  constraints (23):
    c: Coincident(g0,g1)
    c: Coincident(g1,g2)
    c: Coincident(g2,g3)
    c: Coincident(g3,g0)
    c: Horizontal(g0)
    c: Horizontal(g2)
    c: Vertical(g1)
    c: Vertical(g3)
    c: Coincident(g0,g-1)
    c: Distance(g3) = 41.75
    c: Distance(g0) = 106.75
    c: Distance(g4,g0) = 3
    c: Distance(g4,g-2) = 3
    c: Distance(g5,g-2) = 3
    c: Distance(g5,g-1) = 38.75
    c: Distance(g7,g-2) = 103.75
    c: Distance(g7,g-1) = 3
    c: Distance(g6,g-2) = 103.75
    c: Distance(g6,g-1) = 38.75
    c: Equal(g4,g5)
    c: Equal(g4,g6)
    c: Equal(g4,g7)
    c: Diameter(g4) = 3.1
FEATURE [Part::Extrusion] Extrude024  label="Bottom001"
  Base = -> Sketch024
  Dir = (1,0,0)
  DirMode = 2
  FaceMakerClass = Part::FaceMakerBullseye
  FaceMakerMode = 3
  LengthFwd = 8
  LengthRev = 0
  Placement = pos=(0,4,0) rot=(0,0,1;4.71239rad)
  Solid = true
  Symmetric = false
FEATURE [Part::MultiFuse] Fusion037  label="Mount"
  Refine = true
  Shapes = -> [Cut038,Extrude024]
FEATURE [Part::Cut] Cut039  label="Mount_m3Cut"
  Base = -> Fusion037
  Refine = true
  Tool = -> Fusion038
FEATURE [Sketcher::SketchObject] Sketch025
  ArcFitTolerance = 1e-06
  FullyConstrained = true
  MakeInternals = false
  Placement = pos=(0,0,0) rot=(0.57735,0.57735,0.57735;2.0944rad)
  sketch-geometry (12):
    g0: LineSegment StartX=106.25 StartY=0 StartZ=0 EndX=106.25 EndY=41.75 EndZ=0
    g1: LineSegment StartX=106.25 StartY=41.75 StartZ=0 EndX=0 EndY=41.75 EndZ=0
    g2: LineSegment StartX=3.8e-15 StartY=41.75 StartZ=0 EndX=3.8e-15 EndY=0 EndZ=0
    g3: Circle CenterX=3 CenterY=3 CenterZ=0 NormalX=0 NormalY=0 NormalZ=1 AngleXU=0 Radius=1.55
    g4: Circle CenterX=3 CenterY=38.75 CenterZ=0 NormalX=0 NormalY=0 NormalZ=1 AngleXU=0 Radius=1.55
    g5: Circle CenterX=103.75 CenterY=38.75 CenterZ=0 NormalX=0 NormalY=0 NormalZ=1 AngleXU=0 Radius=1.55
    g6: Circle CenterX=103.75 CenterY=3 CenterZ=0 NormalX=0 NormalY=0 NormalZ=1 AngleXU=0 Radius=1.55
    g7: LineSegment StartX=3.8e-15 StartY=0 StartZ=0 EndX=18.25 EndY=0 EndZ=0
    g8: LineSegment StartX=18.25 StartY=0 StartZ=0 EndX=18.25 EndY=15 EndZ=0
    g9: LineSegment StartX=18.25 StartY=15 StartZ=0 EndX=88 EndY=15 EndZ=0
    g10: LineSegment StartX=88 StartY=15 StartZ=0 EndX=88 EndY=0 EndZ=0
    g11: LineSegment StartX=88 StartY=0 StartZ=0 EndX=106.25 EndY=0 EndZ=0
  constraints (36):
    c: Coincident(g0,g1)
    c: Coincident(g1,g2)
    c: Horizontal(g1)
    c: Vertical(g0)
    c: Vertical(g2)
    c: Distance(g2) = 41.75
    c: Distance(g3,g-2) = 3
    c: Distance(g4,g-2) = 3
    c: Distance(g4,g-1) = 38.75
    c: Distance(g6,g-2) = 103.75
    c: Distance(g6,g-1) = 3
    c: Distance(g5,g-2) = 103.75
    c: Distance(g5,g-1) = 38.75
    c: Equal(g3,g4)
    c: Equal(g3,g5)
    c: Equal(g3,g6)
    c: Diameter(g3) = 3.1
    c: Coincident(g7,g2)
    c: PointOnObject(g7,g-1)
    c: Horizontal(g7)
    c: Coincident(g8,g7)
    c: Vertical(g8)
    c: Coincident(g9,g8)
    c: Horizontal(g9)
    c: Coincident(g10,g9)
    c: PointOnObject(g10,g-1)
    c: Vertical(g10)
    c: Coincident(g11,g10)
    c: Coincident(g11,g0)
    c: Horizontal(g11)
    c: Distance(g7) = 18.25
    c: Distance(g3,g-1) = 3
    c: Distance(g8) = 15
    c: Distance(g11) = 18.25
    c: Distance(g0,g-2) = 106.25
    c: Distance(g1) = 106.25
FEATURE [Part::Extrusion] Extrude025  label="Top001"
  Base = -> Sketch025
  Dir = (1,0,0)
  DirMode = 2
  FaceMakerClass = Part::FaceMakerBullseye
  FaceMakerMode = 3
  LengthFwd = 4
  LengthRev = 0
  Placement = pos=(0,-17,0) rot=(0,0,1;4.71239rad)
  Solid = true
  Symmetric = false
FEATURE [Sketcher::SketchObject] Sketch026
  ArcFitTolerance = 1e-06
  FullyConstrained = true
  MakeInternals = false
  Placement = pos=(0,0,0) rot=(0.57735,0.57735,0.57735;2.0944rad)
  sketch-geometry (8):
    g0: Circle CenterX=3 CenterY=3 CenterZ=0 NormalX=0 NormalY=0 NormalZ=1 AngleXU=0 Radius=1.55
    g1: Circle CenterX=3 CenterY=38.75 CenterZ=0 NormalX=0 NormalY=0 NormalZ=1 AngleXU=0 Radius=1.55
    g2: Circle CenterX=103.75 CenterY=38.75 CenterZ=0 NormalX=0 NormalY=0 NormalZ=1 AngleXU=0 Radius=1.55
    g3: Circle CenterX=103.75 CenterY=3 CenterZ=0 NormalX=0 NormalY=0 NormalZ=1 AngleXU=0 Radius=1.55
    g4: Circle CenterX=3 CenterY=38.75 CenterZ=0 NormalX=0 NormalY=0 NormalZ=1 AngleXU=0 Radius=2.875
    g5: Circle CenterX=3 CenterY=3 CenterZ=0 NormalX=0 NormalY=0 NormalZ=1 AngleXU=0 Radius=2.875
    g6: Circle CenterX=103.75 CenterY=3 CenterZ=0 NormalX=0 NormalY=0 NormalZ=1 AngleXU=0 Radius=2.875
    g7: Circle CenterX=103.75 CenterY=38.75 CenterZ=0 NormalX=0 NormalY=0 NormalZ=1 AngleXU=0 Radius=2.875
  constraints (20):
    c: Distance(g0,g-2) = 3
    c: Distance(g1,g-2) = 3
    c: Distance(g1,g-1) = 38.75
    c: Distance(g3,g-2) = 103.75
    c: Distance(g3,g-1) = 3
    c: Distance(g2,g-2) = 103.75
    c: Distance(g2,g-1) = 38.75
    c: Equal(g0,g1)
    c: Equal(g0,g2)
    c: Equal(g0,g3)
    c: Diameter(g0) = 3.1
    c: Distance(g0,g-1) = 3
    c: Coincident(g4,g1)
    c: Coincident(g5,g0)
    c: Coincident(g6,g3)
    c: Coincident(g7,g2)
    c: Diameter(g7) = 5.75
    c: Diameter(g6) = 5.75
    c: Diameter(g5) = 5.75
    c: Diameter(g4) = 5.75
FEATURE [Part::Extrusion] Extrude026  label="spacer001"
  Base = -> Sketch026
  Dir = (1,0,0)
  DirMode = 2
  FaceMakerClass = Part::FaceMakerBullseye
  FaceMakerMode = 3
  LengthFwd = 15
  LengthRev = 0
  Placement = pos=(0,-2,0) rot=(0,0,1;4.71239rad)
  Solid = true
  Symmetric = false
FEATURE [Part::MultiFuse] Fusion029  label="topSpacer001"
  Refine = true
  Shapes = -> [Extrude025,Extrude026]
FEATURE [Part::Fillet] Fillet029  label="top_fillet001"
  Base = -> Fusion029
  EdgeLinks = -> Fusion029 [Edge1,Edge2,Edge9,Edge12,Edge37,Edge38,Edge39,Edge40]
  Edges = 8 edges r=1: [Edge1,Edge2,Edge9,Edge12,Edge37,Edge38,Edge39,Edge40]
FEATURE [App::Part] Part014  label="GeigerTop001"
  Group = -> [Extrude025,Extrude026,Sketch026,Sketch025,Fusion029,Fillet029]
  Origin = -> Origin042
  Placement = pos=(-3,0,0) rot=(-0.57735,-0.57735,-0.57735;2.0944rad)
FEATURE [Sketcher::SketchObject] Sketch027
  ArcFitTolerance = 1e-06
  FullyConstrained = true
  MakeInternals = false
  Placement = pos=(0,0,0) rot=(0.57735,0.57735,0.57735;2.0944rad)
  sketch-geometry (4):
    g0: LineSegment StartX=14.5491 StartY=71.8507 StartZ=0 EndX=14.5491 EndY=52.2908 EndZ=0
    g1: LineSegment StartX=14.5491 StartY=52.2908 StartZ=0 EndX=22.4289 EndY=52.2908 EndZ=0
    g2: LineSegment StartX=22.4289 StartY=71.8507 StartZ=0 EndX=22.4289 EndY=52.2908 EndZ=0
    g3: LineSegment StartX=14.5491 StartY=71.8507 StartZ=0 EndX=22.4289 EndY=71.8507 EndZ=0
  constraints (11):
    c: Vertical(g0)
    c: Coincident(g1,g0)
    c: Horizontal(g1)
    c: Block(g1)
    c: Coincident(g2,g1)
    c: Vertical(g2)
    c: Coincident(g3,g0)
    c: Coincident(g3,g2)
    c: Horizontal(g3)
    c: Distance(g1) = 7.87986
    c: Block(g0)
FEATURE [App::Part] Part003  label="ESP_Cap"
  Group = -> [Sketch027,Box057,Box010,Cut042,Cylinder054,Fusion040]
  Origin = -> Origin016
FEATURE [Sketcher::SketchObject] Sketch028
  ArcFitTolerance = 1e-06
  FullyConstrained = true
  MakeInternals = false
  Placement = pos=(0,0,0) rot=(0.57735,0.57735,0.57735;2.0944rad)
  sketch-geometry (12):
    g0: LineSegment StartX=10.25 StartY=66.5 StartZ=0 EndX=10.25 EndY=43.25 EndZ=0
    g1: LineSegment StartX=30 StartY=43.25 StartZ=0 EndX=30 EndY=66.5 EndZ=0
    g2: LineSegment StartX=30 StartY=66.5 StartZ=0 EndX=10.25 EndY=66.5 EndZ=0
    g3: LineSegment StartX=10.25 StartY=43.25 StartZ=0 EndX=12.9 EndY=43.25 EndZ=0
    g4: LineSegment StartX=12.9 StartY=43.25 StartZ=0 EndX=12.9 EndY=20.25 EndZ=0
    g5: LineSegment StartX=12.9 StartY=20.25 StartZ=0 EndX=16.15 EndY=20.25 EndZ=0
    g6: LineSegment StartX=16.15 StartY=20.25 StartZ=0 EndX=16.15 EndY=15.25 EndZ=0
    g7: LineSegment StartX=16.15 StartY=15.25 StartZ=0 EndX=24.15 EndY=15.25 EndZ=0
    g8: LineSegment StartX=24.15 StartY=15.25 StartZ=0 EndX=24.15 EndY=20.25 EndZ=0
    g9: LineSegment StartX=24.15 StartY=20.25 StartZ=0 EndX=27.4 EndY=20.25 EndZ=0
    g10: LineSegment StartX=27.4 StartY=20.25 StartZ=0 EndX=27.4 EndY=43.25 EndZ=0
    g11: LineSegment StartX=27.4 StartY=43.25 StartZ=0 EndX=30 EndY=43.25 EndZ=0
  constraints (36):
    c: Coincident(g1,g2)
    c: Coincident(g2,g0)
    c: Vertical(g0)
    c: Vertical(g1)
    c: Horizontal(g2)
    c: Coincident(g3,g0)
    c: Horizontal(g3)
    c: Coincident(g4,g3)
    c: Vertical(g4)
    c: Coincident(g5,g4)
    c: Horizontal(g5)
    c: Coincident(g6,g5)
    c: Vertical(g6)
    c: Coincident(g7,g6)
    c: Horizontal(g7)
    c: Coincident(g8,g7)
    c: Vertical(g8)
    c: Coincident(g9,g8)
    c: Horizontal(g9)
    c: Coincident(g10,g9)
    c: Vertical(g10)
    c: Coincident(g11,g10)
    c: Coincident(g11,g1)
    c: Horizontal(g11)
    c: Distance(g4) = 23
    c: Distance(g4,g-1) = 20.25
    c: Distance(g5) = 3.25
    c: Distance(g6) = 5
    c: Distance(g7) = 8
    c: Distance(g6,g-2) = 16.15
    c: Distance(g8) = 5
    c: Distance(g9) = 3.25
    c: Distance(g10) = 23
    c: Distance(g0,g-2) = 10.25
    c: Distance(g0) = 23.25
    c: Distance(g2) = 19.75
FEATURE [Part::Extrusion] Extrude027
  Base = -> Sketch028
  Dir = (1,0,0)
  DirMode = 2
  FaceMakerClass = Part::FaceMakerBullseye
  FaceMakerMode = 3
  LengthFwd = 5
  LengthRev = 0
  Placement = pos=(0,4,40.25) rot=(-0.57735,0.57735,-0.57735;2.0944rad)
  Solid = true
  Symmetric = false
FEATURE [Part::Cut] Cut040  label="ESP_cut"
  Base = -> Cut039
  Refine = true
  Tool = -> Extrude027
FEATURE [Part::Cut] Cut041  label="LoRa_Cut"
  Base = -> Cut040
  Refine = true
  Tool = -> Box059
FEATURE [Part::Sphere] Sphere
  Angle1 = -90
  Angle2 = 90
  Angle3 = 180
  AttacherType = Attacher::AttachEngine3D
  Placement = pos=(-7.5,7.5,20) rot=(1,0,0;4.71239rad)
  Radius = 5
FEATURE [Part::Sphere] Sphere001
  Angle1 = -90
  Angle2 = 90
  Angle3 = 180
  AttacherType = Attacher::AttachEngine3D
  Placement = pos=(-7.5,7.5,87) rot=(-1,0,0;4.71239rad)
  Radius = 5
FEATURE [Part::Sphere] Sphere002
  Angle1 = -90
  Angle2 = 90
  Angle3 = 180
  AttacherType = Attacher::AttachEngine3D
  Placement = pos=(-7.5,7.5,9.65) rot=(1,0,0;4.71239rad)
  Radius = 3
FEATURE [Part::MultiFuse] Fusion030  label="bottomend"
  Refine = true
  Shapes = -> [Cylinder046,Sphere002]
FEATURE [Part::Sphere] Sphere003
  Angle1 = -90
  Angle2 = 90
  Angle3 = 180
  AttacherType = Attacher::AttachEngine3D
  Placement = pos=(-7.5,7.5,9.65) rot=(1,0,0;4.71239rad)
  Radius = 3
FEATURE [Part::MultiFuse] Fusion031  label="topend"
  Placement = pos=(0,15,107) rot=(1,0,0;3.14159rad)
  Refine = true
  Shapes = -> [Cylinder047,Sphere003]
FEATURE [Part::MultiFuse] Fusion035  label="Tube004"
  Refine = true
  Shapes = -> [Cylinder043,Sphere,Sphere001,Fusion030,Fusion031,Fusion032,Fusion033]
FEATURE [Part::FeaturePython] Tube003  label="Tube007"  # WARN: FeaturePython — macro-defined, semantics opaque (R4)
  AttacherType = Attacher::AttachEngine3D
  Height = 12
  InnerRadius = 1.5
  OuterRadius = 4
  Placement = pos=(71,12,18.5) rot=(0.57735,0.57735,-0.57735;2.0944rad)
FEATURE [Part::MultiFuse] Fusion039  label="Bottom002"
  Refine = true
  Shapes = -> [Tube003,Cut041]
FEATURE [App::Part] Part015  label="GeigerBottom001"
  Group = -> [Cut039,Sketch028,Fusion037,Fusion038,Cut038,Extrude024,Tube003,Sketch024,Box056,Box058,Cylinder052,Cylinder053,Extrude027,Cut040,Cut041,Box059,Fusion039]
  Origin = -> Origin043
  Placement = pos=(0,0,0) rot=(-0.57735,-0.57735,-0.57735;2.0944rad)
FEATURE [App::Part] USB_TYPE_C_PORT__1_  label="USB TYPE C PORT (1)"
  Group = -> [Part__Feature370,Part__Feature371,Part__Feature372,Part__Feature373,Part__Feature365,Part__Feature366,Part__Feature367,Part__Feature368,Part__Feature374,Part__Feature375,Part__Feature376,Part__Feature377,Part__Feature378,Part__Feature379,Part__Feature380,Part__Feature381,Part__Feature382,Part__Feature383,Part__Feature384,Part__Feature385,Part__Feature386,Part__Feature387,Part__Feature388,+1 more]
  Origin = -> Origin046
  Placement = pos=(-3.0192,1.09628,5.395) rot=(0,0,1;0rad)
FEATURE [App::Part] USB_TYPE_C_PORT  label="USB TYPE C PORT"
  Group = -> [USB_TYPE_C_PORT__1_]
  Origin = -> Origin047
  Placement = pos=(4.31609,13.395,-12.1571) rot=(0.57735,0.57735,-0.57735;2.0944rad)
FEATURE [App::Part] Seeed_Studio_XIAO_ESP32_S3__Sense_  label="Seeed Studio XIAO-ESP32-S3 (Sense)"
  Group = -> [USB_TYPE_C_PORT,Part__Feature390,SKTAAAE010_v1,SKTAAAE010_v002,Part__Feature401,Part__Feature402]
  Origin = -> Origin011
FEATURE [App::Part] XIAO_ESP32S3_v2  label="XIAO-ESP32S3 v2"
  Group = -> [Seeed_Studio_XIAO_ESP32_S3__Sense_]
  Origin = -> Origin012
  Placement = pos=(2.2,14,57) rot=(-0.57735,-0.57735,0.57735;4.18879rad)
FEATURE [App::Part] _x_Male_Pin_2_54_mm  label="7x_Male_Pin_2.54_mm"
  Group = -> [Part__Feature403,Part__Feature404,Part__Feature405,Part__Feature406,Part__Feature407,Part__Feature408,Part__Feature409]
  Origin = -> Origin013
  Placement = pos=(-2.05,23.87,51.85) rot=(-0.57735,-0.57735,0.57735;4.18879rad)
FEATURE [App::Part] _x_Male_Pin_2_54_mm001  label="7x_Male_Pin_2.54_mm001"
  Group = -> [Part__Feature049,Part__Feature050,Part__Feature051,Part__Feature052,Part__Feature053,Part__Feature054,Part__Feature055]
  Origin = -> Origin014
  Placement = pos=(-2.05,39.12,51.85) rot=(-0.57735,-0.57735,0.57735;4.18879rad)
FEATURE [Part::MultiFuse] Fusion036  label="ESP"
  Placement = pos=(-1.4,0,0) rot=(0,0,1;0rad)
  Refine = true
  Shapes = -> [XIAO_ESP32S3_v2,_x_Male_Pin_2_54_mm,_x_Male_Pin_2_54_mm001]
FEATURE [App::Part] Part016  label="ESP001"
  Group = -> [XIAO_ESP32S3_v2,_x_Male_Pin_2_54_mm,_x_Male_Pin_2_54_mm001,Fusion036,Part__Feature058]
  Origin = -> Origin050
FEATURE [App::Part] pins  label="pins003"
  Group = -> [Part__Feature361,Part__Feature362,Part__Feature363]
  Origin = -> Origin003
FEATURE [App::Part] __pin_RMC_v0  label="3 pin RMC v0"
  Group = -> [pins,Part__Feature364]
  Origin = -> Origin045
  Placement = pos=(-3,12.25,7) rot=(0,0,1;4.71239rad)
FEATURE [App::Part] Part002  label="Radiation"
  Group = -> [Part__Feature369,Cylinder044,Cylinder045,Fusion034,Cylinder049,Cylinder050,Cylinder048,Cylinder051,Box051,Cut037,Sphere001,Sphere002,Cylinder043,Fusion031,Fusion030,Fusion033,Fusion032,Cylinder047,Cylinder046,Sphere003,Sphere,Box053,Box052,Box055,Box054,Fusion035,Fillet030,__pin_RMC_v0]
  Origin = -> Origin044
  Placement = pos=(-5.5,0,0) rot=(0,0,1;0rad)
FEATURE [Part::Compound] Compound006  label="Geiger+ESP"
  Links = -> [Part014,Part015,Part002,Part003,Part016]
  Placement = pos=(-155,3.52e-14,160) rot=(1,0,0;4.71239rad)
FEATURE [Part::Box] Box060  label="Cube035"
  AttacherType = Attacher::AttachEngine3D
  Height = 49
  Length = 38
  Placement = pos=(-0.34,0,0) rot=(0,0,1;0rad)
  Width = 17
FEATURE [Part::Box] Box061  label="Cube036"
  AttacherType = Attacher::AttachEngine3D
  Height = 59
  Length = 47.5
  Placement = pos=(-5,0,-5) rot=(0,0,1;0rad)
  Width = 22
FEATURE [Part::Box] Box009  label="stand1"
  AttacherType = Attacher::AttachEngine3D
  Height = 60
  Length = 15
  Placement = pos=(11.5,9,54) rot=(0,0,1;0rad)
  Width = 13
FEATURE [Part::Box] Box011  label="base001"
  AttacherType = Attacher::AttachEngine3D
  Height = 10
  Length = 115
  Placement = pos=(11.5,9,114) rot=(0,0,1;0rad)
  Width = 13
FEATURE [Part::Box] Box012  label="stand002"
  AttacherType = Attacher::AttachEngine3D
  Height = 60
  Length = 15
  Placement = pos=(111.5,9,54) rot=(0,0,1;0rad)
  Width = 13
FEATURE [Part::Box] Box062  label="Cube006"
  AttacherType = Attacher::AttachEngine3D
  Height = 49
  Length = 38
  Placement = pos=(-0.34,0,0) rot=(0,0,1;0rad)
  Width = 17
FEATURE [Part::Box] Box063  label="Cube007"
  AttacherType = Attacher::AttachEngine3D
  Height = 59
  Length = 47.5
  Placement = pos=(-5,0,-5) rot=(0,0,1;0rad)
  Width = 22
FEATURE [Part::Cut] Cut043  label="Hollow_CubeBase"
  Base = -> Box061
  Refine = true
  Tool = -> Box060
FEATURE [Part::Cut] Cut044  label="Hollow_CubeBase001"
  Base = -> Box063
  Placement = pos=(100,0,0) rot=(0,0,1;0rad)
  Refine = true
  Tool = -> Box062
FEATURE [Part::Cylinder] Cylinder055  label="m3_1"
  Angle = 360
  AttacherType = Attacher::AttachEngine3D
  FirstAngle = 0
  Height = 20
  Placement = pos=(57.5,15,109) rot=(0,0,1;0rad)
  Radius = 1.6
  SecondAngle = 0
FEATURE [Part::Cylinder] Cylinder056  label="m3_2"
  Angle = 360
  AttacherType = Attacher::AttachEngine3D
  FirstAngle = 0
  Height = 20
  Placement = pos=(80,15,109) rot=(0,0,1;0rad)
  Radius = 1.6
  SecondAngle = 0
FEATURE [Part::Cylinder] Cylinder057  label="m3_3"
  Angle = 360
  AttacherType = Attacher::AttachEngine3D
  FirstAngle = 0
  Height = 20
  Placement = pos=(57.5,32,109) rot=(0,0,1;0rad)
  Radius = 1.6
  SecondAngle = 0
FEATURE [Part::Cylinder] Cylinder058  label="m3_4"
  Angle = 360
  AttacherType = Attacher::AttachEngine3D
  FirstAngle = 0
  Height = 20
  Placement = pos=(80,32,109) rot=(0,0,1;0rad)
  Radius = 1.6
  SecondAngle = 0
FEATURE [Part::MultiFuse] Fusion042  label="m3_cyl"
  Refine = true
  Shapes = -> [Cylinder055,Cylinder056,Cylinder057,Cylinder058]
FEATURE [Part::MultiFuse] Fusion005  label="baseFusion"
  Refine = true
  Shapes = -> [Box009,Box011,Box012]
FEATURE [Part::MultiFuse] Fusion041  label="gpsHolder"
  Shapes = -> [Fusion005,Cut043,Cut044]
FEATURE [Part::Cut] Cut045  label="gpsHolder001"
  Base = -> Fusion041
  Tool = -> Fusion042
FEATURE [Sketcher::SketchObject] Sketch029
  ArcFitTolerance = 1e-06
  FullyConstrained = true
  MakeInternals = false
  MapMode = 5
  Placement = pos=(0,-48,0) rot=(1,0,0;1.5708rad)
  sketch-geometry (8):
    g0: LineSegment StartX=16.5 StartY=9 StartZ=0 EndX=16.5 EndY=-1 EndZ=0
    g1: LineSegment StartX=16.5 StartY=-1 StartZ=0 EndX=21.5 EndY=-1 EndZ=0
    g2: LineSegment StartX=21.5 StartY=-1 StartZ=0 EndX=21.5 EndY=9 EndZ=0
    g3: LineSegment StartX=21.5 StartY=9 StartZ=0 EndX=16.5 EndY=9 EndZ=0
    g4: LineSegment StartX=116.5 StartY=9 StartZ=0 EndX=116.5 EndY=0 EndZ=0
    g5: LineSegment StartX=116.5 StartY=0 StartZ=0 EndX=121.5 EndY=0 EndZ=0
    g6: LineSegment StartX=121.5 StartY=0 StartZ=0 EndX=121.5 EndY=9 EndZ=0
    g7: LineSegment StartX=121.5 StartY=9 StartZ=0 EndX=116.5 EndY=9 EndZ=0
  constraints (25):
    c: Coincident(g0,g1)
    c: Coincident(g1,g2)
    c: Coincident(g2,g3)
    c: Coincident(g3,g0)
    c: Vertical(g0)
    c: Vertical(g2)
    c: Horizontal(g1)
    c: Horizontal(g3)
    c: PointOnObject(g1,g-1)
    c: Coincident(g4,g5)
    c: Coincident(g5,g6)
    c: Coincident(g6,g7)
    c: Coincident(g7,g4)
    c: Vertical(g4)
    c: Vertical(g6)
    c: Horizontal(g5)
    c: Horizontal(g7)
    c: PointOnObject(g5,g-1)
    c: DistanceY(g0,g0) = 10
    c: DistanceX(g0) = 16.5
    c: DistanceX(g0,g1) = 5
    c: Horizontal(g4,g2)
    c: DistanceX(g4,g5) = 5
    c: DistanceX(g4) = 116.5
    c: DistanceY(g0) = 9
FEATURE [Part::Extrusion] Extrude028
  Base = -> Sketch029
  Dir = (0,-1,2e-16)
  DirMode = 2
  FaceMakerClass = Part::FaceMakerBullseye
  FaceMakerMode = 3
  LengthFwd = 10
  LengthRev = 0
  Placement = pos=(0,57,45) rot=(0,0,1;0rad)
  Solid = true
  Symmetric = false
FEATURE [Part::Cut] Cut046  label="gpsHolder004"
  Base = -> Cut045
  Tool = -> Extrude028
FEATURE [Part::Fillet] Fillet031
  Base = -> Cut046
  EdgeLinks = -> Cut046 [Edge1,Edge4,Edge9,Edge26,Edge34,Edge44,Edge45,Edge46,Edge47,Edge52,Edge56,Edge61,Edge74,Edge75,Edge76,Edge77,Edge81,Edge83,Edge93,Edge95,Edge98,Edge99,Edge103,Edge104]
  Edges = 24 edges r=4: [Edge1,Edge4,Edge9,Edge26,Edge34,Edge44,Edge45,Edge46,Edge47,Edge52,Edge56,Edge61,Edge74,Edge75,Edge76,Edge77,Edge81,Edge83,Edge93,Edge95,Edge98,Edge99,Edge103,Edge104]
FEATURE [Part::Fillet] Fillet032
  Base = -> Fillet031
  EdgeLinks = -> Fillet031 [Edge142,Edge157,Edge162,Edge164,Edge166,Edge167,Edge170,Edge172,Edge173,Edge175,Edge177,Edge179,Edge180,Edge183,Edge185,Edge186]
  Edges = 16 edges r=2: [Edge142,Edge157,Edge162,Edge164,Edge166,Edge167,Edge170,Edge172,Edge173,Edge175,Edge177,Edge179,Edge180,Edge183,Edge185,Edge186]
FEATURE [Part::Fillet] Fillet033  label="gpsHolder005"
  Base = -> Fillet032
  EdgeLinks = -> Fillet032 [Edge52,Edge54,Edge56,Edge57,Edge59,Edge64,Edge66,Edge68,Edge69,Edge103,Edge104,Edge105,Edge124,Edge135,Edge149,Edge150,Edge151,Edge154,Edge155,Edge156,Edge157,Edge158,Edge159,Edge160]
  Edges = 24 edges r=3: [Edge52,Edge54,Edge56,Edge57,Edge59,Edge64,Edge66,Edge68,Edge69,Edge103,Edge104,Edge105,Edge124,Edge135,Edge149,Edge150,Edge151,Edge154,Edge155,Edge156,Edge157,Edge158,Edge159,Edge160]
  Placement = pos=(-68.75,4.52e-14,205) rot=(1,0,0;4.71239rad)
FEATURE [Part::Box] Box064  label="Cube037"
  AttacherType = Attacher::AttachEngine3D
  Height = 21
  Length = 24
  Placement = pos=(13.5,16,0) rot=(0,0,1;0rad)
  Width = 4.5
FEATURE [Part::Box] Box065  label="Cube038"
  AttacherType = Attacher::AttachEngine3D
  Height = 21
  Length = 24
  Placement = pos=(13.5,27.5,0) rot=(0,0,1;0rad)
  Width = 4.5
FEATURE [Part::Box] Box066  label="Cube039"
  AttacherType = Attacher::AttachEngine3D
  Height = 21
  Length = 24
  Placement = pos=(13.5,39,0) rot=(0,0,1;0rad)
  Width = 4.5
FEATURE [Part::Box] Box067  label="Cube040"
  AttacherType = Attacher::AttachEngine3D
  Height = 21
  Length = 24
  Placement = pos=(13.5,50.5,0) rot=(0,0,1;0rad)
  Width = 4.5
FEATURE [Part::Box] Box068  label="Cube041"
  AttacherType = Attacher::AttachEngine3D
  Height = 15
  Length = 9
  Placement = pos=(2.5,13,0) rot=(0,0,1;0rad)
  Width = 10
FEATURE [Part::Box] Box069  label="Cube042"
  AttacherType = Attacher::AttachEngine3D
  Height = 15
  Length = 9
  Placement = pos=(2.5,24,0) rot=(0,0,1;0rad)
  Width = 10
FEATURE [Part::Box] Box070  label="Cube043"
  AttacherType = Attacher::AttachEngine3D
  Height = 15
  Length = 9
  Placement = pos=(2.5,35,0) rot=(0,0,1;0rad)
  Width = 10
FEATURE [Part::Box] Box071  label="Cube044"
  AttacherType = Attacher::AttachEngine3D
  Height = 15
  Length = 9
  Placement = pos=(2.5,46,0) rot=(0,0,1;0rad)
  Width = 10
FEATURE [Part::Box] Box008  label="Cube008"
  AttacherType = Attacher::AttachEngine3D
  Height = 51
  Length = 73
  Placement = pos=(-25,-23,-45) rot=(0,0,1;0rad)
  Width = 5
FEATURE [Part::Box] Box072  label="Cube045"
  AttacherType = Attacher::AttachEngine3D
  Height = 5
  Length = 10
  Placement = pos=(-35,-25.5,-45) rot=(0,0,1;0rad)
  Width = 10
FEATURE [Part::Box] Box073  label="Cube046"
  AttacherType = Attacher::AttachEngine3D
  Height = 5
  Length = 10
  Placement = pos=(48,-25.5,-45) rot=(0,0,1;0rad)
  Width = 10
FEATURE [Part::Cylinder] Cylinder059
  Angle = 360
  AttacherType = Attacher::AttachEngine3D
  FirstAngle = 0
  Height = 10
  Placement = pos=(53,-13.5,-53) rot=(0,0,1;0rad)
  Radius = 1.6
  SecondAngle = 0
FEATURE [Part::Cylinder] Cylinder060
  Angle = 360
  AttacherType = Attacher::AttachEngine3D
  FirstAngle = 0
  Height = 10
  Placement = pos=(-30,-13.5,-53) rot=(0,0,1;0rad)
  Radius = 1.6
  SecondAngle = 0
FEATURE [Part::Cylinder] Cylinder061
  Angle = 90
  AttacherType = Attacher::AttachEngine3D
  FirstAngle = 0
  Height = 5
  Placement = pos=(-25,-11,-51) rot=(0,0,1;0rad)
  Radius = 2.5
  SecondAngle = 0
FEATURE [Part::Cylinder] Cylinder062
  Angle = 90
  AttacherType = Attacher::AttachEngine3D
  FirstAngle = 0
  Height = 5
  Placement = pos=(-25,-16,-51) rot=(0,0,1;4.71239rad)
  Radius = 2.5
  SecondAngle = 0
FEATURE [Part::Cylinder] Cylinder063
  Angle = 90
  AttacherType = Attacher::AttachEngine3D
  FirstAngle = 0
  Height = 5
  Placement = pos=(48,-11,-51) rot=(0,0,1;1.5708rad)
  Radius = 2.5
  SecondAngle = 0
FEATURE [Part::Cylinder] Cylinder064
  Angle = 90
  AttacherType = Attacher::AttachEngine3D
  FirstAngle = 0
  Height = 5
  Placement = pos=(48,-16,-51) rot=(0,0,-1;3.14159rad)
  Radius = 2.5
  SecondAngle = 0
FEATURE [Part::Cylinder] Cylinder065
  Angle = 360
  AttacherType = Attacher::AttachEngine3D
  FirstAngle = 0
  Height = 10
  Placement = pos=(33,-17.5,-6) rot=(1,0,0;4.71239rad)
  Radius = 1
  SecondAngle = 0
FEATURE [Part::MultiFuse] Fusion043  label="relay'"
  Shapes = -> [Box064,Box065,Box066,Box067]
FEATURE [Part::MultiFuse] Fusion044  label="inputs"
  Shapes = -> [Box068,Box069,Box070,Box071]
FEATURE [Part::MultiFuse] Fusion049  label="m3Cyl001"
  Refine = true
  Shapes = -> [Cylinder059,Cylinder060]
FEATURE [Part::MultiFuse] Fusion050  label="Base_support"
  Refine = true
  Shapes = -> [Cylinder061,Cylinder062,Cylinder063,Cylinder064]
FEATURE [App::Part] Part  label="nano_hold"
  Origin = -> Origin088
FEATURE [Part::Feature] Part__Feature410  label="Board (1)"
  shape: bbox 43.18 x 17.78 x 0.805 mm, 251 faces (baked)
FEATURE [Part::Feature] Part__Feature411  label="LSM9DS1TR_LGA-24_3X3P5X1_STM v1"
  Placement = pos=(21.5608,12.1142,0.754) rot=(0,0,1;0rad)
  shape: bbox 0.15 x 0.15 x 0.003 mm, 3 faces (baked)
FEATURE [Part::Feature] Part__Feature412  label="LSM9DS1TR_LGA-24_3X3P5X1_STM v002"
  Placement = pos=(21.5608,12.1142,0.754) rot=(0,0,1;0rad)
  shape: bbox 3.5 x 3 x 1.346 mm, 6 faces (baked)
FEATURE [Part::Feature] Part__Feature413  label="LSM9DS1TR_LGA-24_3X3P5X1_STM v003"
  Placement = pos=(21.5608,12.1142,0.754) rot=(0,0,1;0rad)
  shape: bbox 0.4 x 0.28 x 0.051 mm, 6 faces (baked)
FEATURE [Part::Feature] Part__Feature414  label="LSM9DS1TR_LGA-24_3X3P5X1_STM v004"
  Placement = pos=(21.5608,12.1142,0.754) rot=(0,0,1;0rad)
  shape: bbox 0.4 x 0.28 x 0.051 mm, 6 faces (baked)
FEATURE [Part::Feature] Part__Feature415  label="LSM9DS1TR_LGA-24_3X3P5X1_STM v005"
  Placement = pos=(21.5608,12.1142,0.754) rot=(0,0,1;0rad)
  shape: bbox 0.4 x 0.28 x 0.051 mm, 6 faces (baked)
FEATURE [Part::Feature] Part__Feature416  label="LSM9DS1TR_LGA-24_3X3P5X1_STM v006"
  Placement = pos=(21.5608,12.1142,0.754) rot=(0,0,1;0rad)
  shape: bbox 0.4 x 0.28 x 0.051 mm, 6 faces (baked)
FEATURE [Part::Feature] Part__Feature417  label="LSM9DS1TR_LGA-24_3X3P5X1_STM v007"
  Placement = pos=(21.5608,12.1142,0.754) rot=(0,0,1;0rad)
  shape: bbox 0.28 x 0.4 x 0.051 mm, 6 faces (baked)
FEATURE [Part::Feature] Part__Feature418  label="LSM9DS1TR_LGA-24_3X3P5X1_STM v008"
  Placement = pos=(21.5608,12.1142,0.754) rot=(0,0,1;0rad)
  shape: bbox 0.28 x 0.4 x 0.051 mm, 6 faces (baked)
FEATURE [Part::Feature] Part__Feature419  label="LSM9DS1TR_LGA-24_3X3P5X1_STM v009"
  Placement = pos=(21.5608,12.1142,0.754) rot=(0,0,1;0rad)
  shape: bbox 0.28 x 0.4 x 0.051 mm, 6 faces (baked)
FEATURE [Part::Feature] Part__Feature420  label="LSM9DS1TR_LGA-24_3X3P5X1_STM v010"
  Placement = pos=(21.5608,12.1142,0.754) rot=(0,0,1;0rad)
  shape: bbox 0.28 x 0.4 x 0.051 mm, 6 faces (baked)
FEATURE [Part::Feature] Part__Feature421  label="LSM9DS1TR_LGA-24_3X3P5X1_STM v011"
  Placement = pos=(21.5608,12.1142,0.754) rot=(0,0,1;0rad)
  shape: bbox 0.28 x 0.4 x 0.051 mm, 6 faces (baked)
FEATURE [Part::Feature] Part__Feature422  label="LSM9DS1TR_LGA-24_3X3P5X1_STM v012"
  Placement = pos=(21.5608,12.1142,0.754) rot=(0,0,1;0rad)
  shape: bbox 0.28 x 0.4 x 0.051 mm, 6 faces (baked)
FEATURE [Part::Feature] Part__Feature423  label="LSM9DS1TR_LGA-24_3X3P5X1_STM v013"
  Placement = pos=(21.5608,12.1142,0.754) rot=(0,0,1;0rad)
  shape: bbox 0.28 x 0.4 x 0.051 mm, 6 faces (baked)
FEATURE [Part::Feature] Part__Feature424  label="LSM9DS1TR_LGA-24_3X3P5X1_STM v014"
  Placement = pos=(21.5608,12.1142,0.754) rot=(0,0,1;0rad)
  shape: bbox 0.28 x 0.4 x 0.051 mm, 6 faces (baked)
FEATURE [Part::Feature] Part__Feature425  label="LSM9DS1TR_LGA-24_3X3P5X1_STM v015"
  Placement = pos=(21.5608,12.1142,0.754) rot=(0,0,1;0rad)
  shape: bbox 0.4 x 0.28 x 0.051 mm, 6 faces (baked)
FEATURE [Part::Feature] Part__Feature426  label="LSM9DS1TR_LGA-24_3X3P5X1_STM v016"
  Placement = pos=(21.5608,12.1142,0.754) rot=(0,0,1;0rad)
  shape: bbox 0.4 x 0.28 x 0.051 mm, 6 faces (baked)
FEATURE [Part::Feature] Part__Feature427  label="LSM9DS1TR_LGA-24_3X3P5X1_STM v017"
  Placement = pos=(21.5608,12.1142,0.754) rot=(0,0,1;0rad)
  shape: bbox 0.4 x 0.28 x 0.051 mm, 6 faces (baked)
FEATURE [Part::Feature] Part__Feature428  label="LSM9DS1TR_LGA-24_3X3P5X1_STM v018"
  Placement = pos=(21.5608,12.1142,0.754) rot=(0,0,1;0rad)
  shape: bbox 0.4 x 0.28 x 0.051 mm, 6 faces (baked)
FEATURE [Part::Feature] Part__Feature429  label="LSM9DS1TR_LGA-24_3X3P5X1_STM v019"
  Placement = pos=(21.5608,12.1142,0.754) rot=(0,0,1;0rad)
  shape: bbox 0.28 x 0.4 x 0.051 mm, 6 faces (baked)
FEATURE [Part::Feature] Part__Feature430  label="LSM9DS1TR_LGA-24_3X3P5X1_STM v020"
  Placement = pos=(21.5608,12.1142,0.754) rot=(0,0,1;0rad)
  shape: bbox 0.28 x 0.4 x 0.051 mm, 6 faces (baked)
FEATURE [Part::Feature] Part__Feature431  label="LSM9DS1TR_LGA-24_3X3P5X1_STM v021"
  Placement = pos=(21.5608,12.1142,0.754) rot=(0,0,1;0rad)
  shape: bbox 0.28 x 0.4 x 0.051 mm, 6 faces (baked)
FEATURE [Part::Feature] Part__Feature432  label="LSM9DS1TR_LGA-24_3X3P5X1_STM v022"
  Placement = pos=(21.5608,12.1142,0.754) rot=(0,0,1;0rad)
  shape: bbox 0.28 x 0.4 x 0.051 mm, 6 faces (baked)
FEATURE [Part::Feature] Part__Feature433  label="LSM9DS1TR_LGA-24_3X3P5X1_STM v023"
  Placement = pos=(21.5608,12.1142,0.754) rot=(0,0,1;0rad)
  shape: bbox 0.28 x 0.4 x 0.051 mm, 6 faces (baked)
FEATURE [Part::Feature] Part__Feature434  label="LSM9DS1TR_LGA-24_3X3P5X1_STM v024"
  Placement = pos=(21.5608,12.1142,0.754) rot=(0,0,1;0rad)
  shape: bbox 0.28 x 0.4 x 0.051 mm, 6 faces (baked)
FEATURE [Part::Feature] Part__Feature435  label="LSM9DS1TR_LGA-24_3X3P5X1_STM v025"
  Placement = pos=(21.5608,12.1142,0.754) rot=(0,0,1;0rad)
  shape: bbox 0.28 x 0.4 x 0.051 mm, 6 faces (baked)
FEATURE [Part::Feature] Part__Feature436  label="LSM9DS1TR_LGA-24_3X3P5X1_STM v026"
  Placement = pos=(21.5608,12.1142,0.754) rot=(0,0,1;0rad)
  shape: bbox 0.28 x 0.4 x 0.051 mm, 6 faces (baked)
FEATURE [App::Part] LSM9DS1TR_LGA_24_3X3P5X1_STM_v1  label="LSM9DS1TR_LGA-24_3X3P5X1_STM v027"
  Group = -> [Part__Feature411,Part__Feature412,Part__Feature413,Part__Feature414,Part__Feature415,Part__Feature416,Part__Feature417,Part__Feature418,Part__Feature419,Part__Feature420,Part__Feature421,Part__Feature422,Part__Feature423,Part__Feature424,Part__Feature425,Part__Feature426,Part__Feature427,Part__Feature428,Part__Feature429,Part__Feature430,Part__Feature431,Part__Feature432,Part__Feature433,+3 more]
  Origin = -> Origin051
FEATURE [Part::Feature] Part__Feature437  label="ZX62-AB-5PA (1)"
  Placement = pos=(-4.98,1.125,5.465) rot=(0,0,1;0rad)
  shape: bbox 5.614 x 2.964 x 8.831 mm, 424 faces (baked)
FEATURE [Part::Feature] Part__Feature438  label="IoT_HSMG-C190 LED v1"
  Placement = pos=(1.9,3.1,0.805) rot=(1,0,0;1.5708rad)
  shape: bbox 1.6 x 0.8 x 0.8 mm, 18 faces (baked)
FEATURE [Part::Feature] Part__Feature439  label="IoT_MPM3610 Step-Down Module v1"
  Placement = pos=(15.675,5.1865,1.605) rot=(0,0.707107,0.707107;3.14159rad)
  shape: bbox 3.3 x 5.15 x 1.65 mm, 330 faces (baked)
FEATURE [Part::Feature] Part__Feature440  label="User Library-arduino_nano_reset core"
  Placement = pos=(-8.89,0.805,-11.09) rot=(0,0,1;0rad)
  shape: bbox 5.251 x 2.159 x 2.809 mm, 76 faces (baked)
FEATURE [Part::Feature] Part__Feature441  label="User Library-arduino_nano_reset shell"
  Placement = pos=(-8.89,2.455,-11.09) rot=(0,-1,0;1.5708rad)
  shape: bbox 4 x 1.65 x 3 mm, 71 faces (baked)
FEATURE [App::Part] IoT_Reser_Button_v1  label="IoT_Reser Button v1"
  Group = -> [Part__Feature440,Part__Feature441]
  Origin = -> Origin053
  Placement = pos=(0,0,0) rot=(0.57735,-0.57735,-0.57735;2.0944rad)
FEATURE [Part::Feature] Part__Feature442  label="RC0402FR-071KL RC0402N_YAG v1"
  Placement = pos=(4.8,3.0875,0.805) rot=(0,0,1;0rad)
  shape: bbox 0.458 x 0.494 x 0.697 mm, 6 faces (baked)
FEATURE [Part::Feature] Part__Feature443  label="RC0402FR-071KL RC0402N_YAG v002"
  Placement = pos=(4.8,3.0875,0.805) rot=(0,0,1;0rad)
  shape: bbox 0.304 x 0.508 x 0.711 mm, 6 faces (baked)
FEATURE [Part::Feature] Part__Feature444  label="RC0402FR-071KL RC0402N_YAG v003"
  Placement = pos=(4.8,3.0875,0.805) rot=(0,0,1;0rad)
  shape: bbox 0.304 x 0.508 x 0.711 mm, 6 faces (baked)
FEATURE [Part::Feature] Part__Feature445  label="RC0402FR-071KL RC0402N_YAG v005"
  Placement = pos=(6.25,4.4075,0.805) rot=(0,0,-1;1.5708rad)
  shape: bbox 0.494 x 0.458 x 0.697 mm, 6 faces (baked)
FEATURE [Part::Feature] Part__Feature446  label="RC0402FR-071KL RC0402N_YAG v006"
  Placement = pos=(6.25,4.4075,0.805) rot=(0,0,-1;1.5708rad)
  shape: bbox 0.508 x 0.304 x 0.711 mm, 6 faces (baked)
FEATURE [Part::Feature] Part__Feature447  label="RC0402FR-071KL RC0402N_YAG v007"
  Placement = pos=(6.25,4.4075,0.805) rot=(0,0,-1;1.5708rad)
  shape: bbox 0.508 x 0.304 x 0.711 mm, 6 faces (baked)
FEATURE [Part::Feature] Part__Feature448  label="RC0402FR-071KL RC0402N_YAG v009"
  Placement = pos=(9.8875,5.5375,0.805) rot=(0,0,1;0rad)
  shape: bbox 0.458 x 0.494 x 0.697 mm, 6 faces (baked)
FEATURE [Part::Feature] Part__Feature449  label="RC0402FR-071KL RC0402N_YAG v010"
  Placement = pos=(9.8875,5.5375,0.805) rot=(0,0,1;0rad)
  shape: bbox 0.304 x 0.508 x 0.711 mm, 6 faces (baked)
FEATURE [Part::Feature] Part__Feature450  label="RC0402FR-071KL RC0402N_YAG v011"
  Placement = pos=(9.8875,5.5375,0.805) rot=(0,0,1;0rad)
  shape: bbox 0.304 x 0.508 x 0.711 mm, 6 faces (baked)
FEATURE [Part::Feature] Part__Feature451  label="RC0402FR-071KL RC0402N_YAG v013"
  Placement = pos=(11.27,12.5,0.805) rot=(0,0,1;0rad)
  shape: bbox 0.458 x 0.494 x 0.697 mm, 6 faces (baked)
FEATURE [Part::Feature] Part__Feature452  label="RC0402FR-071KL RC0402N_YAG v014"
  Placement = pos=(11.27,12.5,0.805) rot=(0,0,1;0rad)
  shape: bbox 0.304 x 0.508 x 0.711 mm, 6 faces (baked)
FEATURE [Part::Feature] Part__Feature453  label="RC0402FR-071KL RC0402N_YAG v015"
  Placement = pos=(11.27,12.5,0.805) rot=(0,0,1;0rad)
  shape: bbox 0.304 x 0.508 x 0.711 mm, 6 faces (baked)
FEATURE [Part::Feature] Part__Feature454  label="RC0402FR-071KL RC0402N_YAG v017"
  Placement = pos=(5.4,14.7,0.805) rot=(0,0,1;0rad)
  shape: bbox 0.458 x 0.494 x 0.697 mm, 6 faces (baked)
FEATURE [Part::Feature] Part__Feature455  label="RC0402FR-071KL RC0402N_YAG v018"
  Placement = pos=(5.4,14.7,0.805) rot=(0,0,1;0rad)
  shape: bbox 0.304 x 0.508 x 0.711 mm, 6 faces (baked)
FEATURE [Part::Feature] Part__Feature456  label="RC0402FR-071KL RC0402N_YAG v019"
  Placement = pos=(5.4,14.7,0.805) rot=(0,0,1;0rad)
  shape: bbox 0.304 x 0.508 x 0.711 mm, 6 faces (baked)
FEATURE [Part::Feature] Part__Feature457  label="RC0402FR-071KL RC0402N_YAG v021"
  Placement = pos=(12.225,4.225,0.805) rot=(0,0,1;1.5708rad)
  shape: bbox 0.494 x 0.458 x 0.697 mm, 6 faces (baked)
FEATURE [Part::Feature] Part__Feature458  label="RC0402FR-071KL RC0402N_YAG v022"
  Placement = pos=(12.225,4.225,0.805) rot=(0,0,1;1.5708rad)
  shape: bbox 0.508 x 0.304 x 0.711 mm, 6 faces (baked)
FEATURE [Part::Feature] Part__Feature459  label="RC0402FR-071KL RC0402N_YAG v023"
  Placement = pos=(12.225,4.225,0.805) rot=(0,0,1;1.5708rad)
  shape: bbox 0.508 x 0.304 x 0.711 mm, 6 faces (baked)
FEATURE [Part::Feature] Part__Feature460  label="RC0402FR-071KL RC0402N_YAG v025"
  Placement = pos=(13.1875,4.2375,0.805) rot=(0,0,1;1.5708rad)
  shape: bbox 0.494 x 0.458 x 0.697 mm, 6 faces (baked)
FEATURE [Part::Feature] Part__Feature461  label="RC0402FR-071KL RC0402N_YAG v026"
  Placement = pos=(13.1875,4.2375,0.805) rot=(0,0,1;1.5708rad)
  shape: bbox 0.508 x 0.304 x 0.711 mm, 6 faces (baked)
FEATURE [Part::Feature] Part__Feature462  label="RC0402FR-071KL RC0402N_YAG v027"
  Placement = pos=(13.1875,4.2375,0.805) rot=(0,0,1;1.5708rad)
  shape: bbox 0.508 x 0.304 x 0.711 mm, 6 faces (baked)
FEATURE [Part::Feature] Part__Feature463  label="RC0402FR-071KL RC0402N_YAG v029"
  Placement = pos=(13.85,10.9,0.805) rot=(0,0,-1;1.5708rad)
  shape: bbox 0.494 x 0.458 x 0.697 mm, 6 faces (baked)
FEATURE [Part::Feature] Part__Feature464  label="RC0402FR-071KL RC0402N_YAG v030"
  Placement = pos=(13.85,10.9,0.805) rot=(0,0,-1;1.5708rad)
  shape: bbox 0.508 x 0.304 x 0.711 mm, 6 faces (baked)
FEATURE [Part::Feature] Part__Feature465  label="RC0402FR-071KL RC0402N_YAG v031"
  Placement = pos=(13.85,10.9,0.805) rot=(0,0,-1;1.5708rad)
  shape: bbox 0.508 x 0.304 x 0.711 mm, 6 faces (baked)
FEATURE [Part::Feature] Part__Feature056  label="RC0402FR-071KL RC0402N_YAG v033"
  Placement = pos=(14.8,10.9,0.805) rot=(0,0,-1;1.5708rad)
  shape: bbox 0.494 x 0.458 x 0.697 mm, 6 faces (baked)
FEATURE [Part::Feature] Part__Feature057  label="RC0402FR-071KL RC0402N_YAG v034"
  Placement = pos=(14.8,10.9,0.805) rot=(0,0,-1;1.5708rad)
  shape: bbox 0.508 x 0.304 x 0.711 mm, 6 faces (baked)
FEATURE [Part::Feature] Part__Feature466  label="RC0402FR-071KL RC0402N_YAG v035"
  Placement = pos=(14.8,10.9,0.805) rot=(0,0,-1;1.5708rad)
  shape: bbox 0.508 x 0.304 x 0.711 mm, 6 faces (baked)
FEATURE [Part::Feature] Part__Feature059  label="RC0402FR-071KL RC0402N_YAG v037"
  Placement = pos=(15.55,9.275,0.805) rot=(0,0,1;0rad)
  shape: bbox 0.458 x 0.494 x 0.697 mm, 6 faces (baked)
FEATURE [Part::Feature] Part__Feature060  label="RC0402FR-071KL RC0402N_YAG v038"
  Placement = pos=(15.55,9.275,0.805) rot=(0,0,1;0rad)
  shape: bbox 0.304 x 0.508 x 0.711 mm, 6 faces (baked)
FEATURE [Part::Feature] Part__Feature061  label="RC0402FR-071KL RC0402N_YAG v039"
  Placement = pos=(15.55,9.275,0.805) rot=(0,0,1;0rad)
  shape: bbox 0.304 x 0.508 x 0.711 mm, 6 faces (baked)
FEATURE [Part::Feature] Part__Feature062  label="RC0402FR-071KL RC0402N_YAG v041"
  Placement = pos=(16.525,12.75,0.805) rot=(0,0,-1;1.5708rad)
  shape: bbox 0.494 x 0.458 x 0.697 mm, 6 faces (baked)
FEATURE [Part::Feature] Part__Feature063  label="RC0402FR-071KL RC0402N_YAG v042"
  Placement = pos=(16.525,12.75,0.805) rot=(0,0,-1;1.5708rad)
  shape: bbox 0.508 x 0.304 x 0.711 mm, 6 faces (baked)
FEATURE [Part::Feature] Part__Feature064  label="RC0402FR-071KL RC0402N_YAG v043"
  Placement = pos=(16.525,12.75,0.805) rot=(0,0,-1;1.5708rad)
  shape: bbox 0.508 x 0.304 x 0.711 mm, 6 faces (baked)
FEATURE [Part::Feature] Part__Feature065  label="RC0402FR-071KL RC0402N_YAG v045"
  Placement = pos=(18,13.675,0.805) rot=(0,0,1;0rad)
  shape: bbox 0.458 x 0.494 x 0.697 mm, 6 faces (baked)
FEATURE [Part::Feature] Part__Feature066  label="RC0402FR-071KL RC0402N_YAG v046"
  Placement = pos=(18,13.675,0.805) rot=(0,0,1;0rad)
  shape: bbox 0.304 x 0.508 x 0.711 mm, 6 faces (baked)
FEATURE [Part::Feature] Part__Feature067  label="RC0402FR-071KL RC0402N_YAG v047"
  Placement = pos=(18,13.675,0.805) rot=(0,0,1;0rad)
  shape: bbox 0.304 x 0.508 x 0.711 mm, 6 faces (baked)
FEATURE [Part::Feature] Part__Feature068  label="RC0402FR-071KL RC0402N_YAG v049"
  Placement = pos=(18.475,9.775,0.805) rot=(0,0,1;0rad)
  shape: bbox 0.458 x 0.494 x 0.697 mm, 6 faces (baked)
FEATURE [Part::Feature] Part__Feature069  label="RC0402FR-071KL RC0402N_YAG v050"
  Placement = pos=(18.475,9.775,0.805) rot=(0,0,1;0rad)
  shape: bbox 0.304 x 0.508 x 0.711 mm, 6 faces (baked)
FEATURE [Part::Feature] Part__Feature070  label="RC0402FR-071KL RC0402N_YAG v051"
  Placement = pos=(18.475,9.775,0.805) rot=(0,0,1;0rad)
  shape: bbox 0.304 x 0.508 x 0.711 mm, 6 faces (baked)
FEATURE [Part::Feature] Part__Feature071  label="RC0402FR-071KL RC0402N_YAG v053"
  Placement = pos=(18.45,8.6,0.805) rot=(0,0,1;0rad)
  shape: bbox 0.458 x 0.494 x 0.697 mm, 6 faces (baked)
FEATURE [Part::Feature] Part__Feature072  label="RC0402FR-071KL RC0402N_YAG v054"
  Placement = pos=(18.45,8.6,0.805) rot=(0,0,1;0rad)
  shape: bbox 0.304 x 0.508 x 0.711 mm, 6 faces (baked)
FEATURE [Part::Feature] Part__Feature073  label="RC0402FR-071KL RC0402N_YAG v055"
  Placement = pos=(18.45,8.6,0.805) rot=(0,0,1;0rad)
  shape: bbox 0.304 x 0.508 x 0.711 mm, 6 faces (baked)
FEATURE [Part::Feature] Part__Feature074  label="RC0402FR-071KL RC0402N_YAG v057"
  Placement = pos=(21,6.275,0.805) rot=(0,0,1;0rad)
  shape: bbox 0.458 x 0.494 x 0.697 mm, 6 faces (baked)
FEATURE [Part::Feature] Part__Feature075  label="RC0402FR-071KL RC0402N_YAG v058"
  Placement = pos=(21,6.275,0.805) rot=(0,0,1;0rad)
  shape: bbox 0.304 x 0.508 x 0.711 mm, 6 faces (baked)
FEATURE [Part::Feature] Part__Feature076  label="RC0402FR-071KL RC0402N_YAG v059"
  Placement = pos=(21,6.275,0.805) rot=(0,0,1;0rad)
  shape: bbox 0.304 x 0.508 x 0.711 mm, 6 faces (baked)
FEATURE [Part::Feature] Part__Feature077  label="RC0402FR-071KL RC0402N_YAG v061"
  Placement = pos=(21,5.275,0.805) rot=(0,0,1;0rad)
  shape: bbox 0.458 x 0.494 x 0.697 mm, 6 faces (baked)
FEATURE [Part::Feature] Part__Feature078  label="RC0402FR-071KL RC0402N_YAG v062"
  Placement = pos=(21,5.275,0.805) rot=(0,0,1;0rad)
  shape: bbox 0.304 x 0.508 x 0.711 mm, 6 faces (baked)
FEATURE [Part::Feature] Part__Feature079  label="RC0402FR-071KL RC0402N_YAG v063"
  Placement = pos=(21,5.275,0.805) rot=(0,0,1;0rad)
  shape: bbox 0.304 x 0.508 x 0.711 mm, 6 faces (baked)
FEATURE [Part::Feature] Part__Feature080  label="RC0402FR-071KL RC0402N_YAG v065"
  Placement = pos=(20.405,3.8,0.805) rot=(0,0,-1;1.5708rad)
  shape: bbox 0.494 x 0.458 x 0.697 mm, 6 faces (baked)
FEATURE [Part::Feature] Part__Feature081  label="RC0402FR-071KL RC0402N_YAG v066"
  Placement = pos=(20.405,3.8,0.805) rot=(0,0,-1;1.5708rad)
  shape: bbox 0.508 x 0.304 x 0.711 mm, 6 faces (baked)
FEATURE [Part::Feature] Part__Feature082  label="RC0402FR-071KL RC0402N_YAG v067"
  Placement = pos=(20.405,3.8,0.805) rot=(0,0,-1;1.5708rad)
  shape: bbox 0.508 x 0.304 x 0.711 mm, 6 faces (baked)
FEATURE [Part::Feature] Part__Feature083  label="RC0402FR-071KL RC0402N_YAG v069"
  Placement = pos=(21.395,3.81264,0.805) rot=(0,0,-1;1.5708rad)
  shape: bbox 0.494 x 0.458 x 0.697 mm, 6 faces (baked)
FEATURE [Part::Feature] Part__Feature084  label="RC0402FR-071KL RC0402N_YAG v070"
  Placement = pos=(21.395,3.81264,0.805) rot=(0,0,-1;1.5708rad)
  shape: bbox 0.508 x 0.304 x 0.711 mm, 6 faces (baked)
FEATURE [Part::Feature] Part__Feature085  label="RC0402FR-071KL RC0402N_YAG v071"
  Placement = pos=(21.395,3.81264,0.805) rot=(0,0,-1;1.5708rad)
  shape: bbox 0.508 x 0.304 x 0.711 mm, 6 faces (baked)
FEATURE [Part::Feature] Part__Feature086  label="RC0402FR-071KL RC0402N_YAG v073"
  Placement = pos=(25.075,13.025,0.805) rot=(0,0,-1;1.5708rad)
  shape: bbox 0.494 x 0.458 x 0.697 mm, 6 faces (baked)
FEATURE [Part::Feature] Part__Feature087  label="RC0402FR-071KL RC0402N_YAG v074"
  Placement = pos=(25.075,13.025,0.805) rot=(0,0,-1;1.5708rad)
  shape: bbox 0.508 x 0.304 x 0.711 mm, 6 faces (baked)
FEATURE [Part::Feature] Part__Feature088  label="RC0402FR-071KL RC0402N_YAG v075"
  Placement = pos=(25.075,13.025,0.805) rot=(0,0,-1;1.5708rad)
  shape: bbox 0.508 x 0.304 x 0.711 mm, 6 faces (baked)
FEATURE [Part::Feature] Part__Feature089  label="RC0402FR-071KL RC0402N_YAG v077"
  Placement = pos=(26.7,14.2,0.805) rot=(0,0,1;0rad)
  shape: bbox 0.458 x 0.494 x 0.697 mm, 6 faces (baked)
FEATURE [Part::Feature] Part__Feature090  label="RC0402FR-071KL RC0402N_YAG v078"
  Placement = pos=(26.7,14.2,0.805) rot=(0,0,1;0rad)
  shape: bbox 0.304 x 0.508 x 0.711 mm, 6 faces (baked)
FEATURE [Part::Feature] Part__Feature091  label="RC0402FR-071KL RC0402N_YAG v079"
  Placement = pos=(26.7,14.2,0.805) rot=(0,0,1;0rad)
  shape: bbox 0.304 x 0.508 x 0.711 mm, 6 faces (baked)
FEATURE [Part::Feature] Part__Feature092  label="RC0402FR-071KL RC0402N_YAG v081"
  Placement = pos=(39.625,3.32,0.805) rot=(0,0,1;0rad)
  shape: bbox 0.458 x 0.494 x 0.697 mm, 6 faces (baked)
FEATURE [Part::Feature] Part__Feature093  label="RC0402FR-071KL RC0402N_YAG v082"
  Placement = pos=(39.625,3.32,0.805) rot=(0,0,1;0rad)
  shape: bbox 0.304 x 0.508 x 0.711 mm, 6 faces (baked)
FEATURE [Part::Feature] Part__Feature094  label="RC0402FR-071KL RC0402N_YAG v083"
  Placement = pos=(39.625,3.32,0.805) rot=(0,0,1;0rad)
  shape: bbox 0.304 x 0.508 x 0.711 mm, 6 faces (baked)
FEATURE [Part::Feature] Part__Feature095  label="RC0402FR-071KL RC0402N_YAG v085"
  Placement = pos=(37.675,3.32,0.805) rot=(0,0,1;0rad)
  shape: bbox 0.458 x 0.494 x 0.697 mm, 6 faces (baked)
FEATURE [Part::Feature] Part__Feature096  label="RC0402FR-071KL RC0402N_YAG v086"
  Placement = pos=(37.675,3.32,0.805) rot=(0,0,1;0rad)
  shape: bbox 0.304 x 0.508 x 0.711 mm, 6 faces (baked)
FEATURE [Part::Feature] Part__Feature097  label="RC0402FR-071KL RC0402N_YAG v087"
  Placement = pos=(37.675,3.32,0.805) rot=(0,0,1;0rad)
  shape: bbox 0.304 x 0.508 x 0.711 mm, 6 faces (baked)
FEATURE [Part::Feature] Part__Feature098  label="RC0402FR-071KL RC0402N_YAG v089"
  Placement = pos=(35.7,3.3125,0.805) rot=(0,0,1;0rad)
  shape: bbox 0.458 x 0.494 x 0.697 mm, 6 faces (baked)
FEATURE [Part::Feature] Part__Feature099  label="RC0402FR-071KL RC0402N_YAG v090"
  Placement = pos=(35.7,3.3125,0.805) rot=(0,0,1;0rad)
  shape: bbox 0.304 x 0.508 x 0.711 mm, 6 faces (baked)
FEATURE [Part::Feature] Part__Feature100  label="RC0402FR-071KL RC0402N_YAG v091"
  Placement = pos=(35.7,3.3125,0.805) rot=(0,0,1;0rad)
  shape: bbox 0.304 x 0.508 x 0.711 mm, 6 faces (baked)
FEATURE [Part::Feature] Part__Feature101  label="RC0402FR-071KL RC0402N_YAG v093"
  Placement = pos=(25.4125,3.8125,0.805) rot=(0,0,-1;1.5708rad)
  shape: bbox 0.494 x 0.458 x 0.697 mm, 6 faces (baked)
FEATURE [Part::Feature] Part__Feature102  label="RC0402FR-071KL RC0402N_YAG v094"
  Placement = pos=(25.4125,3.8125,0.805) rot=(0,0,-1;1.5708rad)
  shape: bbox 0.508 x 0.304 x 0.711 mm, 6 faces (baked)
FEATURE [Part::Feature] Part__Feature103  label="RC0402FR-071KL RC0402N_YAG v095"
  Placement = pos=(25.4125,3.8125,0.805) rot=(0,0,-1;1.5708rad)
  shape: bbox 0.508 x 0.304 x 0.711 mm, 6 faces (baked)
FEATURE [Part::Feature] Part__Feature104  label="RC0402FR-071KL RC0402N_YAG v097"
  Placement = pos=(26.8,10.7,0.805) rot=(0,0,1;0rad)
  shape: bbox 0.458 x 0.494 x 0.697 mm, 6 faces (baked)
FEATURE [Part::Feature] Part__Feature105  label="RC0402FR-071KL RC0402N_YAG v098"
  Placement = pos=(26.8,10.7,0.805) rot=(0,0,1;0rad)
  shape: bbox 0.304 x 0.508 x 0.711 mm, 6 faces (baked)
FEATURE [Part::Feature] Part__Feature106  label="RC0402FR-071KL RC0402N_YAG v099"
  Placement = pos=(26.8,10.7,0.805) rot=(0,0,1;0rad)
  shape: bbox 0.304 x 0.508 x 0.711 mm, 6 faces (baked)
FEATURE [Part::Feature] Part__Feature107  label="RC0402FR-071KL RC0402N_YAG v101"
  Placement = pos=(19.9,14.625,0.805) rot=(0,0,1;0rad)
  shape: bbox 0.458 x 0.494 x 0.697 mm, 6 faces (baked)
FEATURE [Part::Feature] Part__Feature108  label="RC0402FR-071KL RC0402N_YAG v102"
  Placement = pos=(19.9,14.625,0.805) rot=(0,0,1;0rad)
  shape: bbox 0.304 x 0.508 x 0.711 mm, 6 faces (baked)
FEATURE [Part::Feature] Part__Feature109  label="RC0402FR-071KL RC0402N_YAG v103"
  Placement = pos=(19.9,14.625,0.805) rot=(0,0,1;0rad)
  shape: bbox 0.304 x 0.508 x 0.711 mm, 6 faces (baked)
FEATURE [Part::Feature] Part__Feature110  label="RC0402FR-071KL RC0402N_YAG v105"
  Placement = pos=(22.2,14.625,0.805) rot=(0,0,1;0rad)
  shape: bbox 0.458 x 0.494 x 0.697 mm, 6 faces (baked)
FEATURE [Part::Feature] Part__Feature111  label="RC0402FR-071KL RC0402N_YAG v106"
  Placement = pos=(22.2,14.625,0.805) rot=(0,0,1;0rad)
  shape: bbox 0.304 x 0.508 x 0.711 mm, 6 faces (baked)
FEATURE [Part::Feature] Part__Feature112  label="RC0402FR-071KL RC0402N_YAG v107"
  Placement = pos=(22.2,14.625,0.805) rot=(0,0,1;0rad)
  shape: bbox 0.304 x 0.508 x 0.711 mm, 6 faces (baked)
FEATURE [Part::Feature] Part__Feature113  label="IoT_HSMG-C190 LED v002"
  Placement = pos=(1.9,14.7,0.805) rot=(1,0,0;1.5708rad)
  shape: bbox 1.6 x 0.8 x 0.8 mm, 18 faces (baked)
FEATURE [Part::Feature] Part__Feature114  label="BLM18EG101TN1D v1"
  Placement = pos=(33.0875,2.8875,1.20467) rot=(0,0,1;0rad)
  shape: bbox 0.4 x 0.65 x 0.8 mm, 18 faces (baked)
FEATURE [Part::Feature] Part__Feature115  label="BLM18EG101TN1D v002"
  Placement = pos=(33.0875,2.8875,1.20467) rot=(0,0,1;0rad)
  shape: bbox 0.4 x 0.65 x 0.8 mm, 18 faces (baked)
FEATURE [Part::Feature] Part__Feature116  label="BLM18EG101TN1D v003"
  Placement = pos=(33.0875,2.8875,1.20467) rot=(0,0,1;0rad)
  shape: bbox 0.8 x 0.6233 x 0.7733 mm, 10 faces (baked)
FEATURE [App::Part] BLM18EG101TN1D_v1  label="BLM18EG101TN1D v004"
  Group = -> [Part__Feature114,Part__Feature115,Part__Feature116]
  Origin = -> Origin080
FEATURE [Part::Feature] Part__Feature117  label="C0805C472KDRACTU v1"
  Placement = pos=(14.1625,13,0.805333) rot=(1,0,0;1.5708rad)
  shape: bbox 0.5 x 1.25 x 1.4 mm, 18 faces (baked)
FEATURE [Part::Feature] Part__Feature118  label="C0805C472KDRACTU v002"
  Placement = pos=(14.1625,13,0.805333) rot=(1,0,0;1.5708rad)
  shape: bbox 0.5 x 1.25 x 1.4 mm, 18 faces (baked)
FEATURE [Part::Feature] Part__Feature119  label="C0805C472KDRACTU v003"
  Placement = pos=(14.1625,13,0.805333) rot=(1,0,0;1.5708rad)
  shape: bbox 1 x 1.217 x 1.367 mm, 10 faces (baked)
FEATURE [App::Part] C0805C472KDRACTU_v1  label="C0805C472KDRACTU v004"
  Group = -> [Part__Feature117,Part__Feature118,Part__Feature119]
  Origin = -> Origin081
FEATURE [Part::Feature] Part__Feature120  label="C0805C472KDRACTU v005"
  Placement = pos=(18.7875,6.0875,0.805333) rot=(0.57735,-0.57735,-0.57735;2.0944rad)
  shape: bbox 1.25 x 0.5 x 1.4 mm, 18 faces (baked)
FEATURE [Part::Feature] Part__Feature121  label="C0805C472KDRACTU v006"
  Placement = pos=(18.7875,6.0875,0.805333) rot=(0.57735,-0.57735,-0.57735;2.0944rad)
  shape: bbox 1.25 x 0.5 x 1.4 mm, 18 faces (baked)
FEATURE [Part::Feature] Part__Feature122  label="C0805C472KDRACTU v007"
  Placement = pos=(18.7875,6.0875,0.805333) rot=(0.57735,-0.57735,-0.57735;2.0944rad)
  shape: bbox 1.217 x 1 x 1.367 mm, 10 faces (baked)
FEATURE [App::Part] C0805C472KDRACTU_v002  label="C0805C472KDRACTU v008"
  Group = -> [Part__Feature120,Part__Feature121,Part__Feature122]
  Origin = -> Origin082
FEATURE [Part::Feature] Part__Feature123  label="PMEG6020AELRX v1"
  Placement = pos=(7.9,12.95,0.805) rot=(1,0,0;1.5708rad)
  shape: bbox 2.6 x 1.7 x 1.1 mm, 15 faces (baked)
FEATURE [Part::Feature] Part__Feature124  label="PMEG6020AELRX v002"
  Placement = pos=(7.9,12.95,0.805) rot=(1,0,0;1.5708rad)
  shape: bbox 0.55 x 1.569 x 0.05 mm, 6 faces (baked)
FEATURE [Part::Feature] Part__Feature125  label="PMEG6020AELRX v003"
  Placement = pos=(7.9,12.95,0.805) rot=(1,0,0;1.5708rad)
  shape: bbox 0.4612 x 0.9 x 0.16 mm, 6 faces (baked)
FEATURE [Part::Feature] Part__Feature126  label="PMEG6020AELRX v004"
  Placement = pos=(7.9,12.95,0.805) rot=(1,0,0;1.5708rad)
  shape: bbox 0.4612 x 0.9 x 0.16 mm, 6 faces (baked)
FEATURE [App::Part] PMEG6020AELRX_v1  label="PMEG6020AELRX v005"
  Group = -> [Part__Feature123,Part__Feature124,Part__Feature125,Part__Feature126]
  Origin = -> Origin083
FEATURE [Part::Feature] Part__Feature127  label="C0805C472KDRACTU v009"
  Placement = pos=(6.8675,6.425,0.805333) rot=(1,0,0;1.5708rad)
  shape: bbox 0.5 x 1.25 x 1.4 mm, 18 faces (baked)
FEATURE [Part::Feature] Part__Feature128  label="C0805C472KDRACTU v010"
  Placement = pos=(6.8675,6.425,0.805333) rot=(1,0,0;1.5708rad)
  shape: bbox 0.5 x 1.25 x 1.4 mm, 18 faces (baked)
FEATURE [Part::Feature] Part__Feature129  label="C0805C472KDRACTU v011"
  Placement = pos=(6.8675,6.425,0.805333) rot=(1,0,0;1.5708rad)
  shape: bbox 1 x 1.217 x 1.367 mm, 10 faces (baked)
FEATURE [App::Part] C0805C472KDRACTU_v003  label="C0805C472KDRACTU v012"
  Group = -> [Part__Feature127,Part__Feature128,Part__Feature129]
  Origin = -> Origin084
FEATURE [Part::Feature] Part__Feature130  label="IoT_PRTR5V0U2X Protection Diode v1"
  Placement = pos=(7.23,9.3,1.455) rot=(1,0,0;1.5708rad)
  shape: bbox 3 x 2.5 x 1.1 mm, 139 faces (baked)
FEATURE [Part::Feature] Part__Feature131  label="NINA-B306-00B-00--3DModel-STEP-56544 v1"
  Placement = pos=(35.642,8.89,0.805) rot=(0.57735,0.57735,0.57735;2.0944rad)
  shape: bbox 0.7 x 0.7 x 0.05 mm, 6 faces (baked)
FEATURE [Part::Feature] Part__Feature132  label="NINA-B306-00B-00--3DModel-STEP-56544 v002"
  Placement = pos=(35.642,8.89,0.805) rot=(0.57735,0.57735,0.57735;2.0944rad)
  shape: bbox 1.15 x 0.7 x 0.05 mm, 6 faces (baked)
FEATURE [Part::Feature] Part__Feature133  label="NINA-B306-00B-00--3DModel-STEP-56544 v003"
  Placement = pos=(35.642,8.89,0.805) rot=(0.57735,0.57735,0.57735;2.0944rad)
  shape: bbox 0.7 x 1.15 x 0.05 mm, 6 faces (baked)
FEATURE [Part::Feature] Part__Feature134  label="NINA-B306-00B-00--3DModel-STEP-56544 v004"
  Placement = pos=(35.642,8.89,0.805) rot=(0.57735,0.57735,0.57735;2.0944rad)
  shape: bbox 1.15 x 0.7 x 0.05 mm, 6 faces (baked)
FEATURE [Part::Feature] Part__Feature135  label="NINA-B306-00B-00--3DModel-STEP-56544 v005"
  Placement = pos=(35.642,8.89,0.805) rot=(0.57735,0.57735,0.57735;2.0944rad)
  shape: bbox 0.7 x 0.7 x 0.05 mm, 6 faces (baked)
FEATURE [Part::Feature] Part__Feature136  label="NINA-B306-00B-00--3DModel-STEP-56544 v006"
  Placement = pos=(35.642,8.89,0.805) rot=(0.57735,0.57735,0.57735;2.0944rad)
  shape: bbox 0.7 x 0.7 x 0.05 mm, 6 faces (baked)
FEATURE [Part::Feature] Part__Feature137  label="NINA-B306-00B-00--3DModel-STEP-56544 v007"
  Placement = pos=(35.642,8.89,0.805) rot=(0.57735,0.57735,0.57735;2.0944rad)
  shape: bbox 0.325 x 0.165 x 0.25 mm, 6 faces (baked)
FEATURE [Part::Feature] Part__Feature138  label="NINA-B306-00B-00--3DModel-STEP-56544 v008"
  Placement = pos=(35.642,8.89,0.805) rot=(0.57735,0.57735,0.57735;2.0944rad)
  shape: bbox 0.7 x 1.15 x 0.05 mm, 6 faces (baked)
FEATURE [Part::Feature] Part__Feature139  label="NINA-B306-00B-00--3DModel-STEP-56544 v009"
  Placement = pos=(35.642,8.89,0.805) rot=(0.57735,0.57735,0.57735;2.0944rad)
  shape: bbox 0.325 x 0.295 x 0.25 mm, 6 faces (baked)
FEATURE [Part::Feature] Part__Feature140  label="NINA-B306-00B-00--3DModel-STEP-56544 v010"
  Placement = pos=(35.642,8.89,0.805) rot=(0.57735,0.57735,0.57735;2.0944rad)
  shape: bbox 0.7 x 0.7 x 0.05 mm, 6 faces (baked)
FEATURE [Part::Feature] Part__Feature141  label="NINA-B306-00B-00--3DModel-STEP-56544 v011"
  Placement = pos=(35.642,8.89,0.805) rot=(0.57735,0.57735,0.57735;2.0944rad)
  shape: bbox 0.7 x 0.7 x 0.05 mm, 6 faces (baked)
FEATURE [Part::Feature] Part__Feature142  label="NINA-B306-00B-00--3DModel-STEP-56544 v012"
  Placement = pos=(35.642,8.89,0.805) rot=(0.57735,0.57735,0.57735;2.0944rad)
  shape: bbox 0.7 x 1.15 x 0.05 mm, 6 faces (baked)
FEATURE [Part::Feature] Part__Feature143  label="NINA-B306-00B-00--3DModel-STEP-56544 v013"
  Placement = pos=(35.642,8.89,0.805) rot=(0.57735,0.57735,0.57735;2.0944rad)
  shape: bbox 0.325 x 0.165 x 0.25 mm, 6 faces (baked)
FEATURE [Part::Feature] Part__Feature144  label="NINA-B306-00B-00--3DModel-STEP-56544 v014"
  Placement = pos=(35.642,8.89,0.805) rot=(0.57735,0.57735,0.57735;2.0944rad)
  shape: bbox 0.7 x 0.7 x 0.05 mm, 6 faces (baked)
FEATURE [Part::Feature] Part__Feature145  label="NINA-B306-00B-00--3DModel-STEP-56544 v015"
  Placement = pos=(35.642,8.89,0.805) rot=(0.57735,0.57735,0.57735;2.0944rad)
  shape: bbox 0.7 x 0.7 x 0.05 mm, 6 faces (baked)
FEATURE [Part::Feature] Part__Feature146  label="NINA-B306-00B-00--3DModel-STEP-56544 v016"
  Placement = pos=(35.642,8.89,0.805) rot=(0.57735,0.57735,0.57735;2.0944rad)
  shape: bbox 0.7 x 0.7 x 0.05 mm, 6 faces (baked)
FEATURE [Part::Feature] Part__Feature147  label="NINA-B306-00B-00--3DModel-STEP-56544 v017"
  Placement = pos=(35.642,8.89,0.805) rot=(0.57735,0.57735,0.57735;2.0944rad)
  shape: bbox 0.7 x 0.7 x 0.05 mm, 6 faces (baked)
FEATURE [Part::Feature] Part__Feature148  label="NINA-B306-00B-00--3DModel-STEP-56544 v018"
  Placement = pos=(35.642,8.89,0.805) rot=(0.57735,0.57735,0.57735;2.0944rad)
  shape: bbox 15 x 10 x 0.9 mm, 361 faces (baked)
FEATURE [Part::Feature] Part__Feature149  label="NINA-B306-00B-00--3DModel-STEP-56544 v019"
  Placement = pos=(35.642,8.89,0.805) rot=(0.57735,0.57735,0.57735;2.0944rad)
  shape: bbox 0.7 x 1.15 x 0.05 mm, 6 faces (baked)
FEATURE [Part::Feature] Part__Feature150  label="NINA-B306-00B-00--3DModel-STEP-56544 v020"
  Placement = pos=(35.642,8.89,0.805) rot=(0.57735,0.57735,0.57735;2.0944rad)
  shape: bbox 1.15 x 0.7 x 0.05 mm, 6 faces (baked)
FEATURE [Part::Feature] Part__Feature151  label="NINA-B306-00B-00--3DModel-STEP-56544 v021"
  Placement = pos=(35.642,8.89,0.805) rot=(0.57735,0.57735,0.57735;2.0944rad)
  shape: bbox 0.7 x 1.15 x 0.05 mm, 6 faces (baked)
FEATURE [Part::Feature] Part__Feature152  label="NINA-B306-00B-00--3DModel-STEP-56544 v022"
  Placement = pos=(35.642,8.89,0.805) rot=(0.57735,0.57735,0.57735;2.0944rad)
  shape: bbox 1.15 x 0.7 x 0.05 mm, 6 faces (baked)
FEATURE [Part::Feature] Part__Feature153  label="NINA-B306-00B-00--3DModel-STEP-56544 v023"
  Placement = pos=(35.642,8.89,0.805) rot=(0.57735,0.57735,0.57735;2.0944rad)
  shape: bbox 0.7 x 0.7 x 0.05 mm, 6 faces (baked)
FEATURE [Part::Feature] Part__Feature154  label="NINA-B306-00B-00--3DModel-STEP-56544 v024"
  Placement = pos=(35.642,8.89,0.805) rot=(0.57735,0.57735,0.57735;2.0944rad)
  shape: bbox 0.7 x 0.7 x 0.05 mm, 6 faces (baked)
FEATURE [Part::Feature] Part__Feature155  label="NINA-B306-00B-00--3DModel-STEP-56544 v025"
  Placement = pos=(35.642,8.89,0.805) rot=(0.57735,0.57735,0.57735;2.0944rad)
  shape: bbox 0.165 x 0.325 x 0.25 mm, 6 faces (baked)
FEATURE [Part::Feature] Part__Feature156  label="NINA-B306-00B-00--3DModel-STEP-56544 v026"
  Placement = pos=(35.642,8.89,0.805) rot=(0.57735,0.57735,0.57735;2.0944rad)
  shape: bbox 0.7 x 0.7 x 0.05 mm, 6 faces (baked)
FEATURE [Part::Feature] Part__Feature157  label="NINA-B306-00B-00--3DModel-STEP-56544 v027"
  Placement = pos=(35.642,8.89,0.805) rot=(0.57735,0.57735,0.57735;2.0944rad)
  shape: bbox 0.295 x 0.325 x 0.25 mm, 6 faces (baked)
FEATURE [Part::Feature] Part__Feature158  label="NINA-B306-00B-00--3DModel-STEP-56544 v028"
  Placement = pos=(35.642,8.89,0.805) rot=(0.57735,0.57735,0.57735;2.0944rad)
  shape: bbox 0.7 x 1.15 x 0.05 mm, 6 faces (baked)
FEATURE [Part::Feature] Part__Feature159  label="NINA-B306-00B-00--3DModel-STEP-56544 v029"
  Placement = pos=(35.642,8.89,0.805) rot=(0.57735,0.57735,0.57735;2.0944rad)
  shape: bbox 0.165 x 0.325 x 0.25 mm, 6 faces (baked)
FEATURE [Part::Feature] Part__Feature160  label="NINA-B306-00B-00--3DModel-STEP-56544 v030"
  Placement = pos=(35.642,8.89,0.805) rot=(0.57735,0.57735,0.57735;2.0944rad)
  shape: bbox 0.7 x 0.7 x 0.05 mm, 6 faces (baked)
FEATURE [Part::Feature] Part__Feature161  label="NINA-B306-00B-00--3DModel-STEP-56544 v031"
  Placement = pos=(35.642,8.89,0.805) rot=(0.57735,0.57735,0.57735;2.0944rad)
  shape: bbox 0.7 x 1.15 x 0.05 mm, 6 faces (baked)
FEATURE [Part::Feature] Part__Feature162  label="NINA-B306-00B-00--3DModel-STEP-56544 v032"
  Placement = pos=(35.642,8.89,0.805) rot=(0.57735,0.57735,0.57735;2.0944rad)
  shape: bbox 0.7 x 0.7 x 0.05 mm, 6 faces (baked)
FEATURE [Part::Feature] Part__Feature163  label="NINA-B306-00B-00--3DModel-STEP-56544 v033"
  Placement = pos=(35.642,8.89,0.805) rot=(0.57735,0.57735,0.57735;2.0944rad)
  shape: bbox 0.7 x 0.7 x 0.05 mm, 6 faces (baked)
FEATURE [Part::Feature] Part__Feature164  label="NINA-B306-00B-00--3DModel-STEP-56544 v034"
  Placement = pos=(35.642,8.89,0.805) rot=(0.57735,0.57735,0.57735;2.0944rad)
  shape: bbox 0.7 x 0.7 x 0.05 mm, 6 faces (baked)
FEATURE [Part::Feature] Part__Feature467  label="NINA-B306-00B-00--3DModel-STEP-56544 v035"
  Placement = pos=(35.642,8.89,0.805) rot=(0.57735,0.57735,0.57735;2.0944rad)
  shape: bbox 0.7 x 1.15 x 0.05 mm, 6 faces (baked)
FEATURE [Part::Feature] Part__Feature468  label="NINA-B306-00B-00--3DModel-STEP-56544 v036"
  Placement = pos=(35.642,8.89,0.805) rot=(0.57735,0.57735,0.57735;2.0944rad)
  shape: bbox 0.7 x 1.15 x 0.05 mm, 6 faces (baked)
FEATURE [Part::Feature] Part__Feature469  label="NINA-B306-00B-00--3DModel-STEP-56544 v037"
  Placement = pos=(35.642,8.89,0.805) rot=(0.57735,0.57735,0.57735;2.0944rad)
  shape: bbox 1.15 x 0.7 x 0.05 mm, 6 faces (baked)
FEATURE [Part::Feature] Part__Feature470  label="NINA-B306-00B-00--3DModel-STEP-56544 v038"
  Placement = pos=(35.642,8.89,0.805) rot=(0.57735,0.57735,0.57735;2.0944rad)
  shape: bbox 0.7 x 0.7 x 0.05 mm, 6 faces (baked)
FEATURE [Part::Feature] Part__Feature471  label="NINA-B306-00B-00--3DModel-STEP-56544 v039"
  Placement = pos=(35.642,8.89,0.805) rot=(0.57735,0.57735,0.57735;2.0944rad)
  shape: bbox 1.15 x 0.7 x 0.05 mm, 6 faces (baked)
FEATURE [Part::Feature] Part__Feature472  label="NINA-B306-00B-00--3DModel-STEP-56544 v040"
  Placement = pos=(35.642,8.89,0.805) rot=(0.57735,0.57735,0.57735;2.0944rad)
  shape: bbox 0.7 x 0.7 x 0.05 mm, 6 faces (baked)
FEATURE [Part::Feature] Part__Feature473  label="NINA-B306-00B-00--3DModel-STEP-56544 v041"
  Placement = pos=(35.642,8.89,0.805) rot=(0.57735,0.57735,0.57735;2.0944rad)
  shape: bbox 0.7 x 0.7 x 0.05 mm, 6 faces (baked)
FEATURE [Part::Feature] Part__Feature474  label="NINA-B306-00B-00--3DModel-STEP-56544 v042"
  Placement = pos=(35.642,8.89,0.805) rot=(0.57735,0.57735,0.57735;2.0944rad)
  shape: bbox 0.325 x 0.165 x 0.25 mm, 6 faces (baked)
FEATURE [Part::Feature] Part__Feature475  label="NINA-B306-00B-00--3DModel-STEP-56544 v043"
  Placement = pos=(35.642,8.89,0.805) rot=(0.57735,0.57735,0.57735;2.0944rad)
  shape: bbox 0.7 x 0.7 x 0.05 mm, 6 faces (baked)
FEATURE [Part::Feature] Part__Feature476  label="NINA-B306-00B-00--3DModel-STEP-56544 v044"
  Placement = pos=(35.642,8.89,0.805) rot=(0.57735,0.57735,0.57735;2.0944rad)
  shape: bbox 0.325 x 0.295 x 0.25 mm, 6 faces (baked)
FEATURE [Part::Feature] Part__Feature477  label="NINA-B306-00B-00--3DModel-STEP-56544 v045"
  Placement = pos=(35.642,8.89,0.805) rot=(0.57735,0.57735,0.57735;2.0944rad)
  shape: bbox 0.7 x 1.15 x 0.05 mm, 6 faces (baked)
FEATURE [Part::Feature] Part__Feature478  label="NINA-B306-00B-00--3DModel-STEP-56544 v046"
  Placement = pos=(35.642,8.89,0.805) rot=(0.57735,0.57735,0.57735;2.0944rad)
  shape: bbox 0.325 x 0.165 x 0.25 mm, 6 faces (baked)
FEATURE [Part::Feature] Part__Feature479  label="NINA-B306-00B-00--3DModel-STEP-56544 v047"
  Placement = pos=(35.642,8.89,0.805) rot=(0.57735,0.57735,0.57735;2.0944rad)
  shape: bbox 0.7 x 0.7 x 0.05 mm, 6 faces (baked)
FEATURE [Part::Feature] Part__Feature480  label="NINA-B306-00B-00--3DModel-STEP-56544 v048"
  Placement = pos=(35.642,8.89,0.805) rot=(0.57735,0.57735,0.57735;2.0944rad)
  shape: bbox 0.7 x 1.15 x 0.05 mm, 6 faces (baked)
FEATURE [Part::Feature] Part__Feature481  label="NINA-B306-00B-00--3DModel-STEP-56544 v049"
  Placement = pos=(35.642,8.89,0.805) rot=(0.57735,0.57735,0.57735;2.0944rad)
  shape: bbox 0.7 x 0.7 x 0.05 mm, 6 faces (baked)
FEATURE [Part::Feature] Part__Feature482  label="NINA-B306-00B-00--3DModel-STEP-56544 v050"
  Placement = pos=(35.642,8.89,0.805) rot=(0.57735,0.57735,0.57735;2.0944rad)
  shape: bbox 0.7 x 0.7 x 0.05 mm, 6 faces (baked)
FEATURE [Part::Feature] Part__Feature483  label="NINA-B306-00B-00--3DModel-STEP-56544 v051"
  Placement = pos=(35.642,8.89,0.805) rot=(0.57735,0.57735,0.57735;2.0944rad)
  shape: bbox 0.7 x 0.7 x 0.05 mm, 6 faces (baked)
FEATURE [Part::Feature] Part__Feature484  label="NINA-B306-00B-00--3DModel-STEP-56544 v052"
  Placement = pos=(35.642,8.89,0.805) rot=(0.57735,0.57735,0.57735;2.0944rad)
  shape: bbox 0.7 x 1.15 x 0.05 mm, 6 faces (baked)
FEATURE [Part::Feature] Part__Feature485  label="NINA-B306-00B-00--3DModel-STEP-56544 v053"
  Placement = pos=(35.642,8.89,0.805) rot=(0.57735,0.57735,0.57735;2.0944rad)
  shape: bbox 0.7 x 1.15 x 0.05 mm, 6 faces (baked)
FEATURE [Part::Feature] Part__Feature486  label="NINA-B306-00B-00--3DModel-STEP-56544 v054"
  Placement = pos=(35.642,8.89,0.805) rot=(0.57735,0.57735,0.57735;2.0944rad)
  shape: bbox 1.15 x 0.7 x 0.05 mm, 6 faces (baked)
FEATURE [Part::Feature] Part__Feature487  label="NINA-B306-00B-00--3DModel-STEP-56544 v055"
  Placement = pos=(35.642,8.89,0.805) rot=(0.57735,0.57735,0.57735;2.0944rad)
  shape: bbox 0.7 x 0.7 x 0.05 mm, 6 faces (baked)
FEATURE [Part::Feature] Part__Feature488  label="NINA-B306-00B-00--3DModel-STEP-56544 v056"
  Placement = pos=(35.642,8.89,0.805) rot=(0.57735,0.57735,0.57735;2.0944rad)
  shape: bbox 0.7 x 0.7 x 0.05 mm, 6 faces (baked)
FEATURE [Part::Feature] Part__Feature489  label="NINA-B306-00B-00--3DModel-STEP-56544 v057"
  Placement = pos=(35.642,8.89,0.805) rot=(0.57735,0.57735,0.57735;2.0944rad)
  shape: bbox 0.7 x 1.15 x 0.05 mm, 6 faces (baked)
FEATURE [Part::Feature] Part__Feature490  label="NINA-B306-00B-00--3DModel-STEP-56544 v058"
  Placement = pos=(35.642,8.89,0.805) rot=(0.57735,0.57735,0.57735;2.0944rad)
  shape: bbox 0.7 x 0.7 x 0.05 mm, 6 faces (baked)
FEATURE [Part::Feature] Part__Feature491  label="NINA-B306-00B-00--3DModel-STEP-56544 v059"
  Placement = pos=(35.642,8.89,0.805) rot=(0.57735,0.57735,0.57735;2.0944rad)
  shape: bbox 0.325 x 0.165 x 0.25 mm, 6 faces (baked)
FEATURE [Part::Feature] Part__Feature492  label="NINA-B306-00B-00--3DModel-STEP-56544 v060"
  Placement = pos=(35.642,8.89,0.805) rot=(0.57735,0.57735,0.57735;2.0944rad)
  shape: bbox 0.7 x 1.15 x 0.05 mm, 6 faces (baked)
FEATURE [Part::Feature] Part__Feature493  label="NINA-B306-00B-00--3DModel-STEP-56544 v061"
  Placement = pos=(35.642,8.89,0.805) rot=(0.57735,0.57735,0.57735;2.0944rad)
  shape: bbox 0.325 x 0.295 x 0.25 mm, 6 faces (baked)
FEATURE [Part::Feature] Part__Feature494  label="NINA-B306-00B-00--3DModel-STEP-56544 v062"
  Placement = pos=(35.642,8.89,0.805) rot=(0.57735,0.57735,0.57735;2.0944rad)
  shape: bbox 0.7 x 0.7 x 0.05 mm, 6 faces (baked)
FEATURE [Part::Feature] Part__Feature495  label="NINA-B306-00B-00--3DModel-STEP-56544 v063"
  Placement = pos=(35.642,8.89,0.805) rot=(0.57735,0.57735,0.57735;2.0944rad)
  shape: bbox 0.7 x 0.7 x 0.05 mm, 6 faces (baked)
FEATURE [Part::Feature] Part__Feature496  label="NINA-B306-00B-00--3DModel-STEP-56544 v064"
  Placement = pos=(35.642,8.89,0.805) rot=(0.57735,0.57735,0.57735;2.0944rad)
  shape: bbox 0.325 x 0.165 x 0.25 mm, 6 faces (baked)
FEATURE [Part::Feature] Part__Feature497  label="NINA-B306-00B-00--3DModel-STEP-56544 v065"
  Placement = pos=(35.642,8.89,0.805) rot=(0.57735,0.57735,0.57735;2.0944rad)
  shape: bbox 0.7 x 0.7 x 0.05 mm, 6 faces (baked)
FEATURE [Part::Feature] Part__Feature498  label="NINA-B306-00B-00--3DModel-STEP-56544 v066"
  Placement = pos=(35.642,8.89,0.805) rot=(0.57735,0.57735,0.57735;2.0944rad)
  shape: bbox 0.7 x 0.7 x 0.05 mm, 6 faces (baked)
FEATURE [Part::Feature] Part__Feature499  label="NINA-B306-00B-00--3DModel-STEP-56544 v067"
  Placement = pos=(35.642,8.89,0.805) rot=(0.57735,0.57735,0.57735;2.0944rad)
  shape: bbox 0.7 x 0.7 x 0.05 mm, 6 faces (baked)
FEATURE [Part::Feature] Part__Feature500  label="NINA-B306-00B-00--3DModel-STEP-56544 v068"
  Placement = pos=(35.642,8.89,0.805) rot=(0.57735,0.57735,0.57735;2.0944rad)
  shape: bbox 0.7 x 1.15 x 0.05 mm, 6 faces (baked)
FEATURE [Part::Feature] Part__Feature501  label="NINA-B306-00B-00--3DModel-STEP-56544 v069"
  Placement = pos=(35.642,8.89,0.805) rot=(0.57735,0.57735,0.57735;2.0944rad)
  shape: bbox 10.65 x 9.8 x 1.73 mm, 51 faces (baked)
FEATURE [Part::Feature] Part__Feature502  label="NINA-B306-00B-00--3DModel-STEP-56544 v070"
  Placement = pos=(35.642,8.89,0.805) rot=(0.57735,0.57735,0.57735;2.0944rad)
  shape: bbox 0.7 x 0.7 x 0.05 mm, 6 faces (baked)
FEATURE [Part::Feature] Part__Feature503  label="NINA-B306-00B-00--3DModel-STEP-56544 v071"
  Placement = pos=(35.642,8.89,0.805) rot=(0.57735,0.57735,0.57735;2.0944rad)
  shape: bbox 1.15 x 0.7 x 0.05 mm, 6 faces (baked)
FEATURE [Part::Feature] Part__Feature504  label="NINA-B306-00B-00--3DModel-STEP-56544 v072"
  Placement = pos=(35.642,8.89,0.805) rot=(0.57735,0.57735,0.57735;2.0944rad)
  shape: bbox 0.7 x 0.7 x 0.05 mm, 6 faces (baked)
FEATURE [Part::Feature] Part__Feature505  label="NINA-B306-00B-00--3DModel-STEP-56544 v073"
  Placement = pos=(35.642,8.89,0.805) rot=(0.57735,0.57735,0.57735;2.0944rad)
  shape: bbox 1.15 x 0.7 x 0.05 mm, 6 faces (baked)
FEATURE [Part::Feature] Part__Feature506  label="NINA-B306-00B-00--3DModel-STEP-56544 v074"
  Placement = pos=(35.642,8.89,0.805) rot=(0.57735,0.57735,0.57735;2.0944rad)
  shape: bbox 0.7 x 1.15 x 0.05 mm, 6 faces (baked)
FEATURE [Part::Feature] Part__Feature507  label="NINA-B306-00B-00--3DModel-STEP-56544 v075"
  Placement = pos=(35.642,8.89,0.805) rot=(0.57735,0.57735,0.57735;2.0944rad)
  shape: bbox 0.7 x 0.7 x 0.05 mm, 6 faces (baked)
FEATURE [Part::Feature] Part__Feature508  label="NINA-B306-00B-00--3DModel-STEP-56544 v076"
  Placement = pos=(35.642,8.89,0.805) rot=(0.57735,0.57735,0.57735;2.0944rad)
  shape: bbox 0.325 x 0.165 x 0.25 mm, 6 faces (baked)
FEATURE [Part::Feature] Part__Feature509  label="NINA-B306-00B-00--3DModel-STEP-56544 v077"
  Placement = pos=(35.642,8.89,0.805) rot=(0.57735,0.57735,0.57735;2.0944rad)
  shape: bbox 0.7 x 1.15 x 0.05 mm, 6 faces (baked)
FEATURE [Part::Feature] Part__Feature510  label="NINA-B306-00B-00--3DModel-STEP-56544 v078"
  Placement = pos=(35.642,8.89,0.805) rot=(0.57735,0.57735,0.57735;2.0944rad)
  shape: bbox 0.7 x 0.7 x 0.05 mm, 6 faces (baked)
FEATURE [Part::Feature] Part__Feature511  label="NINA-B306-00B-00--3DModel-STEP-56544 v079"
  Placement = pos=(35.642,8.89,0.805) rot=(0.57735,0.57735,0.57735;2.0944rad)
  shape: bbox 0.325 x 0.295 x 0.25 mm, 6 faces (baked)
FEATURE [Part::Feature] Part__Feature512  label="NINA-B306-00B-00--3DModel-STEP-56544 v080"
  Placement = pos=(35.642,8.89,0.805) rot=(0.57735,0.57735,0.57735;2.0944rad)
  shape: bbox 0.7 x 0.7 x 0.05 mm, 6 faces (baked)
FEATURE [Part::Feature] Part__Feature513  label="NINA-B306-00B-00--3DModel-STEP-56544 v081"
  Placement = pos=(35.642,8.89,0.805) rot=(0.57735,0.57735,0.57735;2.0944rad)
  shape: bbox 0.7 x 0.7 x 0.05 mm, 6 faces (baked)
FEATURE [Part::Feature] Part__Feature514  label="NINA-B306-00B-00--3DModel-STEP-56544 v082"
  Placement = pos=(35.642,8.89,0.805) rot=(0.57735,0.57735,0.57735;2.0944rad)
  shape: bbox 0.325 x 0.165 x 0.25 mm, 6 faces (baked)
FEATURE [Part::Feature] Part__Feature515  label="NINA-B306-00B-00--3DModel-STEP-56544 v083"
  Placement = pos=(35.642,8.89,0.805) rot=(0.57735,0.57735,0.57735;2.0944rad)
  shape: bbox 0.7 x 0.7 x 0.05 mm, 6 faces (baked)
FEATURE [Part::Feature] Part__Feature516  label="NINA-B306-00B-00--3DModel-STEP-56544 v084"
  Placement = pos=(35.642,8.89,0.805) rot=(0.57735,0.57735,0.57735;2.0944rad)
  shape: bbox 0.7 x 1.15 x 0.05 mm, 6 faces (baked)
FEATURE [Part::Feature] Part__Feature517  label="NINA-B306-00B-00--3DModel-STEP-56544 v085"
  Placement = pos=(35.642,8.89,0.805) rot=(0.57735,0.57735,0.57735;2.0944rad)
  shape: bbox 0.7 x 0.7 x 0.05 mm, 6 faces (baked)
FEATURE [Part::Feature] Part__Feature518  label="NINA-B306-00B-00--3DModel-STEP-56544 v086"
  Placement = pos=(35.642,8.89,0.805) rot=(0.57735,0.57735,0.57735;2.0944rad)
  shape: bbox 0.7 x 1.15 x 0.05 mm, 6 faces (baked)
FEATURE [Part::Feature] Part__Feature519  label="NINA-B306-00B-00--3DModel-STEP-56544 v087"
  Placement = pos=(35.642,8.89,0.805) rot=(0.57735,0.57735,0.57735;2.0944rad)
  shape: bbox 0.7 x 0.7 x 0.05 mm, 6 faces (baked)
FEATURE [Part::Feature] Part__Feature520  label="NINA-B306-00B-00--3DModel-STEP-56544 v088"
  Placement = pos=(35.642,8.89,0.805) rot=(0.57735,0.57735,0.57735;2.0944rad)
  shape: bbox 1.15 x 0.7 x 0.05 mm, 6 faces (baked)
FEATURE [App::Part] NINA_B306_00B_00__3DModel_STEP_56544_v1  label="NINA-B306-00B-00--3DModel-STEP-56544 v089"
  Group = -> [Part__Feature131,Part__Feature132,Part__Feature133,Part__Feature134,Part__Feature135,Part__Feature136,Part__Feature137,Part__Feature138,Part__Feature139,Part__Feature140,Part__Feature141,Part__Feature142,Part__Feature143,Part__Feature144,Part__Feature145,Part__Feature146,Part__Feature147,Part__Feature148,Part__Feature149,Part__Feature150,Part__Feature151,Part__Feature152,Part__Feature153,+65 more]
  Origin = -> Origin085
FEATURE [Part::Feature] Part__Feature521  label="I2C SPLITTER001"
  shape: bbox 8.151 x 3.401 x 4.801 mm, 98 faces (baked)
FEATURE [Part::Feature] Part__Feature522  label="I2C SPLITTER002"
  shape: bbox 0.3504 x 3.865 x 4.2 mm, 18 faces (baked)
FEATURE [Part::Feature] Part__Feature221  label="I2C SPLITTER003"
  shape: bbox 0.3504 x 3.865 x 4.2 mm, 18 faces (baked)
FEATURE [Part::Feature] Part__Feature222  label="I2C SPLITTER004"
  shape: bbox 0.3504 x 3.865 x 4.2 mm, 18 faces (baked)
FEATURE [Part::Feature] Part__Feature223  label="I2C SPLITTER005"
  shape: bbox 0.3504 x 3.865 x 4.2 mm, 18 faces (baked)
FEATURE [Part::MultiFuse] Fusion045  label="i2c"
  Placement = pos=(17.82,2.2,-0.25) rot=(0,0,1;0rad)
  Shapes = -> [Part__Feature521,Part__Feature522,Part__Feature221,Part__Feature222,Part__Feature223]
FEATURE [App::Part] RC0402FR_071KL_RC0402N_YAG_v002  label="RC0402FR-071KL RC0402N_YAG v008"
  Group = -> [Part__Feature445,Part__Feature446,Part__Feature447]
  Origin = -> Origin055
FEATURE [App::Part] RC0402FR_071KL_RC0402N_YAG_v003  label="RC0402FR-071KL RC0402N_YAG v012"
  Group = -> [Part__Feature448,Part__Feature449,Part__Feature450]
  Origin = -> Origin056
FEATURE [App::Part] RC0402FR_071KL_RC0402N_YAG_v004  label="RC0402FR-071KL RC0402N_YAG v016"
  Group = -> [Part__Feature451,Part__Feature452,Part__Feature453]
  Origin = -> Origin057
FEATURE [App::Part] RC0402FR_071KL_RC0402N_YAG_v005  label="RC0402FR-071KL RC0402N_YAG v020"
  Group = -> [Part__Feature454,Part__Feature455,Part__Feature456]
  Origin = -> Origin058
FEATURE [App::Part] RC0402FR_071KL_RC0402N_YAG_v006  label="RC0402FR-071KL RC0402N_YAG v024"
  Group = -> [Part__Feature457,Part__Feature458,Part__Feature459]
  Origin = -> Origin059
FEATURE [App::Part] RC0402FR_071KL_RC0402N_YAG_v007  label="RC0402FR-071KL RC0402N_YAG v028"
  Group = -> [Part__Feature460,Part__Feature461,Part__Feature462]
  Origin = -> Origin060
FEATURE [App::Part] RC0402FR_071KL_RC0402N_YAG_v008  label="RC0402FR-071KL RC0402N_YAG v032"
  Group = -> [Part__Feature463,Part__Feature464,Part__Feature465]
  Origin = -> Origin061
FEATURE [App::Part] RC0402FR_071KL_RC0402N_YAG_v009  label="RC0402FR-071KL RC0402N_YAG v036"
  Group = -> [Part__Feature056,Part__Feature057,Part__Feature466]
  Origin = -> Origin062
FEATURE [App::Part] RC0402FR_071KL_RC0402N_YAG_v010  label="RC0402FR-071KL RC0402N_YAG v040"
  Group = -> [Part__Feature059,Part__Feature060,Part__Feature061]
  Origin = -> Origin063
FEATURE [App::Part] RC0402FR_071KL_RC0402N_YAG_v011  label="RC0402FR-071KL RC0402N_YAG v044"
  Group = -> [Part__Feature062,Part__Feature063,Part__Feature064]
  Origin = -> Origin064
FEATURE [App::Part] RC0402FR_071KL_RC0402N_YAG_v012  label="RC0402FR-071KL RC0402N_YAG v048"
  Group = -> [Part__Feature065,Part__Feature066,Part__Feature067]
  Origin = -> Origin015
FEATURE [App::Part] RC0402FR_071KL_RC0402N_YAG_v013  label="RC0402FR-071KL RC0402N_YAG v052"
  Group = -> [Part__Feature068,Part__Feature069,Part__Feature070]
  Origin = -> Origin065
FEATURE [App::Part] RC0402FR_071KL_RC0402N_YAG_v014  label="RC0402FR-071KL RC0402N_YAG v056"
  Group = -> [Part__Feature071,Part__Feature072,Part__Feature073]
  Origin = -> Origin066
FEATURE [App::Part] RC0402FR_071KL_RC0402N_YAG_v015  label="RC0402FR-071KL RC0402N_YAG v060"
  Group = -> [Part__Feature074,Part__Feature075,Part__Feature076]
  Origin = -> Origin067
FEATURE [App::Part] RC0402FR_071KL_RC0402N_YAG_v016  label="RC0402FR-071KL RC0402N_YAG v064"
  Group = -> [Part__Feature077,Part__Feature078,Part__Feature079]
  Origin = -> Origin068
FEATURE [App::Part] RC0402FR_071KL_RC0402N_YAG_v017  label="RC0402FR-071KL RC0402N_YAG v068"
  Group = -> [Part__Feature080,Part__Feature081,Part__Feature082]
  Origin = -> Origin069
FEATURE [App::Part] RC0402FR_071KL_RC0402N_YAG_v018  label="RC0402FR-071KL RC0402N_YAG v072"
  Group = -> [Part__Feature083,Part__Feature084,Part__Feature085]
  Origin = -> Origin021
FEATURE [App::Part] RC0402FR_071KL_RC0402N_YAG_v019  label="RC0402FR-071KL RC0402N_YAG v076"
  Group = -> [Part__Feature086,Part__Feature087,Part__Feature088]
  Origin = -> Origin070
FEATURE [App::Part] RC0402FR_071KL_RC0402N_YAG_v020  label="RC0402FR-071KL RC0402N_YAG v080"
  Group = -> [Part__Feature089,Part__Feature090,Part__Feature091]
  Origin = -> Origin071
FEATURE [App::Part] RC0402FR_071KL_RC0402N_YAG_v021  label="RC0402FR-071KL RC0402N_YAG v084"
  Group = -> [Part__Feature092,Part__Feature093,Part__Feature094]
  Origin = -> Origin072
FEATURE [App::Part] RC0402FR_071KL_RC0402N_YAG_v022  label="RC0402FR-071KL RC0402N_YAG v088"
  Group = -> [Part__Feature095,Part__Feature096,Part__Feature097]
  Origin = -> Origin073
FEATURE [App::Part] RC0402FR_071KL_RC0402N_YAG_v023  label="RC0402FR-071KL RC0402N_YAG v092"
  Group = -> [Part__Feature098,Part__Feature099,Part__Feature100]
  Origin = -> Origin074
FEATURE [App::Part] RC0402FR_071KL_RC0402N_YAG_v024  label="RC0402FR-071KL RC0402N_YAG v096"
  Group = -> [Part__Feature101,Part__Feature102,Part__Feature103]
  Origin = -> Origin075
FEATURE [App::Part] RC0402FR_071KL_RC0402N_YAG_v025  label="RC0402FR-071KL RC0402N_YAG v100"
  Group = -> [Part__Feature104,Part__Feature105,Part__Feature106]
  Origin = -> Origin076
FEATURE [App::Part] RC0402FR_071KL_RC0402N_YAG_v026  label="RC0402FR-071KL RC0402N_YAG v104"
  Group = -> [Part__Feature107,Part__Feature108,Part__Feature109]
  Origin = -> Origin077
FEATURE [App::Part] RC0402FR_071KL_RC0402N_YAG_v027  label="RC0402FR-071KL RC0402N_YAG v108"
  Group = -> [Part__Feature110,Part__Feature111,Part__Feature112]
  Origin = -> Origin078
FEATURE [App::Part] RC0402FR_071KL_RC0402N_YAG_v1  label="RC0402FR-071KL RC0402N_YAG v004"
  Group = -> [Part__Feature442,Part__Feature443,Part__Feature444]
  Origin = -> Origin054
FEATURE [App::Part] RC0402FR_071KL  label="RC0402FR-071KL"
  Group = -> [RC0402FR_071KL_RC0402N_YAG_v1,RC0402FR_071KL_RC0402N_YAG_v002,RC0402FR_071KL_RC0402N_YAG_v003,RC0402FR_071KL_RC0402N_YAG_v004,RC0402FR_071KL_RC0402N_YAG_v005,RC0402FR_071KL_RC0402N_YAG_v006,RC0402FR_071KL_RC0402N_YAG_v007,RC0402FR_071KL_RC0402N_YAG_v008,RC0402FR_071KL_RC0402N_YAG_v009,RC0402FR_071KL_RC0402N_YAG_v010,RC0402FR_071KL_RC0402N_YAG_v011,RC0402FR_071KL_RC0402N_YAG_v012,+15 more]
  Origin = -> Origin079
FEATURE [Sketcher::SketchObject] Sketch030
  ArcFitTolerance = 1e-06
  FullyConstrained = true
  MakeInternals = false
  sketch-geometry (8):
    g0: LineSegment StartX=-5 StartY=15 StartZ=0 EndX=-5 EndY=-12 EndZ=0
    g1: LineSegment StartX=-5 StartY=-12 StartZ=0 EndX=48 EndY=-12 EndZ=0
    g2: LineSegment StartX=48 StartY=-12 StartZ=0 EndX=48 EndY=15 EndZ=0
    g3: LineSegment StartX=48 StartY=15 StartZ=0 EndX=-5 EndY=15 EndZ=0
    g4: Circle CenterX=1.275 CenterY=8.5 CenterZ=0 NormalX=0 NormalY=0 NormalZ=1 AngleXU=0 Radius=1
    g5: Circle CenterX=1.275 CenterY=-6.725 CenterZ=0 NormalX=0 NormalY=0 NormalZ=1 AngleXU=0 Radius=1
    g6: Circle CenterX=41.91 CenterY=8.5 CenterZ=0 NormalX=0 NormalY=0 NormalZ=1 AngleXU=0 Radius=1
    g7: Circle CenterX=41.91 CenterY=-6.725 CenterZ=0 NormalX=0 NormalY=0 NormalZ=1 AngleXU=0 Radius=1
  constraints (24):
    c: Vertical(g0)
    c: Coincident(g1,g0)
    c: Horizontal(g1)
    c: Coincident(g2,g1)
    c: Vertical(g2)
    c: Coincident(g3,g2)
    c: Coincident(g3,g0)
    c: Horizontal(g3)
    c: Distance(g0,g-1) = 12
    c: Distance(g-1,g0) = 5
    c: Distance(g0,g-1) = 15
    c: Distance(g2,g-2) = 48
    c: Equal(g4,g5)
    c: Equal(g4,g6)
    c: Equal(g4,g7)
    c: Diameter(g4) = 2
    c: Distance(g4,g-1) = 8.5
    c: Distance(g4,g0) = 6.275
    c: Distance(g5,g0) = 6.275
    c: Distance(g7,g-2) = 41.91
    c: Distance(g6,g-2) = 41.91
    c: Distance(g6,g-1) = 8.5
    c: Distance(g5,g-1) = 6.725
    c: Distance(g7,g-1) = 6.725
FEATURE [Part::Extrusion] Extrude029  label="arduinoHold"
  Base = -> Sketch030
  Dir = (0,0,1)
  DirMode = 2
  FaceMakerClass = Part::FaceMakerBullseye
  FaceMakerMode = 3
  LengthFwd = 3
  LengthRev = 0
  Reversed = true
  Solid = true
  Symmetric = false
FEATURE [Sketcher::SketchObject] Sketch031
  ArcFitTolerance = 0
  FullyConstrained = true
  MakeInternals = false
  sketch-geometry (29):
    g0: LineSegment StartX=0 StartY=0 StartZ=0 EndX=8 EndY=2e-16 EndZ=0
    g1: LineSegment StartX=12 StartY=0 StartZ=0 EndX=28 EndY=2e-16 EndZ=0
    g2: LineSegment StartX=0 StartY=0 StartZ=0 EndX=-4e-16 EndY=8 EndZ=0
    g3: LineSegment StartX=1e-16 StartY=52 StartZ=0 EndX=0 EndY=60 EndZ=0
    g4: LineSegment StartX=0 StartY=60 StartZ=0 EndX=8 EndY=60 EndZ=0
    g5: LineSegment StartX=12 StartY=60 StartZ=0 EndX=28 EndY=60 EndZ=0
    g6: LineSegment StartX=32 StartY=60 StartZ=0 EndX=40 EndY=60 EndZ=0
    g7: LineSegment StartX=40 StartY=60 StartZ=0 EndX=40 EndY=52 EndZ=0
    g8: LineSegment StartX=40 StartY=48 StartZ=0 EndX=40 EndY=32 EndZ=0
    g9: LineSegment StartX=40 StartY=28 StartZ=0 EndX=40 EndY=12 EndZ=0
    g10: LineSegment StartX=40 StartY=8 StartZ=0 EndX=40 EndY=0 EndZ=0
    g11: LineSegment StartX=40 StartY=0 StartZ=0 EndX=32 EndY=-5e-16 EndZ=0
    g12: LineSegment StartX=-4e-16 StartY=48 StartZ=0 EndX=6e-16 EndY=32 EndZ=0
    g13: LineSegment StartX=-4e-16 StartY=28 StartZ=0 EndX=1e-16 EndY=12 EndZ=0
    g14: ArcOfCircle CenterX=10 CenterY=0 CenterZ=0 NormalX=0 NormalY=0 NormalZ=1 AngleXU=0 Radius=2 StartAngle=0 EndAngle=3.14159
    g15: ArcOfCircle CenterX=30 CenterY=0 CenterZ=0 NormalX=0 NormalY=0 NormalZ=1 AngleXU=0 Radius=2 StartAngle=3.14159 EndAngle=6.28319
    g16: ArcOfCircle CenterX=0 CenterY=10 CenterZ=0 NormalX=0 NormalY=0 NormalZ=1 AngleXU=0 Radius=2 StartAngle=1.5708 EndAngle=4.71239
    g17: ArcOfCircle CenterX=0 CenterY=30 CenterZ=0 NormalX=0 NormalY=0 NormalZ=1 AngleXU=0 Radius=2 StartAngle=4.71239 EndAngle=7.85398
    g18: ArcOfCircle CenterX=0 CenterY=50 CenterZ=0 NormalX=0 NormalY=0 NormalZ=1 AngleXU=0 Radius=2 StartAngle=1.5708 EndAngle=4.71239
    g19: ArcOfCircle CenterX=10 CenterY=60 CenterZ=0 NormalX=0 NormalY=0 NormalZ=1 AngleXU=0 Radius=2 StartAngle=3.14159 EndAngle=6.28319
    g20: ArcOfCircle CenterX=30 CenterY=60 CenterZ=0 NormalX=0 NormalY=0 NormalZ=1 AngleXU=0 Radius=2 StartAngle=4e-16 EndAngle=3.14159
    g21: ArcOfCircle CenterX=40 CenterY=50 CenterZ=0 NormalX=0 NormalY=0 NormalZ=1 AngleXU=0 Radius=2 StartAngle=1.5708 EndAngle=4.71239
    g22: ArcOfCircle CenterX=40 CenterY=30 CenterZ=0 NormalX=0 NormalY=0 NormalZ=1 AngleXU=0 Radius=2 StartAngle=4.71239 EndAngle=7.85398
    g23: ArcOfCircle CenterX=40 CenterY=10 CenterZ=0 NormalX=0 NormalY=0 NormalZ=1 AngleXU=0 Radius=2 StartAngle=1.5708 EndAngle=4.71239
    g24: Circle CenterX=30 CenterY=0 CenterZ=0 NormalX=0 NormalY=0 NormalZ=1 AngleXU=0 Radius=1
    g25: Circle CenterX=40 CenterY=30 CenterZ=0 NormalX=0 NormalY=0 NormalZ=1 AngleXU=0 Radius=1
    g26: Circle CenterX=30 CenterY=60 CenterZ=0 NormalX=0 NormalY=0 NormalZ=1 AngleXU=0 Radius=1
    g27: Circle CenterX=0 CenterY=50 CenterZ=0 NormalX=0 NormalY=0 NormalZ=1 AngleXU=0 Radius=1
    g28: Circle CenterX=0 CenterY=10 CenterZ=0 NormalX=0 NormalY=0 NormalZ=1 AngleXU=0 Radius=1
  constraints (88):
    c: Coincident(g0,g-1)
    c: PointOnObject(g0,g-1)
    c: PointOnObject(g1,g-1)
    c: PointOnObject(g1,g-1)
    c: Coincident(g2,g0)
    c: PointOnObject(g2,g-2)
    c: PointOnObject(g3,g-2)
    c: PointOnObject(g3,g-2)
    c: Coincident(g4,g3)
    c: Horizontal(g4)
    c: Horizontal(g5)
    c: Coincident(g7,g6)
    c: Vertical(g7)
    c: Vertical(g8)
    c: Vertical(g9)
    c: PointOnObject(g10,g-1)
    c: Coincident(g11,g10)
    c: PointOnObject(g11,g-1)
    c: PointOnObject(g12,g-2)
    c: PointOnObject(g12,g-2)
    c: PointOnObject(g13,g-2)
    c: PointOnObject(g13,g-2)
    c: Distance(g0) = 8
    c: Coincident(g14,g0)
    c: Coincident(g14,g1)
    c: Diameter(g14) = 4
    c: Distance(g1) = 16
    c: Coincident(g15,g1)
    c: Coincident(g15,g11)
    c: Diameter(g15) = 4
    c: PointOnObject(g15,g-1)
    c: Distance(g11) = 8
    c: Vertical(g10)
    c: Distance(g2) = 8
    c: Coincident(g16,g2)
    c: Coincident(g16,g13)
    c: PointOnObject(g16,g-2)
    c: Diameter(g16) = 4
    c: Distance(g13) = 16
    c: Distance(g12) = 16
    c: PointOnObject(g14,g-1)
    c: Coincident(g17,g13)
    c: Coincident(g17,g12)
    c: PointOnObject(g17,g-2)
    c: Diameter(g17) = 4
    c: Coincident(g18,g12)
    c: Coincident(g18,g3)
    c: PointOnObject(g18,g-2)
    c: Diameter(g18) = 4
    c: Distance(g3) = 8
    c: Distance(g4) = 8
    c: Coincident(g19,g4)
    c: Coincident(g19,g5)
    c: Distance(g19,g-1) = 60
    c: Diameter(g19) = 4
    c: Distance(g5) = 16
    c: Distance(g3,g5) = 12
    c: Coincident(g20,g5)
    c: Coincident(g20,g6)
    c: Distance(g20,g-1) = 60
    c: Diameter(g20) = 4
    c: Distance(g6,g-1) = 60
    c: Horizontal(g6)
    c: Distance(g6) = 8
    c: Distance(g7) = 8
    c: Coincident(g21,g7)
    c: Coincident(g21,g8)
    c: Distance(g18,g21) = 40
    c: Distance(g8) = 16
    c: Diameter(g21) = 4
    c: Distance(g8,g-2) = 40
    c: Distance(g9) = 16
    c: Distance(g9,g-2) = 40
    c: Coincident(g22,g8)
    c: Coincident(g22,g9)
    c: Diameter(g22) = 4
    c: Distance(g22,g17) = 40
    c: Coincident(g23,g9)
    c: Coincident(g23,g10)
    c: Diameter(g23) = 4
    c: Distance(g16,g23) = 40
    c: Coincident(g24,g15)
    c: Coincident(g25,g22)
    c: Coincident(g26,g20)
    c: Coincident(g27,g18)
    c: Coincident(g28,g16)
    c: Equal(g24, g25-g28) x4
    c: Diameter(g24) = 2
FEATURE [Part::Extrusion] Extrude030
  Base = -> Sketch031
  Dir = (0,0,1)
  DirMode = 2
  FaceMakerClass = Part::FaceMakerBullseye
  FaceMakerMode = 3
  LengthFwd = 1.5
  LengthRev = 0
  Solid = true
  Symmetric = false
FEATURE [App::Part] Part001  label="SSR"
  Group = -> [Sketch031,Extrude030,Box065,Box064,Box066,Box067,Fusion043,Box070,Box068,Box069,Box071,Fusion044,Part__Feature521,Part__Feature522,Part__Feature222,Part__Feature221,Part__Feature223,Fusion045]
  Origin = -> Origin089
  Placement = pos=(-17,-16,-6) rot=(-0.57735,-0.57735,0.57735;4.18879rad)
FEATURE [Sketcher::SketchObject] Sketch032
  ArcFitTolerance = 0
  FullyConstrained = true
  MakeInternals = false
  sketch-geometry (29):
    g0: LineSegment StartX=0 StartY=0 StartZ=0 EndX=8 EndY=2e-16 EndZ=0
    g1: LineSegment StartX=12 StartY=0 StartZ=0 EndX=28 EndY=2e-16 EndZ=0
    g2: LineSegment StartX=0 StartY=0 StartZ=0 EndX=-4e-16 EndY=8 EndZ=0
    g3: LineSegment StartX=1e-16 StartY=52 StartZ=0 EndX=0 EndY=60 EndZ=0
    g4: LineSegment StartX=0 StartY=60 StartZ=0 EndX=8 EndY=60 EndZ=0
    g5: LineSegment StartX=12 StartY=60 StartZ=0 EndX=28 EndY=60 EndZ=0
    g6: LineSegment StartX=32 StartY=60 StartZ=0 EndX=40 EndY=60 EndZ=0
    g7: LineSegment StartX=40 StartY=60 StartZ=0 EndX=40 EndY=52 EndZ=0
    g8: LineSegment StartX=40 StartY=48 StartZ=0 EndX=40 EndY=32 EndZ=0
    g9: LineSegment StartX=40 StartY=28 StartZ=0 EndX=40 EndY=12 EndZ=0
    g10: LineSegment StartX=40 StartY=8 StartZ=0 EndX=40 EndY=0 EndZ=0
    g11: LineSegment StartX=40 StartY=0 StartZ=0 EndX=32 EndY=-5e-16 EndZ=0
    g12: LineSegment StartX=-4e-16 StartY=48 StartZ=0 EndX=6e-16 EndY=32 EndZ=0
    g13: LineSegment StartX=-4e-16 StartY=28 StartZ=0 EndX=1e-16 EndY=12 EndZ=0
    g14: ArcOfCircle CenterX=10 CenterY=0 CenterZ=0 NormalX=0 NormalY=0 NormalZ=1 AngleXU=0 Radius=2 StartAngle=0 EndAngle=3.14159
    g15: ArcOfCircle CenterX=30 CenterY=0 CenterZ=0 NormalX=0 NormalY=0 NormalZ=1 AngleXU=0 Radius=2 StartAngle=3.14159 EndAngle=6.28319
    g16: ArcOfCircle CenterX=0 CenterY=10 CenterZ=0 NormalX=0 NormalY=0 NormalZ=1 AngleXU=0 Radius=2 StartAngle=1.5708 EndAngle=4.71239
    g17: ArcOfCircle CenterX=0 CenterY=30 CenterZ=0 NormalX=0 NormalY=0 NormalZ=1 AngleXU=0 Radius=2 StartAngle=4.71239 EndAngle=7.85398
    g18: ArcOfCircle CenterX=0 CenterY=50 CenterZ=0 NormalX=0 NormalY=0 NormalZ=1 AngleXU=0 Radius=2 StartAngle=1.5708 EndAngle=4.71239
    g19: ArcOfCircle CenterX=10 CenterY=60 CenterZ=0 NormalX=0 NormalY=0 NormalZ=1 AngleXU=0 Radius=2 StartAngle=3.14159 EndAngle=6.28319
    g20: ArcOfCircle CenterX=30 CenterY=60 CenterZ=0 NormalX=0 NormalY=0 NormalZ=1 AngleXU=0 Radius=2 StartAngle=4e-16 EndAngle=3.14159
    g21: ArcOfCircle CenterX=40 CenterY=50 CenterZ=0 NormalX=0 NormalY=0 NormalZ=1 AngleXU=0 Radius=2 StartAngle=1.5708 EndAngle=4.71239
    g22: ArcOfCircle CenterX=40 CenterY=30 CenterZ=0 NormalX=0 NormalY=0 NormalZ=1 AngleXU=0 Radius=2 StartAngle=4.71239 EndAngle=7.85398
    g23: ArcOfCircle CenterX=40 CenterY=10 CenterZ=0 NormalX=0 NormalY=0 NormalZ=1 AngleXU=0 Radius=2 StartAngle=1.5708 EndAngle=4.71239
    g24: Circle CenterX=30 CenterY=0 CenterZ=0 NormalX=0 NormalY=0 NormalZ=1 AngleXU=0 Radius=1
    g25: Circle CenterX=40 CenterY=30 CenterZ=0 NormalX=0 NormalY=0 NormalZ=1 AngleXU=0 Radius=1
    g26: Circle CenterX=30 CenterY=60 CenterZ=0 NormalX=0 NormalY=0 NormalZ=1 AngleXU=0 Radius=1
    g27: Circle CenterX=0 CenterY=50 CenterZ=0 NormalX=0 NormalY=0 NormalZ=1 AngleXU=0 Radius=1
    g28: Circle CenterX=0 CenterY=10 CenterZ=0 NormalX=0 NormalY=0 NormalZ=1 AngleXU=0 Radius=1
  constraints (88):
    c: Coincident(g0,g-1)
    c: PointOnObject(g0,g-1)
    c: PointOnObject(g1,g-1)
    c: PointOnObject(g1,g-1)
    c: Coincident(g2,g0)
    c: PointOnObject(g2,g-2)
    c: PointOnObject(g3,g-2)
    c: PointOnObject(g3,g-2)
    c: Coincident(g4,g3)
    c: Horizontal(g4)
    c: Horizontal(g5)
    c: Coincident(g7,g6)
    c: Vertical(g7)
    c: Vertical(g8)
    c: Vertical(g9)
    c: PointOnObject(g10,g-1)
    c: Coincident(g11,g10)
    c: PointOnObject(g11,g-1)
    c: PointOnObject(g12,g-2)
    c: PointOnObject(g12,g-2)
    c: PointOnObject(g13,g-2)
    c: PointOnObject(g13,g-2)
    c: Distance(g0) = 8
    c: Coincident(g14,g0)
    c: Coincident(g14,g1)
    c: Diameter(g14) = 4
    c: Distance(g1) = 16
    c: Coincident(g15,g1)
    c: Coincident(g15,g11)
    c: Diameter(g15) = 4
    c: PointOnObject(g15,g-1)
    c: Distance(g11) = 8
    c: Vertical(g10)
    c: Distance(g2) = 8
    c: Coincident(g16,g2)
    c: Coincident(g16,g13)
    c: PointOnObject(g16,g-2)
    c: Diameter(g16) = 4
    c: Distance(g13) = 16
    c: Distance(g12) = 16
    c: PointOnObject(g14,g-1)
    c: Coincident(g17,g13)
    c: Coincident(g17,g12)
    c: PointOnObject(g17,g-2)
    c: Diameter(g17) = 4
    c: Coincident(g18,g12)
    c: Coincident(g18,g3)
    c: PointOnObject(g18,g-2)
    c: Diameter(g18) = 4
    c: Distance(g3) = 8
    c: Distance(g4) = 8
    c: Coincident(g19,g4)
    c: Coincident(g19,g5)
    c: Distance(g19,g-1) = 60
    c: Diameter(g19) = 4
    c: Distance(g5) = 16
    c: Distance(g3,g5) = 12
    c: Coincident(g20,g5)
    c: Coincident(g20,g6)
    c: Distance(g20,g-1) = 60
    c: Diameter(g20) = 4
    c: Distance(g6,g-1) = 60
    c: Horizontal(g6)
    c: Distance(g6) = 8
    c: Distance(g7) = 8
    c: Coincident(g21,g7)
    c: Coincident(g21,g8)
    c: Distance(g18,g21) = 40
    c: Distance(g8) = 16
    c: Diameter(g21) = 4
    c: Distance(g8,g-2) = 40
    c: Distance(g9) = 16
    c: Distance(g9,g-2) = 40
    c: Coincident(g22,g8)
    c: Coincident(g22,g9)
    c: Diameter(g22) = 4
    c: Distance(g22,g17) = 40
    c: Coincident(g23,g9)
    c: Coincident(g23,g10)
    c: Diameter(g23) = 4
    c: Distance(g16,g23) = 40
    c: Coincident(g24,g15)
    c: Coincident(g25,g22)
    c: Coincident(g26,g20)
    c: Coincident(g27,g18)
    c: Coincident(g28,g16)
    c: Equal(g24, g25-g28) x4
    c: Diameter(g24) = 2
FEATURE [Part::Extrusion] Extrude031
  Base = -> Sketch032
  Dir = (0,0,1)
  DirMode = 2
  FaceMakerClass = Part::FaceMakerBullseye
  FaceMakerMode = 3
  LengthFwd = 5
  LengthRev = 0
  Placement = pos=(-17,-18,0) rot=(-0.57735,-0.57735,0.57735;4.18879rad)
  Solid = true
  Symmetric = false
FEATURE [Sketcher::SketchObject] Sketch033
  ArcFitTolerance = 0
  FullyConstrained = true
  MakeInternals = false
  sketch-geometry (29):
    g0: LineSegment StartX=0 StartY=0 StartZ=0 EndX=8 EndY=2e-16 EndZ=0
    g1: LineSegment StartX=12 StartY=0 StartZ=0 EndX=28 EndY=2e-16 EndZ=0
    g2: LineSegment StartX=0 StartY=0 StartZ=0 EndX=-4e-16 EndY=8 EndZ=0
    g3: LineSegment StartX=1e-16 StartY=52 StartZ=0 EndX=0 EndY=60 EndZ=0
    g4: LineSegment StartX=0 StartY=60 StartZ=0 EndX=8 EndY=60 EndZ=0
    g5: LineSegment StartX=12 StartY=60 StartZ=0 EndX=28 EndY=60 EndZ=0
    g6: LineSegment StartX=32 StartY=60 StartZ=0 EndX=40 EndY=60 EndZ=0
    g7: LineSegment StartX=40 StartY=60 StartZ=0 EndX=40 EndY=52 EndZ=0
    g8: LineSegment StartX=40 StartY=48 StartZ=0 EndX=40 EndY=32 EndZ=0
    g9: LineSegment StartX=40 StartY=28 StartZ=0 EndX=40 EndY=12 EndZ=0
    g10: LineSegment StartX=40 StartY=8 StartZ=0 EndX=40 EndY=0 EndZ=0
    g11: LineSegment StartX=40 StartY=0 StartZ=0 EndX=32 EndY=-5e-16 EndZ=0
    g12: LineSegment StartX=-4e-16 StartY=48 StartZ=0 EndX=6e-16 EndY=32 EndZ=0
    g13: LineSegment StartX=-4e-16 StartY=28 StartZ=0 EndX=1e-16 EndY=12 EndZ=0
    g14: ArcOfCircle CenterX=10 CenterY=0 CenterZ=0 NormalX=0 NormalY=0 NormalZ=1 AngleXU=0 Radius=2 StartAngle=0 EndAngle=3.14159
    g15: ArcOfCircle CenterX=30 CenterY=0 CenterZ=0 NormalX=0 NormalY=0 NormalZ=1 AngleXU=0 Radius=2 StartAngle=3.14159 EndAngle=6.28319
    g16: ArcOfCircle CenterX=0 CenterY=10 CenterZ=0 NormalX=0 NormalY=0 NormalZ=1 AngleXU=0 Radius=2 StartAngle=1.5708 EndAngle=4.71239
    g17: ArcOfCircle CenterX=0 CenterY=30 CenterZ=0 NormalX=0 NormalY=0 NormalZ=1 AngleXU=0 Radius=2 StartAngle=4.71239 EndAngle=7.85398
    g18: ArcOfCircle CenterX=0 CenterY=50 CenterZ=0 NormalX=0 NormalY=0 NormalZ=1 AngleXU=0 Radius=2 StartAngle=1.5708 EndAngle=4.71239
    g19: ArcOfCircle CenterX=10 CenterY=60 CenterZ=0 NormalX=0 NormalY=0 NormalZ=1 AngleXU=0 Radius=2 StartAngle=3.14159 EndAngle=6.28319
    g20: ArcOfCircle CenterX=30 CenterY=60 CenterZ=0 NormalX=0 NormalY=0 NormalZ=1 AngleXU=0 Radius=2 StartAngle=4e-16 EndAngle=3.14159
    g21: ArcOfCircle CenterX=40 CenterY=50 CenterZ=0 NormalX=0 NormalY=0 NormalZ=1 AngleXU=0 Radius=2 StartAngle=1.5708 EndAngle=4.71239
    g22: ArcOfCircle CenterX=40 CenterY=30 CenterZ=0 NormalX=0 NormalY=0 NormalZ=1 AngleXU=0 Radius=2 StartAngle=4.71239 EndAngle=7.85398
    g23: ArcOfCircle CenterX=40 CenterY=10 CenterZ=0 NormalX=0 NormalY=0 NormalZ=1 AngleXU=0 Radius=2 StartAngle=1.5708 EndAngle=4.71239
    g24: Circle CenterX=30 CenterY=0 CenterZ=0 NormalX=0 NormalY=0 NormalZ=1 AngleXU=0 Radius=1
    g25: Circle CenterX=40 CenterY=30 CenterZ=0 NormalX=0 NormalY=0 NormalZ=1 AngleXU=0 Radius=1
    g26: Circle CenterX=30 CenterY=60 CenterZ=0 NormalX=0 NormalY=0 NormalZ=1 AngleXU=0 Radius=1
    g27: Circle CenterX=0 CenterY=50 CenterZ=0 NormalX=0 NormalY=0 NormalZ=1 AngleXU=0 Radius=1
    g28: Circle CenterX=0 CenterY=10 CenterZ=0 NormalX=0 NormalY=0 NormalZ=1 AngleXU=0 Radius=1
  constraints (88):
    c: Coincident(g0,g-1)
    c: PointOnObject(g0,g-1)
    c: PointOnObject(g1,g-1)
    c: PointOnObject(g1,g-1)
    c: Coincident(g2,g0)
    c: PointOnObject(g2,g-2)
    c: PointOnObject(g3,g-2)
    c: PointOnObject(g3,g-2)
    c: Coincident(g4,g3)
    c: Horizontal(g4)
    c: Horizontal(g5)
    c: Coincident(g7,g6)
    c: Vertical(g7)
    c: Vertical(g8)
    c: Vertical(g9)
    c: PointOnObject(g10,g-1)
    c: Coincident(g11,g10)
    c: PointOnObject(g11,g-1)
    c: PointOnObject(g12,g-2)
    c: PointOnObject(g12,g-2)
    c: PointOnObject(g13,g-2)
    c: PointOnObject(g13,g-2)
    c: Distance(g0) = 8
    c: Coincident(g14,g0)
    c: Coincident(g14,g1)
    c: Diameter(g14) = 4
    c: Distance(g1) = 16
    c: Coincident(g15,g1)
    c: Coincident(g15,g11)
    c: Diameter(g15) = 4
    c: PointOnObject(g15,g-1)
    c: Distance(g11) = 8
    c: Vertical(g10)
    c: Distance(g2) = 8
    c: Coincident(g16,g2)
    c: Coincident(g16,g13)
    c: PointOnObject(g16,g-2)
    c: Diameter(g16) = 4
    c: Distance(g13) = 16
    c: Distance(g12) = 16
    c: PointOnObject(g14,g-1)
    c: Coincident(g17,g13)
    c: Coincident(g17,g12)
    c: PointOnObject(g17,g-2)
    c: Diameter(g17) = 4
    c: Coincident(g18,g12)
    c: Coincident(g18,g3)
    c: PointOnObject(g18,g-2)
    c: Diameter(g18) = 4
    c: Distance(g3) = 8
    c: Distance(g4) = 8
    c: Coincident(g19,g4)
    c: Coincident(g19,g5)
    c: Distance(g19,g-1) = 60
    c: Diameter(g19) = 4
    c: Distance(g5) = 16
    c: Distance(g3,g5) = 12
    c: Coincident(g20,g5)
    c: Coincident(g20,g6)
    c: Distance(g20,g-1) = 60
    c: Diameter(g20) = 4
    c: Distance(g6,g-1) = 60
    c: Horizontal(g6)
    c: Distance(g6) = 8
    c: Distance(g7) = 8
    c: Coincident(g21,g7)
    c: Coincident(g21,g8)
    c: Distance(g18,g21) = 40
    c: Distance(g8) = 16
    c: Diameter(g21) = 4
    c: Distance(g8,g-2) = 40
    c: Distance(g9) = 16
    c: Distance(g9,g-2) = 40
    c: Coincident(g22,g8)
    c: Coincident(g22,g9)
    c: Diameter(g22) = 4
    c: Distance(g22,g17) = 40
    c: Coincident(g23,g9)
    c: Coincident(g23,g10)
    c: Diameter(g23) = 4
    c: Distance(g16,g23) = 40
    c: Coincident(g24,g15)
    c: Coincident(g25,g22)
    c: Coincident(g26,g20)
    c: Coincident(g27,g18)
    c: Coincident(g28,g16)
    c: Equal(g24, g25-g28) x4
    c: Diameter(g24) = 2
FEATURE [Part::Extrusion] Extrude032
  Base = -> Sketch033
  Dir = (0,0,1)
  DirMode = 2
  FaceMakerClass = Part::FaceMakerBullseye
  FaceMakerMode = 3
  LengthFwd = 5
  LengthRev = 0
  Placement = pos=(-17,-18,0) rot=(-0.57735,-0.57735,0.57735;4.18879rad)
  Solid = true
  Symmetric = false
FEATURE [Part::Cut] Cut047  label="base_cut"
  Base = -> Box008
  Refine = true
  Tool = -> Extrude032
FEATURE [Part::MultiFuse] Fusion046
  Refine = true
  Shapes = -> [Cut047,Box072,Box073]
FEATURE [Part::MultiFuse] Fusion047  label="ssrHold"
  Placement = pos=(0,7,-6) rot=(0,0,1;0rad)
  Refine = true
  Shapes = -> [Extrude031,Fusion046]
FEATURE [Part::MultiFuse] Fusion048  label="fusedHold"
  Refine = true
  Shapes = -> [Extrude029,Fusion047]
FEATURE [Part::Cut] Cut048  label="ssr_nano_hold"
  Base = -> Fusion048
  Refine = true
  Tool = -> Fusion049
FEATURE [Part::MultiFuse] Fusion051  label="SSR_Nano"
  Refine = true
  Shapes = -> [Cut048,Fusion050]
FEATURE [Part::Fillet] Fillet034
  Base = -> Fusion051
  EdgeLinks = -> Fusion051 [Edge1,Edge2,Edge3,Edge4,Edge5,Edge7,Edge8,Edge9,Edge15,Edge16,Edge17,Edge18,Edge19,Edge21,Edge22,Edge23,Edge28,Edge29,Edge32,Edge33,Edge34,Edge36,Edge37]
  Edges = 23 edges: [Edge1 r=1,Edge2 r=2,Edge3 r=1,Edge4 r=1,Edge5 r=1,Edge7 r=2,Edge8 r=3,Edge9 r=1,Edge15 r=1,Edge16 r=1,Edge17 r=1,Edge18 r=3,Edge19 r=1,Edge21 r=1,Edge22 r=1,Edge23 r=1,Edge28 r=1,Edge29 r=1,Edge32 r=1,Edge33 r=1,Edge34 r=1,Edge36 r=1,Edge37 r=1]
FEATURE [Sketcher::SketchObject] Sketch034
  ArcFitTolerance = 0
  FullyConstrained = true
  MakeInternals = false
  sketch-geometry (24):
    g0: LineSegment StartX=0 StartY=0 StartZ=0 EndX=8 EndY=2e-16 EndZ=0
    g1: LineSegment StartX=12 StartY=0 StartZ=0 EndX=28 EndY=2e-16 EndZ=0
    g2: LineSegment StartX=0 StartY=0 StartZ=0 EndX=-4e-16 EndY=8 EndZ=0
    g3: LineSegment StartX=1e-16 StartY=52 StartZ=0 EndX=0 EndY=60 EndZ=0
    g4: LineSegment StartX=0 StartY=60 StartZ=0 EndX=8 EndY=60 EndZ=0
    g5: LineSegment StartX=12 StartY=60 StartZ=0 EndX=28 EndY=60 EndZ=0
    g6: LineSegment StartX=32 StartY=60 StartZ=0 EndX=40 EndY=60 EndZ=0
    g7: LineSegment StartX=40 StartY=60 StartZ=0 EndX=40 EndY=52 EndZ=0
    g8: LineSegment StartX=40 StartY=48 StartZ=0 EndX=40 EndY=32 EndZ=0
    g9: LineSegment StartX=40 StartY=28 StartZ=0 EndX=40 EndY=12 EndZ=0
    g10: LineSegment StartX=40 StartY=8 StartZ=0 EndX=40 EndY=0 EndZ=0
    g11: LineSegment StartX=40 StartY=0 StartZ=0 EndX=32 EndY=-5e-16 EndZ=0
    g12: LineSegment StartX=-4e-16 StartY=48 StartZ=0 EndX=6e-16 EndY=32 EndZ=0
    g13: LineSegment StartX=-4e-16 StartY=28 StartZ=0 EndX=1e-16 EndY=12 EndZ=0
    g14: ArcOfCircle CenterX=10 CenterY=0 CenterZ=0 NormalX=0 NormalY=0 NormalZ=1 AngleXU=0 Radius=2 StartAngle=0 EndAngle=3.14159
    g15: ArcOfCircle CenterX=30 CenterY=0 CenterZ=0 NormalX=0 NormalY=0 NormalZ=1 AngleXU=0 Radius=2 StartAngle=3.14159 EndAngle=6.28319
    g16: ArcOfCircle CenterX=0 CenterY=10 CenterZ=0 NormalX=0 NormalY=0 NormalZ=1 AngleXU=0 Radius=2 StartAngle=1.5708 EndAngle=4.71239
    g17: ArcOfCircle CenterX=0 CenterY=30 CenterZ=0 NormalX=0 NormalY=0 NormalZ=1 AngleXU=0 Radius=2 StartAngle=4.71239 EndAngle=7.85398
    g18: ArcOfCircle CenterX=0 CenterY=50 CenterZ=0 NormalX=0 NormalY=0 NormalZ=1 AngleXU=0 Radius=2 StartAngle=1.5708 EndAngle=4.71239
    g19: ArcOfCircle CenterX=10 CenterY=60 CenterZ=0 NormalX=0 NormalY=0 NormalZ=1 AngleXU=0 Radius=2 StartAngle=3.14159 EndAngle=6.28319
    g20: ArcOfCircle CenterX=30 CenterY=60 CenterZ=0 NormalX=0 NormalY=0 NormalZ=1 AngleXU=0 Radius=2 StartAngle=4e-16 EndAngle=3.14159
    g21: ArcOfCircle CenterX=40 CenterY=50 CenterZ=0 NormalX=0 NormalY=0 NormalZ=1 AngleXU=0 Radius=2 StartAngle=1.5708 EndAngle=4.71239
    g22: ArcOfCircle CenterX=40 CenterY=30 CenterZ=0 NormalX=0 NormalY=0 NormalZ=1 AngleXU=0 Radius=2 StartAngle=4.71239 EndAngle=7.85398
    g23: ArcOfCircle CenterX=40 CenterY=10 CenterZ=0 NormalX=0 NormalY=0 NormalZ=1 AngleXU=0 Radius=2 StartAngle=1.5708 EndAngle=4.71239
  constraints (81):
    c: Coincident(g0,g-1)
    c: PointOnObject(g0,g-1)
    c: PointOnObject(g1,g-1)
    c: PointOnObject(g1,g-1)
    c: Coincident(g2,g0)
    c: PointOnObject(g2,g-2)
    c: PointOnObject(g3,g-2)
    c: PointOnObject(g3,g-2)
    c: Coincident(g4,g3)
    c: Horizontal(g4)
    c: Horizontal(g5)
    c: Coincident(g7,g6)
    c: Vertical(g7)
    c: Vertical(g8)
    c: Vertical(g9)
    c: PointOnObject(g10,g-1)
    c: Coincident(g11,g10)
    c: PointOnObject(g11,g-1)
    c: PointOnObject(g12,g-2)
    c: PointOnObject(g12,g-2)
    c: PointOnObject(g13,g-2)
    c: PointOnObject(g13,g-2)
    c: Distance(g0) = 8
    c: Coincident(g14,g0)
    c: Coincident(g14,g1)
    c: Diameter(g14) = 4
    c: Distance(g1) = 16
    c: Coincident(g15,g1)
    c: Coincident(g15,g11)
    c: Diameter(g15) = 4
    c: PointOnObject(g15,g-1)
    c: Distance(g11) = 8
    c: Vertical(g10)
    c: Distance(g2) = 8
    c: Coincident(g16,g2)
    c: Coincident(g16,g13)
    c: PointOnObject(g16,g-2)
    c: Diameter(g16) = 4
    c: Distance(g13) = 16
    c: Distance(g12) = 16
    c: PointOnObject(g14,g-1)
    c: Coincident(g17,g13)
    c: Coincident(g17,g12)
    c: PointOnObject(g17,g-2)
    c: Diameter(g17) = 4
    c: Coincident(g18,g12)
    c: Coincident(g18,g3)
    c: PointOnObject(g18,g-2)
    c: Diameter(g18) = 4
    c: Distance(g3) = 8
    c: Distance(g4) = 8
    c: Coincident(g19,g4)
    c: Coincident(g19,g5)
    c: Distance(g19,g-1) = 60
    c: Diameter(g19) = 4
    c: Distance(g5) = 16
    c: Distance(g3,g5) = 12
    c: Coincident(g20,g5)
    c: Coincident(g20,g6)
    c: Distance(g20,g-1) = 60
    c: Diameter(g20) = 4
    c: Distance(g6,g-1) = 60
    c: Horizontal(g6)
    c: Distance(g6) = 8
    c: Distance(g7) = 8
    c: Coincident(g21,g7)
    c: Coincident(g21,g8)
    c: Distance(g18,g21) = 40
    c: Distance(g8) = 16
    c: Diameter(g21) = 4
    c: Distance(g8,g-2) = 40
    c: Distance(g9) = 16
    c: Distance(g9,g-2) = 40
    c: Coincident(g22,g8)
    c: Coincident(g22,g9)
    c: Diameter(g22) = 4
    c: Distance(g22,g17) = 40
    c: Coincident(g23,g9)
    c: Coincident(g23,g10)
    c: Diameter(g23) = 4
    c: Distance(g16,g23) = 40
FEATURE [Part::Extrusion] Extrude033
  Base = -> Sketch034
  Dir = (0,0,1)
  DirMode = 2
  FaceMakerClass = Part::FaceMakerBullseye
  FaceMakerMode = 3
  LengthFwd = 5
  LengthRev = 0
  Placement = pos=(-17,-11,-6) rot=(-0.57735,-0.57735,0.57735;4.18879rad)
  Solid = true
  Symmetric = false
FEATURE [Part::Cut] Cut049  label="Base_cut"
  Base = -> Fillet034
  Refine = true
  Tool = -> Extrude033
FEATURE [Sketcher::SketchObject] Sketch035
  ArcFitTolerance = 0
  FullyConstrained = true
  MakeInternals = false
  sketch-geometry (29):
    g0: LineSegment StartX=0 StartY=0 StartZ=0 EndX=8 EndY=2e-16 EndZ=0
    g1: LineSegment StartX=12 StartY=0 StartZ=0 EndX=28 EndY=2e-16 EndZ=0
    g2: LineSegment StartX=0 StartY=0 StartZ=0 EndX=-4e-16 EndY=8 EndZ=0
    g3: LineSegment StartX=1e-16 StartY=52 StartZ=0 EndX=0 EndY=60 EndZ=0
    g4: LineSegment StartX=0 StartY=60 StartZ=0 EndX=8 EndY=60 EndZ=0
    g5: LineSegment StartX=12 StartY=60 StartZ=0 EndX=28 EndY=60 EndZ=0
    g6: LineSegment StartX=32 StartY=60 StartZ=0 EndX=40 EndY=60 EndZ=0
    g7: LineSegment StartX=40 StartY=60 StartZ=0 EndX=40 EndY=52 EndZ=0
    g8: LineSegment StartX=40 StartY=48 StartZ=0 EndX=40 EndY=32 EndZ=0
    g9: LineSegment StartX=40 StartY=28 StartZ=0 EndX=40 EndY=12 EndZ=0
    g10: LineSegment StartX=40 StartY=8 StartZ=0 EndX=40 EndY=0 EndZ=0
    g11: LineSegment StartX=40 StartY=0 StartZ=0 EndX=32 EndY=-5e-16 EndZ=0
    g12: LineSegment StartX=-4e-16 StartY=48 StartZ=0 EndX=6e-16 EndY=32 EndZ=0
    g13: LineSegment StartX=-4e-16 StartY=28 StartZ=0 EndX=1e-16 EndY=12 EndZ=0
    g14: ArcOfCircle CenterX=10 CenterY=0 CenterZ=0 NormalX=0 NormalY=0 NormalZ=1 AngleXU=0 Radius=2 StartAngle=0 EndAngle=3.14159
    g15: ArcOfCircle CenterX=30 CenterY=0 CenterZ=0 NormalX=0 NormalY=0 NormalZ=1 AngleXU=0 Radius=2 StartAngle=3.14159 EndAngle=6.28319
    g16: ArcOfCircle CenterX=0 CenterY=10 CenterZ=0 NormalX=0 NormalY=0 NormalZ=1 AngleXU=0 Radius=2 StartAngle=1.5708 EndAngle=4.71239
    g17: ArcOfCircle CenterX=0 CenterY=30 CenterZ=0 NormalX=0 NormalY=0 NormalZ=1 AngleXU=0 Radius=2 StartAngle=4.71239 EndAngle=7.85398
    g18: ArcOfCircle CenterX=0 CenterY=50 CenterZ=0 NormalX=0 NormalY=0 NormalZ=1 AngleXU=0 Radius=2 StartAngle=1.5708 EndAngle=4.71239
    g19: ArcOfCircle CenterX=10 CenterY=60 CenterZ=0 NormalX=0 NormalY=0 NormalZ=1 AngleXU=0 Radius=2 StartAngle=3.14159 EndAngle=6.28319
    g20: ArcOfCircle CenterX=30 CenterY=60 CenterZ=0 NormalX=0 NormalY=0 NormalZ=1 AngleXU=0 Radius=2 StartAngle=4e-16 EndAngle=3.14159
    g21: ArcOfCircle CenterX=40 CenterY=50 CenterZ=0 NormalX=0 NormalY=0 NormalZ=1 AngleXU=0 Radius=2 StartAngle=1.5708 EndAngle=4.71239
    g22: ArcOfCircle CenterX=40 CenterY=30 CenterZ=0 NormalX=0 NormalY=0 NormalZ=1 AngleXU=0 Radius=2 StartAngle=4.71239 EndAngle=7.85398
    g23: ArcOfCircle CenterX=40 CenterY=10 CenterZ=0 NormalX=0 NormalY=0 NormalZ=1 AngleXU=0 Radius=2 StartAngle=1.5708 EndAngle=4.71239
    g24: Circle CenterX=30 CenterY=0 CenterZ=0 NormalX=0 NormalY=0 NormalZ=1 AngleXU=0 Radius=1
    g25: Circle CenterX=40 CenterY=30 CenterZ=0 NormalX=0 NormalY=0 NormalZ=1 AngleXU=0 Radius=1
    g26: Circle CenterX=30 CenterY=60 CenterZ=0 NormalX=0 NormalY=0 NormalZ=1 AngleXU=0 Radius=1
    g27: Circle CenterX=0 CenterY=50 CenterZ=0 NormalX=0 NormalY=0 NormalZ=1 AngleXU=0 Radius=1
    g28: Circle CenterX=0 CenterY=10 CenterZ=0 NormalX=0 NormalY=0 NormalZ=1 AngleXU=0 Radius=1
  constraints (88):
    c: Coincident(g0,g-1)
    c: PointOnObject(g0,g-1)
    c: PointOnObject(g1,g-1)
    c: PointOnObject(g1,g-1)
    c: Coincident(g2,g0)
    c: PointOnObject(g2,g-2)
    c: PointOnObject(g3,g-2)
    c: PointOnObject(g3,g-2)
    c: Coincident(g4,g3)
    c: Horizontal(g4)
    c: Horizontal(g5)
    c: Coincident(g7,g6)
    c: Vertical(g7)
    c: Vertical(g8)
    c: Vertical(g9)
    c: PointOnObject(g10,g-1)
    c: Coincident(g11,g10)
    c: PointOnObject(g11,g-1)
    c: PointOnObject(g12,g-2)
    c: PointOnObject(g12,g-2)
    c: PointOnObject(g13,g-2)
    c: PointOnObject(g13,g-2)
    c: Distance(g0) = 8
    c: Coincident(g14,g0)
    c: Coincident(g14,g1)
    c: Diameter(g14) = 4
    c: Distance(g1) = 16
    c: Coincident(g15,g1)
    c: Coincident(g15,g11)
    c: Diameter(g15) = 4
    c: PointOnObject(g15,g-1)
    c: Distance(g11) = 8
    c: Vertical(g10)
    c: Distance(g2) = 8
    c: Coincident(g16,g2)
    c: Coincident(g16,g13)
    c: PointOnObject(g16,g-2)
    c: Diameter(g16) = 4
    c: Distance(g13) = 16
    c: Distance(g12) = 16
    c: PointOnObject(g14,g-1)
    c: Coincident(g17,g13)
    c: Coincident(g17,g12)
    c: PointOnObject(g17,g-2)
    c: Diameter(g17) = 4
    c: Coincident(g18,g12)
    c: Coincident(g18,g3)
    c: PointOnObject(g18,g-2)
    c: Diameter(g18) = 4
    c: Distance(g3) = 8
    c: Distance(g4) = 8
    c: Coincident(g19,g4)
    c: Coincident(g19,g5)
    c: Distance(g19,g-1) = 60
    c: Diameter(g19) = 4
    c: Distance(g5) = 16
    c: Distance(g3,g5) = 12
    c: Coincident(g20,g5)
    c: Coincident(g20,g6)
    c: Distance(g20,g-1) = 60
    c: Diameter(g20) = 4
    c: Distance(g6,g-1) = 60
    c: Horizontal(g6)
    c: Distance(g6) = 8
    c: Distance(g7) = 8
    c: Coincident(g21,g7)
    c: Coincident(g21,g8)
    c: Distance(g18,g21) = 40
    c: Distance(g8) = 16
    c: Diameter(g21) = 4
    c: Distance(g8,g-2) = 40
    c: Distance(g9) = 16
    c: Distance(g9,g-2) = 40
    c: Coincident(g22,g8)
    c: Coincident(g22,g9)
    c: Diameter(g22) = 4
    c: Distance(g22,g17) = 40
    c: Coincident(g23,g9)
    c: Coincident(g23,g10)
    c: Diameter(g23) = 4
    c: Distance(g16,g23) = 40
    c: Coincident(g24,g15)
    c: Coincident(g25,g22)
    c: Coincident(g26,g20)
    c: Coincident(g27,g18)
    c: Coincident(g28,g16)
    c: Equal(g24, g25-g28) x4
    c: Diameter(g24) = 2
FEATURE [Part::Extrusion] Extrude034
  Base = -> Sketch035
  Dir = (0,0,1)
  DirMode = 2
  FaceMakerClass = Part::FaceMakerBullseye
  FaceMakerMode = 3
  LengthFwd = 5
  LengthRev = 0
  Placement = pos=(-17,-11,-6) rot=(-0.57735,-0.57735,0.57735;4.18879rad)
  Solid = true
  Symmetric = false
FEATURE [Part::MultiFuse] Fusion052  label="Arduino_SSR_Hold"
  Refine = true
  Shapes = -> [Cut049,Extrude034]
FEATURE [Part::Cut] Cut050  label="arduinoNano33Holder"
  Base = -> Fusion052
  Tool = -> Cylinder065
FEATURE [App::Part] _850961  label="6850961"
  Group = -> [Part__Feature437]
  Origin = -> Origin001
FEATURE [App::Part] zx62_ab_5pa_31__v1  label="zx62-ab-5pa_31_ v1"
  Group = -> [_850961]
  Origin = -> Origin052
  Placement = pos=(0,0,0) rot=(0,0.707107,0.707107;3.14159rad)
FEATURE [App::Part] _DComponents  label="3DComponents"
  Group = -> [LSM9DS1TR_LGA_24_3X3P5X1_STM_v1,zx62_ab_5pa_31__v1,Part__Feature438,Part__Feature439,IoT_Reser_Button_v1,RC0402FR_071KL,Part__Feature113,BLM18EG101TN1D_v1,C0805C472KDRACTU_v1,C0805C472KDRACTU_v002,PMEG6020AELRX_v1,C0805C472KDRACTU_v003,Part__Feature130,NINA_B306_00B_00__3DModel_STEP_56544_v1]
  Origin = -> Origin086
FEATURE [App::Part] NANO33BLE_V2_0_v1  label="NANO33BLE_V2.0 v1"
  Group = -> [Part__Feature410,_DComponents]
  Origin = -> Origin039
FEATURE [App::Part] Nano33BLE_v7  label="Nano33BLE v7"
  Group = -> [NANO33BLE_V2_0_v1]
  Origin = -> Origin087
  Placement = pos=(0,-8,0) rot=(0,0,1;0rad)
FEATURE [Part::Compound] Compound007  label="arduinoNano33"
  Links = -> [Cut050,Part001,Part,Nano33BLE_v7,Origin088]
  Placement = pos=(85,105,0) rot=(0.57735,-0.57735,0.57735;2.0944rad)
FEATURE [Part::Cylinder] Cylinder070
  Angle = 360
  AttacherType = Attacher::AttachEngine3D
  FirstAngle = 0
  Height = 3.7
  Placement = pos=(176.78,-4,-14) rot=(0,0,1;0rad)
  Radius = 3
  SecondAngle = 0
FEATURE [Part::Cylinder] Cylinder071
  Angle = 360
  AttacherType = Attacher::AttachEngine3D
  FirstAngle = 0
  Height = 3.7
  Placement = pos=(195.78,-4,-14) rot=(0,0,1;0rad)
  Radius = 3
  SecondAngle = 0
FEATURE [Part::Cylinder] Cylinder072
  Angle = 360
  AttacherType = Attacher::AttachEngine3D
  FirstAngle = 0
  Height = 3.7
  Placement = pos=(195.78,-30,-14) rot=(0,0,1;0rad)
  Radius = 3
  SecondAngle = 0
FEATURE [Part::Cylinder] Cylinder073
  Angle = 360
  AttacherType = Attacher::AttachEngine3D
  FirstAngle = 0
  Height = 3.7
  Placement = pos=(176.78,-30,-14) rot=(0,0,1;0rad)
  Radius = 3
  SecondAngle = 0
FEATURE [Part::MultiFuse] Fusion054  label="m3_head001"
  Refine = true
  Shapes = -> [Cylinder070,Cylinder071,Cylinder072,Cylinder073]
FEATURE [Part::Feature] Part__Feature533  label="051659-8_05358-PUMPE-_SW0001"
  shape: bbox 32.37 x 50.78 x 84.45 mm, 991 faces (baked)
FEATURE [Part::Feature] Part__Feature534  label="051659-8_05358-PUMPE-_SW0002"
  shape: bbox 4 x 4 x 0.751 mm, 31 faces (baked)
FEATURE [Part::Feature] Part__Feature535  label="051659-8_05358-PUMPE-_SW0003"
  shape: bbox 4 x 4 x 0.751 mm, 31 faces (baked)
FEATURE [Part::Feature] Part__Feature536  label="051659-8_05358-PUMPE-_SW0004"
  shape: bbox 4 x 4 x 0.751 mm, 31 faces (baked)
FEATURE [Part::Feature] Part__Feature537  label="051659-8_05358-PUMPE-_SW0005"
  shape: bbox 4 x 4 x 0.751 mm, 31 faces (baked)
FEATURE [Sketcher::SketchObject] Sketch037
  ArcFitTolerance = 1e-06
  FullyConstrained = true
  MakeInternals = false
  sketch-geometry (12):
    g0: LineSegment StartX=170 StartY=6 StartZ=0 EndX=170 EndY=-40 EndZ=0
    g1: LineSegment StartX=170 StartY=-40 StartZ=0 EndX=205 EndY=-40 EndZ=0
    g2: LineSegment StartX=205 StartY=-40 StartZ=0 EndX=205 EndY=6 EndZ=0
    g3: LineSegment StartX=205 StartY=6 StartZ=0 EndX=170 EndY=6 EndZ=0
    g4: Circle CenterX=195.8 CenterY=-30 CenterZ=0 NormalX=0 NormalY=0 NormalZ=1 AngleXU=0 Radius=1.375
    g5: Circle CenterX=195.8 CenterY=-4 CenterZ=0 NormalX=0 NormalY=0 NormalZ=1 AngleXU=0 Radius=1.375
    g6: Circle CenterX=176.8 CenterY=-30 CenterZ=0 NormalX=0 NormalY=0 NormalZ=1 AngleXU=0 Radius=1.375
    g7: Circle CenterX=176.8 CenterY=-4 CenterZ=0 NormalX=0 NormalY=0 NormalZ=1 AngleXU=0 Radius=1.375
    g8: Circle CenterX=200 CenterY=-36 CenterZ=0 NormalX=0 NormalY=0 NormalZ=1 AngleXU=0 Radius=1.625
    g9: Circle CenterX=200 CenterY=2 CenterZ=0 NormalX=0 NormalY=0 NormalZ=1 AngleXU=0 Radius=1.625
    g10: Circle CenterX=175 CenterY=2 CenterZ=0 NormalX=0 NormalY=0 NormalZ=1 AngleXU=0 Radius=1.625
    g11: Circle CenterX=175 CenterY=-36 CenterZ=0 NormalX=0 NormalY=0 NormalZ=1 AngleXU=0 Radius=1.625
  constraints (36):
    c: Coincident(g0,g1)
    c: Coincident(g1,g2)
    c: Coincident(g2,g3)
    c: Coincident(g3,g0)
    c: Vertical(g0)
    c: Vertical(g2)
    c: Horizontal(g1)
    c: Horizontal(g3)
    c: DistanceX(g3,g3) = 35
    c: Distance(g0) = 46
    c: Distance(g0,g-2) = 170
    c: Distance(g0,g-1) = 40
    c: Equal(g4,g6)
    c: Equal(g4,g7)
    c: Equal(g4,g5)
    c: Diameter(g4) = 2.75
    c: Distance(g4,g2) = 9.2
    c: Distance(g7,g3) = 10
    c: Distance(g6,g1) = 10
    c: Distance(g8,g2) = 5
    c: Equal(g8,g9)
    c: Diameter(g8) = 3.25
    c: Distance(g11,g1) = 4
    c: Distance(g10,g3) = 4
    c: Distance(g10,g0) = 5
    c: Equal(g10,g11)
    c: Diameter(g10) = 3.25
    c: Horizontal(g9,g10)
    c: Horizontal(g8,g11)
    c: Horizontal(g4,g6)
    c: Horizontal(g7,g5)
    c: DistanceX(g0,g7) = 6.8
    c: Vertical(g6,g7)
    c: Vertical(g11,g10)
    c: Vertical(g8,g9)
    c: Vertical(g5,g4)
FEATURE [Part::Extrusion] Extrude036
  Base = -> Sketch037
  Dir = (0,0,1)
  DirMode = 2
  FaceMakerClass = Part::FaceMakerBullseye
  FaceMakerMode = 3
  LengthFwd = 8
  LengthRev = 0
  Placement = pos=(0,0,-14) rot=(0,0,1;0rad)
  Solid = true
  Symmetric = false
FEATURE [Part::Fillet] Fillet036  label="Holder002"
  Base = -> Extrude036
  EdgeLinks = -> Extrude036 [?Edge1,?Edge2,Edge3,Edge4,?Edge5,Edge6,Edge7,?Edge8,Edge9,Edge10,Edge11,Edge12]
  Edges = 12 edges: [Edge1 r=3,Edge2 r=3,Edge3 r=1,Edge4 r=1,Edge5 r=3,Edge6 r=1,Edge7 r=1,Edge8 r=3,Edge9 r=1,Edge10 r=1,Edge11 r=1,Edge12 r=1]
FEATURE [Part::Cut] Cut052  label="Holder_M3_cut001"
  Base = -> Fillet036
  Refine = true
  Tool = -> Fusion054
FEATURE [App::Part] _51659_8_05358_PUMPE__SW0001  label="Pump"
  Group = -> [Part__Feature533,Part__Feature534,Part__Feature535,Part__Feature536,Part__Feature537]
  Origin = -> Origin092
  Placement = pos=(183,-17,11) rot=(0.57735,0.57735,0.57735;2.0944rad)
FEATURE [App::Part] Part017
  Group = -> [_51659_8_05358_PUMPE__SW0001,Sketch037,Extrude036,Fillet036,Cylinder070,Cylinder071,Cylinder072,Cylinder073,Fusion054,Cut052]
  Origin = -> Origin093
  Placement = pos=(90,144,-10) rot=(0.57735,-0.57735,0.57735;2.0944rad)
